FCSTD DOCUMENT  (FreeCAD 0.22R34651 (Git))
Label: composit_stand5
License: All rights reserved
LicenseURL: http://en.wikipedia.org/wiki/All_rights_reserved
objects: Sketcher::SketchObject×88, Part::FeaturePython×57, PartDesign::Pocket×43, PartDesign::SubShapeBinder×37, PartDesign::Body×23, PartDesign::FeaturePython×21, Part::Compound×18, PartDesign::Pad×17, PartDesign::Mirrored×11, PartDesign::Boolean×9, App::DocumentObjectGroup×8, App::Link×6, Part::Mirroring×6, TechDraw::DrawViewPart×6, Part::Part2DObjectPython×5, Part::Extrusion×4, PartDesign::CoordinateSystem×4, PartDesign::Hole×4, Path::FeaturePython×4, TechDraw::DrawViewDimension×4, +12 more types
note: 435 computed .brp shape members not serialized (recipe doc carries the construction recipe); baked Part::Feature solids carry a one-line shape summary decoded from their .brp
EXTERNAL_REF file=module.FCStd obj=Spreadsheet
EXTERNAL_REF file=module.FCStd obj=Sketch
EXTERNAL_REF file=module.FCStd obj=Body
EXTERNAL_REF file=composit-properties.FCStd obj=Spreadsheet
EXTERNAL_REF file=dropper.FCStd obj=Part
EXTERNAL_REF file=ULI-3865416.FCStd obj=Spreadsheet
EXTERNAL_REF file=UST-E32 WHITE 2M.FCStd obj=Body

FEATURE [Sketcher::SketchObject] Sketch005  label="main_sketch"
  FullyConstrained = true
  expr: Constraints[25] = module#<<Properties>>.module_width * 2 + 2 mm * 1
  sketch-geometry (11):
    g0: LineSegment StartX=-290.084 StartY=134.058 StartZ=0 EndX=-164.614 EndY=0 EndZ=0
    g1: LineSegment StartX=-164.614 StartY=0 StartZ=0 EndX=164.614 EndY=0 EndZ=0
    g2: LineSegment StartX=164.614 StartY=0 StartZ=0 EndX=290.084 EndY=134.058 EndZ=0
    g3: LineSegment StartX=-149 StartY=36 StartZ=0 EndX=149 EndY=36 EndZ=0
    g4: LineSegment StartX=149 StartY=36 StartZ=0 EndX=251.5 EndY=145.516 EndZ=0
    g5: LineSegment StartX=149 StartY=0 StartZ=0 EndX=149 EndY=36 EndZ=0
    g6: LineSegment StartX=149 StartY=36 StartZ=0 EndX=175.284 EndY=11.4 EndZ=0
    g7: LineSegment StartX=226.534 StartY=66.158 StartZ=0 EndX=200.25 EndY=90.758 EndZ=0
    g8: GeomPoint X=226.534 Y=66.158 Z=0
    g9: LineSegment StartX=-281.5 StartY=124.887 StartZ=0 EndX=281.5 EndY=124.887 EndZ=0
    g10: LineSegment StartX=251.5 StartY=145.516 StartZ=0 EndX=277.784 EndY=120.916 EndZ=0
  constraints (35):
    c: Coincident(g0,g1)
    c: Coincident(g1,g2)
    c: Symmetric(g1,g0,g-2)
    c: PointOnObject(g1,g-1)
    c: Symmetric(g0,g2,g-2)
    c: Coincident(g4,g3)
    c: PointOnObject(g5,g1)
    c: Coincident(g5,g3)
    c: Coincident(g5,g6)
    c: PointOnObject(g6,g2)
    c: Perpendicular(g6,g2)
    c: Perpendicular(g4,g6)
    c: Perpendicular(g1,g5)
    c: Equal(g5,g6)
    c: DistanceY(g5,g5) = 36
    c: DistanceX(g1,g1) = 329.228  'inner_width'
    c: Angle(g2) = 0.818478  'angle'
    c: Symmetric(g3,g3,g-2)
    c: Distance(g4) = 150
    c: PointOnObject(g7,g2)
    c: Perpendicular(g4,g7)
    c: Symmetric(g3,g4,g7)
    c: Coincident(g8,g7)
    c: DistanceY(g2) = 134.058  'length'
    c: DistanceX(g0,g2) = 580.168  'outer_width'
    c: DistanceX(g3,g3) = 298
    c: PointOnObject(g9,g0)
    c: PointOnObject(g9,g2)
    c: Horizontal(g9)
    c: DistanceX(g9,g9) = 563
    c: DistanceX(g3,g4) = 102.5
    c: Coincident(g10,g4)
    c: PointOnObject(g10,g2)
    c: Perpendicular(g4,g10)
    c: Distance(g10,g2) = 18
FEATURE [Part::FeaturePython] Placment  # WARN: FeaturePython — macro-defined, semantics opaque (R4)
  AttacherType = Attacher::AttachEngine3D
  AttachmentOffset = pos=(0,0,0) rot=(-0.707107,0,0.707107;3.14159rad)
  ExposePlacement = true
  MapMode = 7
  MarkerShape = 1
  MarkerSize = 20
  NumElements = 1
  Placement = pos=(226.534,66.158,0) rot=(-0.852419,-0.369717,0.369717;1.7298rad)
  Support = -> [Sketch005]
  Type = lattice2AttachablePlacement.AttachablePlacement
  isLattice = 1
FEATURE [Part::FeaturePython] LinearArray  # WARN: FeaturePython — macro-defined, semantics opaque (R4)
  Alignment = 0
  CellStart = A1
  Count = 2
  Dir = (1,0,0)
  DirIsDriven = true
  DistributionLaw = 0
  DrivenProperty = 1
  EndInclusive = true
  ExposePlacement = false
  GeneratorMode = 1
  MarkerShape = 1
  MarkerSize = 0
  NumElements = 2
  OrientMode = 1
  Placement = pos=(-75,0,0) rot=(-1,0,0;1.5708rad)
  Point = (0,0,0)
  PointIsDriven = true
  Reverse = false
  SpanEnd = 150
  SpanStart = 0
  Step = 150
  Type = lattice2LinearArray.LinearArray
  VSGVersion = 1
  Values = 0.0 | 150.0
  ValuesSource = 2
  isLattice = 1
  expr: .Placement.Base.x = -.Dir.x * SpanEnd / 2
  expr: SpanEnd = Step * (Count - 1)
  expr: Step = module#<<Properties>>.module_width + 2 mm
FEATURE [App::Link] Link  label="module_holes"
  LinkedObject = -> <external module.FCStd>#Sketch
FEATURE [Part::Extrusion] Extrude
  Base = -> Link
  Dir = (0,0,1)
  DirMode = 2
  FaceMakerClass = Part::FaceMakerBullseye
  LengthFwd = 10
  LengthRev = 0
  Solid = true
  Symmetric = true
FEATURE [Part::FeaturePython] LinearArray001  # WARN: FeaturePython — macro-defined, semantics opaque (R4)
  Alignment = 0
  CellStart = A1
  Count = 5
  Dir = (1,0,0)
  DirIsDriven = true
  DistributionLaw = 0
  DrivenProperty = 1
  EndInclusive = true
  ExposePlacement = false
  GeneratorMode = 1
  MarkerShape = 1
  MarkerSize = 0
  NumElements = 5
  OrientMode = 1
  Placement = pos=(0,0,0) rot=(0,-1,0;1.5708rad)
  Point = (0,0,0)
  PointIsDriven = true
  Reverse = false
  SpanEnd = 100
  SpanStart = 0
  Step = 80
  Type = lattice2LinearArray.LinearArray
  VSGVersion = 1
  Values = 0.0 | 80.0 | 160.0 | 240.0 | 320.0
  ValuesSource = 2
  isLattice = 1
  expr: Step = module#<<Properties>>.module_fixture_distance_y
FEATURE [Part::FeaturePython] Placment001  # WARN: FeaturePython — macro-defined, semantics opaque (R4)
  AttacherType = Attacher::AttachEngine3D
  AttachmentOffset = pos=(0,0,0) rot=(0,0,1;3.14159rad)
  ExposePlacement = true
  MapMode = 2
  MarkerShape = 1
  MarkerSize = 50
  NumElements = 1
  Placement = pos=(226.534,66.158,0) rot=(-0.293211,0.676028,0.676028;3.71203rad)
  Support = -> [Placment]
  Type = lattice2AttachablePlacement.AttachablePlacement
  isLattice = 1
FEATURE [Part::FeaturePython] Mirror  label="Mirror of Placment"  # WARN: FeaturePython — macro-defined, semantics opaque (R4)
  ExposePlacement = false
  FlipX = true
  FlipY = false
  FlipZ = false
  MarkerShape = 1
  MarkerSize = 50
  NumElements = 1
  Object = -> Placment001
  ObjectTraversal = 0
  Type = lattice2Mirror.LatticeMirror
  isLattice = 1
FEATURE [Part::FeaturePython] Join  # WARN: FeaturePython — macro-defined, semantics opaque (R4)
  ExposePlacement = false
  Interleave = false
  Links = -> [LinearArray,Mirror,Placment]
  MarkerShape = 1
  MarkerSize = 10
  NumElements = 4
  Type = lattice2JoinArrays.JoinArrays
  isLattice = 1
FEATURE [Part::FeaturePython] Populate  label="Populate LinearArray001 with Join"  # WARN: FeaturePython — macro-defined, semantics opaque (R4)
  Copying = 0
  ExposePlacement = false
  MarkerShape = 1
  MarkerSize = 0
  NumElements = 20
  Object = -> Join
  OutputCompounding = 0
  PlacementsTo = -> LinearArray001
  Referencing = 1
  Type = lattice2PopulateCopies.LatticePopulateCopies
  isLattice = 1
FEATURE [Part::FeaturePython] Populate001  label="Populate Populate LinearArray001 with Join with Extrude"  # WARN: FeaturePython — macro-defined, semantics opaque (R4)
  Copying = 0
  ExposePlacement = false
  MarkerShape = 1
  MarkerSize = 0
  NumElements = 0
  Object = -> Extrude
  OutputCompounding = 1
  Placement = pos=(0,0,300) rot=(0,0,1;0rad)
  PlacementsTo = -> Populate
  Referencing = 0
  Type = lattice2PopulateCopies.LatticePopulateCopies
  isLattice = 0
FEATURE [App::Link] Link002  label="Body001"
  LinkPlacement = pos=(0,0,0) rot=(0,0,1;3.14159rad)
  LinkedObject = -> <external module.FCStd>#Body
  Placement = pos=(0,0,0) rot=(0,0,1;3.14159rad)
FEATURE [Part::FeaturePython] Populate004  label="modules"  # WARN: FeaturePython — macro-defined, semantics opaque (R4)
  Copying = 0
  ExposePlacement = false
  MarkerShape = 1
  MarkerSize = 0
  NumElements = 0
  Object = -> Link002
  OutputCompounding = 1
  Placement = pos=(0,0,300) rot=(0,0,1;0rad)
  PlacementsTo = -> Populate
  Referencing = 0
  Type = lattice2PopulateCopies.LatticePopulateCopies
  isLattice = 0
  expr: Placement = <<Populate Populate LinearArray001 with Join with Extrude>>.Placement
FEATURE [App::Link] Link001  label="Extrude002"
  LinkPlacement = pos=(170,0,0) rot=(0,0,1;0rad)
  LinkedObject = -> Extrude001
  Placement = pos=(170,0,0) rot=(0,0,1;0rad)
FEATURE [Part::Part2DObjectPython] Circle  label="hole_3.4"  # Draft 2D object (typed FeaturePython)
  Area = 9.0792
  FirstAngle = 0
  LastAngle = 0
  MakeFace = true
  Radius = 1.7
FEATURE [Part::Extrusion] Extrude001  label="hole_3.4_extrude"
  Base = -> Circle
  Dir = (0,0,1)
  DirMode = 2
  FaceMakerClass = Part::FaceMakerBullseye
  LengthFwd = 10
  LengthRev = 0
  Solid = false
  Symmetric = false
FEATURE [Part::FeaturePython] Clone001  label="Extrude004"  # Draft clone (typed FeaturePython)
  AttacherType = Attacher::AttachEngine3D
  Fuse = false
  Objects = -> [Extrude001]
  Placement = pos=(0,5,0) rot=(1,0,0;1.5708rad)
  Scale = (1,1,1)
FEATURE [Part::FeaturePython] Clone  label="Extrude003"  # Draft clone (typed FeaturePython)
  AttacherType = Attacher::AttachEngine3D
  Fuse = false
  Objects = -> [Extrude001]
  Placement = pos=(154.614,5,0) rot=(1,0,0;1.5708rad)
  Scale = (1,1,1)
  expr: .Placement.Base.x = <<main_sketch>>.Constraints.inner_width / 2 - 10 mm
FEATURE [Part::Compound] Compound003
  Links = -> [Link001,Extrude001]
  Placement = pos=(168.01,4.96989,0) rot=(0.852419,0.369717,0.369717;1.7298rad)
  expr: .Placement.Base.x = <<main_sketch>>.Constraints.inner_width / 2 + .Placement.Base.y * cos(<<main_sketch>>.Constraints.angle)
  expr: .Placement.Base.y = <<main_sketch>>.Constraints.length / 2 - <<Extrude002>>.Placement.Base.x * sin(<<main_sketch>>.Constraints.angle) / 2
  expr: .Placement.Rotation.Yaw = <<main_sketch>>.Constraints.angle
FEATURE [Part::Compound] Compound001
  Links = -> [Compound003,Clone]
FEATURE [Part::Mirroring] Part__Mirroring  label="Compound001 (Mirror #1)"
  Base = (0,0,0)
  Normal = (1,0,0)
  Source = -> Compound001
FEATURE [Part::Compound] Compound004
  Links = -> [Compound001,Part__Mirroring,Clone001]
  Placement = pos=(0,0,31) rot=(0,0,1;0rad)
FEATURE [Sketcher::SketchObject] Sketch007
  FullyConstrained = false
  MapMode = 5
  Placement = pos=(0,0,0) rot=(1,0,0;1.5708rad)
  Support = -> [XZ_Plane001]
  expr: Constraints[10] = BaseBend001.length
  sketch-geometry (5):
    g0: LineSegment StartX=-500 StartY=191.028 StartZ=0 EndX=-500 EndY=87 EndZ=0
    g1: LineSegment StartX=-500 StartY=87 StartZ=0 EndX=500 EndY=87 EndZ=0
    g2: LineSegment StartX=500 StartY=87 StartZ=0 EndX=500 EndY=191.028 EndZ=0
    g3: LineSegment StartX=500 StartY=191.028 StartZ=0 EndX=-500 EndY=191.028 EndZ=0
    g4: GeomPoint X=0 Y=139.014 Z=0
  constraints (12):
    c: Coincident(g0,g1)
    c: Coincident(g1,g2)
    c: Coincident(g2,g3)
    c: Coincident(g3,g0)
    c: Horizontal(g1)
    c: Horizontal(g3)
    c: Vertical(g0)
    c: Vertical(g2)
    c: Symmetric(g1,g0,g4)
    c: PointOnObject(g4,g-2)
    c: DistanceX(g1,g1) = 1000
    c: DistanceY(g1) = 87
FEATURE [Part::Part2DObjectPython] Line  # Draft 2D object (typed FeaturePython)
  Area = 0
  Bend_Angle = 6.03317
  ChamferSize = 0
  Closed = false
  End = (290.084,134.058,14.0901)
  FilletRadius = 0
  Length = 184.154
  MakeFace = true
  Points = (2) [(164.614,0,0),(290.084,134.058,14.0901)]
  SideAngle = 4.1058
  Start = (164.614,0,0)
  Subdivisions = 0
  expr: .End.x = Sketch005.Constraints.outer_width / 2
  expr: .End.y = <<sink_base>>.Constraints.length
  expr: .End.z = <<sink_base>>.Constraints.sink_difference
  expr: .Start.x = <<main_sketch>>.Constraints.inner_width / 2
  expr: Bend_Angle = asin(.End.z / .End.y)
  expr: SideAngle = asin(.End.z / (.End.y + (.End.x - .Start.x) / 2))
FEATURE [PartDesign::SubShapeBinder] Binder
  BindCopyOnChange = 0
  BindMode = 0
  ClaimChildren = false
  Context = -> Part [Body001.Binder.]
  Fuse = false
  MakeFace = true
  OffsetFill = false
  OffsetIntersection = false
  OffsetJoinType = 0
  OffsetOpenResult = false
  PartialLoad = false
  Relative = false
  Support = -> [Sketch005]
  _Version = 2
FEATURE [Sketcher::SketchObject] Sketch006
  ExternalGeometry = -> [Binder]
  FullyConstrained = true
  MapMode = 5
  Support = -> [XY_Plane001]
  sketch-geometry (1):
    g0: LineSegment StartX=161.19 StartY=0 StartZ=0 EndX=286.66 EndY=134.058 EndZ=0
  constraints (5):
    c: PointOnObject(g0,g-1)
    c: Horizontal(g0,g-3)
    c: Parallel(g-3,g0)
    c: Distance(g0,g-3) = 2.5
    c: DistanceX(g0) = 286.66  'max_right'
FEATURE [Sketcher::SketchObject] Sketch001  label="sink_base"
  ExternalGeometry = -> [Binder]
  FullyConstrained = true
  MapMode = 5
  Placement = pos=(0,0,0) rot=(0.57735,0.57735,0.57735;2.0944rad)
  Support = -> [YZ_Plane001]
  sketch-geometry (4):
    g0: LineSegment StartX=0 StartY=0 StartZ=0 EndX=0 EndY=90 EndZ=0
    g1: LineSegment StartX=0 StartY=0 StartZ=0 EndX=134.058 EndY=14.0901 EndZ=0
    g2: ArcOfCircle CenterX=2.5 CenterY=2.77653 CenterZ=0 NormalX=0 NormalY=0 NormalZ=1 AngleXU=0 Radius=2.5 StartAngle=3.14159 EndAngle=4.81711
    g3: GeomPoint X=2.76132 Y=0.290227 Z=0
  constraints (13):
    c: Vertical(g0)
    c: Coincident(g1,g0)
    c: Angle(g1) = 0.10472  'angle'
    c: DistanceY(g0,g0) = 90
    c: Coincident(g0,g-1)
    c: Vertical(g-3,g1)
    c: DistanceX(g1) = 134.058  'length'
    c: DistanceY(g1) = 14.0901  'sink_difference'
    c: Tangent(g2,g1) = -1.5708
    c: Tangent(g2,g0) = 1.5708
    c: Radius(g2) = 2.5
    c: DistanceX(g2) = 2.76132
    c: Coincident(g3,g2)
FEATURE [Sketcher::SketchObject] Sketch004
  ExternalGeometry = -> [Sketch001]
  FullyConstrained = false
  MapMode = 7
  Placement = pos=(164.614,-1.42e-14,0) rot=(0.880512,-0.347772,-0.322108;1.77331rad)
  Support = -> [Line]
  sketch-geometry (9):
    g0: LineSegment StartX=-120.186 StartY=8.60659 StartZ=0 EndX=0 EndY=0 EndZ=0
    g1: ArcOfCircle CenterX=-2.5 CenterY=2.68543 CenterZ=0 NormalX=0 NormalY=0 NormalZ=1 AngleXU=0 Radius=2.5 StartAngle=4.6409 EndAngle=6.28319
    g2: LineSegment StartX=-2.67857 StartY=0.191814 StartZ=0 EndX=-2.64286 EndY=0.690537 EndZ=0
    g3: LineSegment StartX=-0.5 StartY=2.68543 StartZ=0 EndX=-0.5 EndY=11.4404 EndZ=0
    g4: LineSegment StartX=-0.5 StartY=11.4404 StartZ=0 EndX=-1.1e-15 EndY=11.4404 EndZ=0
    g5: LineSegment StartX=-1.1e-15 StartY=11.4404 StartZ=0 EndX=0 EndY=2.68543 EndZ=0
    g6: ArcOfCircle CenterX=-2.5 CenterY=2.68543 CenterZ=0 NormalX=0 NormalY=0 NormalZ=1 AngleXU=0 Radius=2 StartAngle=4.6409 EndAngle=6.28319
    g7: LineSegment StartX=0 StartY=2.68543 StartZ=0 EndX=-2.5 EndY=2.68543 EndZ=0
    g8: LineSegment StartX=-2.67857 StartY=0.191814 StartZ=0 EndX=-2.5 EndY=2.68543 EndZ=0
  constraints (21):
    c: Coincident(g0,g-3)
    c: Coincident(g0,g-1)
    c: Tangent(g1,g-2) = -1.5708
    c: Radius(g1) = 2.5
    c: Tangent(g1,g0) = -1.5708
    c: Coincident(g2,g1)
    c: Vertical(g3)
    c: Coincident(g4,g3)
    c: Coincident(g5,g4)
    c: Tangent(g5,g1) = 1.5708
    c: Horizontal(g4)
    c: Perpendicular(g1,g2)
    c: Coincident(g6,g1)
    c: Coincident(g6,g2)
    c: Tangent(g6,g3) = -1.5708
    c: Radius(g6) = 2
    c: Coincident(g7,g1)
    c: Coincident(g7,g1)
    c: Coincident(g8,g1)
    c: Coincident(g8,g1)
    c: Angle(g8,g7) = 1.64228
FEATURE [PartDesign::SubShapeBinder] Binder006
  BindCopyOnChange = 0
  BindMode = 0
  ClaimChildren = true
  Context = -> Body002 [Binder006.]
  Fuse = false
  MakeFace = true
  OffsetFill = false
  OffsetIntersection = false
  OffsetJoinType = 0
  OffsetOpenResult = false
  PartialLoad = false
  Relative = false
  Support = -> [Compound006]
  _Version = 2
FEATURE [PartDesign::Pad] Pad
  Direction = (0,0,1)
  Length = 5
  Length2 = 10
  Profile = -> Binder006
  Type = 0
FEATURE [PartDesign::SubShapeBinder] Binder007
  BindCopyOnChange = 0
  BindMode = 0
  ClaimChildren = true
  Context = -> Body002 [Binder007.]
  Fuse = false
  MakeFace = true
  OffsetFill = false
  OffsetIntersection = false
  OffsetJoinType = 0
  OffsetOpenResult = false
  PartialLoad = false
  Relative = false
  Support = -> [Populate008]
  _Version = 2
FEATURE [PartDesign::Pocket] Pocket005
  BaseFeature = -> Pad
  Direction = (0,0,-1)
  Length = 2.5
  Length2 = 5
  Profile = -> Binder007
  Reversed = true
  Type = 0
FEATURE [Part::Box] Box  label="Cube"
  AttacherType = Attacher::AttachEngine3D
  AttachmentOffset = pos=(0,0,-5) rot=(0,0,1;0rad)
  Height = 60
  Length = 560
  Placement = pos=(-280,0,-9) rot=(0,0,1;0rad)
  Width = 60
  expr: .Placement.Base.x = -Length / 2
FEATURE [PartDesign::SubShapeBinder] Binder004  label="fix"
  BindCopyOnChange = 0
  BindMode = 0
  ClaimChildren = false
  Fuse = false
  MakeFace = true
  Offset = 0.5
  OffsetFill = false
  OffsetIntersection = false
  OffsetJoinType = 0
  OffsetOpenResult = false
  PartialLoad = false
  Relative = true
  Support = -> [<external dropper.FCStd>#Part[Body.Binder.]]
  _Version = 2
FEATURE [PartDesign::SubShapeBinder] Binder008
  BindCopyOnChange = 0
  BindMode = 0
  ClaimChildren = true
  Context = -> Body002 [Binder008.]
  Fuse = false
  MakeFace = true
  OffsetFill = false
  OffsetIntersection = false
  OffsetJoinType = 0
  OffsetOpenResult = false
  PartialLoad = false
  Relative = false
  Support = -> [Populate010]
  _Version = 2
FEATURE [PartDesign::Pocket] Pocket006
  BaseFeature = -> Pocket005
  Direction = (0,0,-1)
  Length = 5
  Length2 = 5
  Midplane = true
  Profile = -> Binder008
  Type = 1
FEATURE [PartDesign::SubShapeBinder] Binder005  label="feed"
  BindCopyOnChange = 0
  BindMode = 0
  ClaimChildren = false
  Fuse = false
  MakeFace = true
  OffsetFill = false
  OffsetIntersection = false
  OffsetJoinType = 0
  OffsetOpenResult = false
  PartialLoad = false
  Relative = true
  Support = -> [<external dropper.FCStd>#Part[Body.Sketch008.]]
  _Version = 2
FEATURE [PartDesign::SubShapeBinder] Binder001
  BindCopyOnChange = 0
  BindMode = 0
  ClaimChildren = false
  Context = -> Body [Binder001.]
  Fuse = false
  MakeFace = true
  OffsetFill = false
  OffsetIntersection = false
  OffsetJoinType = 0
  OffsetOpenResult = false
  PartialLoad = false
  Relative = true
  Support = -> [Sketch005]
  _Version = 2
FEATURE [Sketcher::SketchObject] Sketch009
  ExternalGeometry = -> [Binder001]
  FullyConstrained = true
  MapMode = 5
  Support = -> [XY_Plane]
  expr: Constraints[12] = composit_properties#<<Properties>>.al_thickness
  expr: Constraints[13] = -composit_properties#<<Properties>>.thickness
  sketch-geometry (5):
    g0: LineSegment StartX=0 StartY=-3 StartZ=0 EndX=0 EndY=109.928 EndZ=0
    g1: LineSegment StartX=0 StartY=109.928 StartZ=0 EndX=267.5 EndY=109.928 EndZ=0
    g2: LineSegment StartX=267.5 StartY=109.928 StartZ=0 EndX=267.719 EndY=109.723 EndZ=0
    g3: LineSegment StartX=267.719 StartY=109.723 StartZ=0 EndX=267.719 EndY=-3 EndZ=0
    g4: LineSegment StartX=267.719 StartY=-3 StartZ=0 EndX=0 EndY=-3 EndZ=0
  constraints (15):
    c: PointOnObject(g0,g-2)
    c: Coincident(g0,g1)
    c: Horizontal(g1)
    c: Coincident(g1,g2)
    c: Coincident(g2,g3)
    c: Vertical(g3)
    c: Coincident(g3,g4)
    c: DistanceX(g1,g1) = 267.5
    c: PointOnObject(g1,g-3)
    c: Coincident(g4,g0)
    c: Vertical(g0)
    c: Horizontal(g4)
    c: Distance(g2) = 0.3
    c: DistanceY(g0) = -3
    c: Perpendicular(g-3,g2)
FEATURE [Sketcher::SketchObject] Sketch  label="base_sketch"
  ExternalGeometry = -> [Binder001]
  FullyConstrained = true
  sketch-geometry (9):
    g0: LineSegment StartX=-164.614 StartY=0 StartZ=0 EndX=164.614 EndY=0 EndZ=0
    g1: LineSegment StartX=164.614 StartY=0 StartZ=0 EndX=290.084 EndY=134.058 EndZ=0
    g2: LineSegment StartX=290.084 StartY=134.058 StartZ=0 EndX=300.084 EndY=134.058 EndZ=0
    g3: LineSegment StartX=300.084 StartY=134.058 StartZ=0 EndX=300.084 EndY=-41 EndZ=0
    g4: LineSegment StartX=-164.614 StartY=0 StartZ=0 EndX=-290.084 EndY=134.058 EndZ=0
    g5: LineSegment StartX=-290.084 StartY=134.058 StartZ=0 EndX=-300.084 EndY=134.058 EndZ=0
    g6: LineSegment StartX=-300.084 StartY=134.058 StartZ=0 EndX=-300.084 EndY=-41 EndZ=0
    g7: LineSegment StartX=297.084 StartY=-41 StartZ=0 EndX=300.084 EndY=-41 EndZ=0
    g8: LineSegment StartX=-300.084 StartY=-41 StartZ=0 EndX=-297.084 EndY=-41 EndZ=0
  constraints (23):
    c: Coincident(g0,g-3)
    c: Coincident(g0,g1)
    c: Coincident(g1,g-3)
    c: Coincident(g1,g2)
    c: Horizontal(g2)
    c: Coincident(g2,g3)
    c: Vertical(g3)
    c: Coincident(g0,g4)
    c: Coincident(g4,g5)
    c: Coincident(g5,g6)
    c: Symmetric(g0,g0,g-2)
    c: Symmetric(g1,g4,g-2)
    c: Symmetric(g5,g2,g-2)
    c: Symmetric(g3,g6,g-2)
    c: DistanceX(g2,g2) = 10
    c: DistanceY(g3) = -41  'back_offset'
    c: DistanceX(g6,g3) = 600.168  'outer_width'
    c: Coincident(g7,g3)
    c: Coincident(g8,g6)
    c: Horizontal(g8)
    c: Equal(g8,g7)
    c: Horizontal(g7)
    c: DistanceX(g7,g7) = 3
FEATURE [PartDesign::SubShapeBinder] Binder009
  BindCopyOnChange = 0
  BindMode = 0
  ClaimChildren = false
  Context = -> Part002 [Body003.Binder009.]
  Fuse = false
  MakeFace = true
  OffsetFill = false
  OffsetIntersection = false
  OffsetJoinType = 0
  OffsetOpenResult = false
  PartialLoad = false
  Relative = true
  Support = -> [Sketch005]
  _Version = 2
FEATURE [Sketcher::SketchObject] Sketch011  label="top_BaseSketch"
  ExternalGeometry = -> [Binder009]
  FullyConstrained = true
  Placement = pos=(0,0,0) rot=(0.57735,0.57735,0.57735;2.0944rad)
  expr: Constraints[8] = <<ULI-3865416>>#<<Properties>>.width
  sketch-geometry (4):
    g0: LineSegment StartX=158.611 StartY=20.0409 StartZ=0 EndX=138.225 EndY=23.6354 EndZ=0
    g1: LineSegment StartX=138.225 StartY=23.6354 StartZ=0 EndX=134.058 EndY=0 EndZ=0
    g2: LineSegment StartX=134.058 StartY=0 StartZ=0 EndX=-15 EndY=0 EndZ=0
    g3: GeomPoint X=158.611 Y=20.0409 Z=0
  constraints (11):
    c: Coincident(g0,g1)
    c: Coincident(g1,g2)
    c: Horizontal(g2)
    c: DistanceY(g2) = 0
    c: DistanceX(g2,g-1) = 15
    c: Vertical(g-3,g1)
    c: Perpendicular(g1,g0)
    c: Angle(g1,g-1) = 1.74533
    c: Distance(g0) = 20.7
    c: Distance(g1) = 24
    c: Coincident(g3,g0)
FEATURE [PartDesign::SubShapeBinder] Binder010
  BindCopyOnChange = 0
  BindMode = 0
  ClaimChildren = true
  Context = -> Body003 [Binder010.]
  Fuse = false
  MakeFace = true
  OffsetFill = false
  OffsetIntersection = false
  OffsetJoinType = 0
  OffsetOpenResult = false
  PartialLoad = false
  Relative = false
  Support = -> [Populate009]
  _Version = 2
FEATURE [Part::FeaturePython] LinearArray002  # WARN: FeaturePython — macro-defined, semantics opaque (R4)
  Alignment = 0
  CellStart = A1
  Count = 2
  Dir = (1,0,0)
  DirIsDriven = true
  DistributionLaw = 0
  DrivenProperty = 1
  EndInclusive = true
  ExposePlacement = false
  GeneratorMode = 0
  MarkerShape = 1
  MarkerSize = 0
  NumElements = 2
  OrientMode = 1
  Placement = pos=(-32.5,0,14) rot=(1,0,0;1.5708rad)
  Point = (0,0,0)
  PointIsDriven = true
  Reverse = false
  SpanEnd = 65
  SpanStart = 0
  Step = 65
  Type = lattice2LinearArray.LinearArray
  VSGVersion = 1
  Values = 0.0 | 65.0
  ValuesSource = 2
  isLattice = 1
  expr: .Placement.Base.x = -SpanEnd / 2
FEATURE [Part::FeaturePython] Populate007  label="droppers_placements"  # WARN: FeaturePython — macro-defined, semantics opaque (R4)
  Copying = 0
  ExposePlacement = false
  MarkerShape = 1
  MarkerSize = 10
  NumElements = 8
  Object = -> LinearArray002
  OutputCompounding = 0
  PlacementsTo = -> Join
  Referencing = 0
  Type = lattice2PopulateCopies.LatticePopulateCopies
  isLattice = 1
FEATURE [Part::FeaturePython] ArrayFilter  # WARN: FeaturePython — macro-defined, semantics opaque (R4)
  Base = -> Populate007
  ExposePlacement = false
  FilterType = 3
  Invert = false
  MarkerShape = 1
  MarkerSize = 0
  NumElements = 6
  Stencil = -> Box
  Type = lattice2ArrayFilter.LatticeArrayFilter
  WindowFrom = 0
  WindowTo = 1
  isLattice = 1
FEATURE [Part::FeaturePython] Placment002  # WARN: FeaturePython — macro-defined, semantics opaque (R4)
  AttacherType = Attacher::AttachEngine3D
  AttachmentOffset = pos=(0,0,0) rot=(-0.5774,0.5774,0.5774;2.0944rad)
  ExposePlacement = true
  MapMode = 1
  MarkerShape = 1
  MarkerSize = 50
  NumElements = 1
  Placement = pos=(238.521,99.4531,0) rot=(0,0,1;0rad)
  Support = -> [Populate007]
  Type = lattice2AttachablePlacement.AttachablePlacement
  isLattice = 1
  expr: .AttachmentOffset.Base.x = sin(<<main_sketch>>.Constraints.angle) * .AttachmentOffset.Base.y
FEATURE [Part::FeaturePython] Mirror001  label="Mirror001 of Placment002"  # WARN: FeaturePython — macro-defined, semantics opaque (R4)
  ExposePlacement = false
  FlipX = true
  FlipY = false
  FlipZ = false
  MarkerShape = 1
  MarkerSize = 50
  NumElements = 1
  Object = -> Placment002
  ObjectTraversal = 0
  Type = lattice2Mirror.LatticeMirror
  isLattice = 1
FEATURE [Part::FeaturePython] Join001  label="dropper_placement2"  # WARN: FeaturePython — macro-defined, semantics opaque (R4)
  ExposePlacement = false
  Interleave = false
  Links = -> [Placment002,Mirror001,ArrayFilter]
  MarkerShape = 1
  MarkerSize = 10
  NumElements = 8
  Type = lattice2JoinArrays.JoinArrays
  isLattice = 1
FEATURE [Part::FeaturePython] Populate010  label="feeds"  # WARN: FeaturePython — macro-defined, semantics opaque (R4)
  Copying = 0
  ExposePlacement = false
  MarkerShape = 1
  MarkerSize = 0
  NumElements = 0
  Object = -> Binder005
  OutputCompounding = 1
  PlacementsTo = -> Join001
  Referencing = 0
  Type = lattice2PopulateCopies.LatticePopulateCopies
  isLattice = 0
FEATURE [PartDesign::SubShapeBinder] Binder003  label="base"
  BindCopyOnChange = 0
  BindMode = 0
  ClaimChildren = false
  Fuse = false
  MakeFace = true
  OffsetFill = false
  OffsetIntersection = false
  OffsetJoinType = 0
  OffsetOpenResult = false
  PartialLoad = false
  Relative = true
  Support = -> [<external dropper.FCStd>#Part[Body001.Sketch007.]]
  _Version = 2
FEATURE [Part::Compound] Compound005
  Links = -> [Binder003,Binder004]
FEATURE [Part::FeaturePython] FuseCompound  # WARN: FeaturePython — macro-defined, semantics opaque (R4)
  Base = -> Compound005
  Refine = true
  recomputeQuota = -1
FEATURE [Part::FeaturePython] Populate008  label="Populate Populate Join with LinearArray002 with FuseCompound"  # WARN: FeaturePython — macro-defined, semantics opaque (R4)
  Copying = 0
  ExposePlacement = false
  MarkerShape = 1
  MarkerSize = 0
  NumElements = 0
  Object = -> FuseCompound
  OutputCompounding = 1
  PlacementsTo = -> Join001
  Referencing = 0
  Type = lattice2PopulateCopies.LatticePopulateCopies
  isLattice = 0
FEATURE [Sketcher::SketchObject] Sketch010
  ExternalGeometry = -> [Sketch005,Populate008]
  FullyConstrained = false
  sketch-geometry (18):
    g0: LineSegment StartX=0 StartY=17.85 StartZ=0 EndX=139.351 EndY=17.85 EndZ=0
    g1: LineSegment StartX=146.652 StartY=21.0167 StartZ=0 EndX=220.703 EndY=100.136 EndZ=0
    g2: LineSegment StartX=228.004 StartY=103.303 StartZ=0 EndX=262.098 EndY=103.303 EndZ=0
    g3: LineSegment StartX=219.146 StartY=96.2647 StartZ=0 EndX=219.817 EndY=99.1889 EndZ=0
    g4: LineSegment StartX=91 StartY=17.75 StartZ=0 EndX=91 EndY=17.85 EndZ=0
    g5: LineSegment StartX=222.021 StartY=103.203 StartZ=0 EndX=222.021 EndY=103.303 EndZ=0
    g6: LineSegment StartX=265.749 StartY=94.8865 StartZ=0 EndX=171.481 EndY=-5.83333 EndZ=0
    g7: LineSegment StartX=164.18 StartY=-9 StartZ=0 EndX=0 EndY=-9 EndZ=0
    g8: LineSegment StartX=171.185 StartY=-6.15 StartZ=0 EndX=164.614 EndY=0 EndZ=0
    g9: LineSegment StartX=164.614 StartY=0 StartZ=0 EndX=164.614 EndY=-9 EndZ=0
    g10: ArcOfCircle CenterX=139.351 CenterY=27.85 CenterZ=0 NormalX=0 NormalY=0 NormalZ=1 AngleXU=0 Radius=10 StartAngle=4.71239 EndAngle=5.53087
    g11: GeomPoint X=143.688 Y=17.85 Z=0
    g12: ArcOfCircle CenterX=228.004 CenterY=93.3031 CenterZ=0 NormalX=0 NormalY=0 NormalZ=1 AngleXU=0 Radius=10 StartAngle=1.5708 EndAngle=2.38927
    g13: GeomPoint X=223.667 Y=103.303 Z=0
    g14: ArcOfCircle CenterX=262.098 CenterY=98.3031 CenterZ=0 NormalX=0 NormalY=0 NormalZ=1 AngleXU=0 Radius=5 StartAngle=5.53087 EndAngle=7.85398
    g15: GeomPoint X=261.299 Y=103.303 Z=0
    g16: ArcOfCircle CenterX=164.18 CenterY=1 CenterZ=0 NormalX=0 NormalY=0 NormalZ=1 AngleXU=0 Radius=10 StartAngle=4.71239 EndAngle=5.53087
    g17: GeomPoint X=168.518 Y=-9 Z=0
  constraints (49):
    c: PointOnObject(g0,g-2)
    c: Horizontal(g0)
    c: Horizontal(g2)
    c: PointOnObject(g3,g1)
    c: PointOnObject(g4,g0)
    c: Vertical(g4)
    c: PointOnObject(g5,g2)
    c: Vertical(g5)
    c: DistanceY(g5,g5) = 0.1
    c: PointOnObject(g7,g-2)
    c: Horizontal(g7)
    c: PointOnObject(g8,g6)
    c: Coincident(g8,g9)
    c: PointOnObject(g9,g7)
    c: Vertical(g9)
    c: Equal(g9,g8)
    c: DistanceY(g7,g-1) = 9
    c: PointOnObject(g5,g-4)
    c: PointOnObject(g-4,g5)
    c: Perpendicular(g-6,g3)
    c: PointOnObject(g4,g-5)
    c: PointOnObject(g-5,g4)
    c: Equal(g4,g5)
    c: Parallel(g1,g-3)
    c: Parallel(g6,g-3)
    c: PointOnObject(g15,g-3)
    c: Coincident(g8,g-3)
    c: Perpendicular(g6,g8)
    c: PointOnObject(g11,g0)
    c: PointOnObject(g11,g1)
    c: Tangent(g0,g10) = -1.5708
    c: Tangent(g1,g10) = -1.5708
    c: PointOnObject(g13,g1)
    c: PointOnObject(g13,g2)
    c: Tangent(g1,g12) = 1.5708
    c: Tangent(g2,g12) = 1.5708
    c: Equal(g12,g10)
    c: Radius(g12) = 10
    c: PointOnObject(g15,g2)
    c: Tangent(g2,g14) = 1.5708
    c: PointOnObject(g17,g6)
    c: PointOnObject(g17,g7)
    c: Tangent(g6,g16) = 1.5708
    c: Tangent(g7,g16) = 1.5708
    c: Equal(g16,g12)
    c: PointOnObject(g3,g-6)
    c: Tangent(g6,g14) = 1.5708
    c: Distance(g3) = 3
    c: Radius(g14) = 5
FEATURE [Part::Mirroring] Part__Mirroring001  label="Sketch010 (Mirror #2)"
  Base = (0,0,0)
  Normal = (1,0,0)
  Source = -> Sketch010
FEATURE [Part::Compound] Compound006
  Links = -> [Sketch010,Part__Mirroring001]
FEATURE [Part::FeaturePython] Populate009  label="Populate Populate Join with LinearArray002 with base"  # WARN: FeaturePython — macro-defined, semantics opaque (R4)
  Copying = 0
  ExposePlacement = false
  MarkerShape = 1
  MarkerSize = 0
  NumElements = 0
  Object = -> Binder003
  OutputCompounding = 1
  PlacementsTo = -> Join001
  Referencing = 0
  Type = lattice2PopulateCopies.LatticePopulateCopies
  isLattice = 0
FEATURE [PartDesign::SubShapeBinder] Binder011
  BindCopyOnChange = 0
  BindMode = 0
  ClaimChildren = true
  Context = -> Body004 [Binder011.]
  Fuse = false
  MakeFace = true
  OffsetFill = false
  OffsetIntersection = false
  OffsetJoinType = 0
  OffsetOpenResult = false
  PartialLoad = false
  Relative = true
  Support = -> [Body[BaseBend.Sketch.]]
  _Version = 2
FEATURE [Sketcher::SketchObject] Sketch012
  ExternalGeometry = -> [Binder011]
  FullyConstrained = true
  MapMode = 5
  Support = -> [XY_Plane004]
  sketch-geometry (3):
    g0: LineSegment StartX=297.084 StartY=-31 StartZ=0 EndX=297.084 EndY=-41 EndZ=0
    g1: LineSegment StartX=297.084 StartY=-41 StartZ=0 EndX=-297.084 EndY=-41 EndZ=0
    g2: LineSegment StartX=-297.084 StartY=-41 StartZ=0 EndX=-297.084 EndY=-31 EndZ=0
  constraints (9):
    c: Vertical(g0)
    c: Coincident(g0,g1)
    c: Horizontal(g1)
    c: Coincident(g1,g2)
    c: Vertical(g2)
    c: Symmetric(g2,g0,g-2)
    c: DistanceY(g0,g0) = 10
    c: Horizontal(g0,g-3)
    c: DistanceX(g0,g-3) = 3
FEATURE [PartDesign::FeaturePython] BaseBend003  # WARN: FeaturePython — macro-defined, semantics opaque (R4)
  BendSide = 0
  BendSketch = -> Sketch012
  MidPlane = false
  Reverse = false
  length = 637
  radius = 0.1
  thickness = 0.3
  expr: length = BaseBend.length - 3 mm
FEATURE [Part::FeaturePython] LinearArray003  # WARN: FeaturePython — macro-defined, semantics opaque (R4)
  Alignment = 0
  CellStart = A1
  Count = 5
  Dir = (1,0,0)
  DirIsDriven = true
  DistributionLaw = 0
  DrivenProperty = 1
  EndInclusive = true
  ExposePlacement = false
  GeneratorMode = 0
  MarkerShape = 1
  MarkerSize = 0
  NumElements = 5
  OrientMode = 1
  Placement = pos=(-294.084,-36,0) rot=(0,-1,0;1.5708rad)
  Point = (0,0,0)
  PointIsDriven = true
  Reverse = false
  SpanEnd = 610
  SpanStart = 30
  Step = 145
  Type = lattice2LinearArray.LinearArray
  VSGVersion = 1
  Values = 30.0 | 175.0 | 320.0 | 465.0 | 610.0
  ValuesSource = 2
  isLattice = 1
  expr: .Placement.Base.x = -(<<base_sketch>>.Constraints.outer_width / 2 - 6 mm)
  expr: .Placement.Base.y = <<base_sketch>>.Constraints.back_offset + 5 mm
  expr: SpanEnd = BaseBend.length - SpanStart
FEATURE [Part::FeaturePython] Mirror002  label="Mirror002 of LinearArray003"  # WARN: FeaturePython — macro-defined, semantics opaque (R4)
  ExposePlacement = false
  FlipX = true
  FlipY = false
  FlipZ = false
  MarkerShape = 1
  MarkerSize = 0
  NumElements = 5
  Object = -> LinearArray003
  ObjectTraversal = 0
  Type = lattice2Mirror.LatticeMirror
  isLattice = 1
FEATURE [Part::FeaturePython] Join002  # WARN: FeaturePython — macro-defined, semantics opaque (R4)
  ExposePlacement = false
  Interleave = false
  Links = -> [LinearArray003,Mirror002]
  MarkerShape = 1
  MarkerSize = 0
  NumElements = 10
  Type = lattice2JoinArrays.JoinArrays
  isLattice = 1
FEATURE [Part::FeaturePython] Populate011  label="Populate Join002 with Extrude001"  # WARN: FeaturePython — macro-defined, semantics opaque (R4)
  Copying = 0
  ExposePlacement = false
  MarkerShape = 1
  MarkerSize = 0
  NumElements = 0
  Object = -> Extrude001
  OutputCompounding = 1
  PlacementsTo = -> Join002
  Referencing = 0
  Type = lattice2PopulateCopies.LatticePopulateCopies
  isLattice = 0
FEATURE [Sketcher::SketchObject] Sketch013
  ExternalGeometry = -> [Sketch]
  FullyConstrained = true
  MapMode = 5
  Support = -> [XY_Plane]
  sketch-geometry (23):
    g0: Circle CenterX=204.177 CenterY=33.9297 CenterZ=0 NormalX=0 NormalY=0 NormalZ=1 AngleXU=0 Radius=1.7
    g1: Circle CenterX=258.844 CenterY=92.3382 CenterZ=0 NormalX=0 NormalY=0 NormalZ=1 AngleXU=0 Radius=1.7
    g2: Circle CenterX=289.784 CenterY=89 CenterZ=0 NormalX=0 NormalY=0 NormalZ=1 AngleXU=0 Radius=1.7
    g3: Circle CenterX=120 CenterY=-5.7 CenterZ=0 NormalX=0 NormalY=0 NormalZ=1 AngleXU=0 Radius=1.7
    g4: Circle CenterX=0 CenterY=-5.7 CenterZ=0 NormalX=0 NormalY=0 NormalZ=1 AngleXU=0 Radius=1.7
    g5: LineSegment StartX=0 StartY=-5.7 StartZ=0 EndX=120 EndY=-5.7 EndZ=0
    g6: LineSegment StartX=204.177 StartY=33.9297 StartZ=0 EndX=258.844 EndY=92.3382 EndZ=0
    g7: LineSegment StartX=289.784 StartY=-41 StartZ=0 EndX=289.784 EndY=89 EndZ=0
    g8: LineSegment StartX=289.784 StartY=89 StartZ=0 EndX=300.084 EndY=89 EndZ=0
    g9: LineSegment StartX=258.844 StartY=92.3382 StartZ=0 EndX=254.682 EndY=96.2332 EndZ=0
    g10: LineSegment StartX=120 StartY=-5.7 StartZ=0 EndX=120 EndY=0 EndZ=0
    g11: Circle CenterX=-120 CenterY=-5.7 CenterZ=0 NormalX=0 NormalY=0 NormalZ=1 AngleXU=0 Radius=1.7
    g12: Circle CenterX=-204.177 CenterY=33.9297 CenterZ=0 NormalX=0 NormalY=0 NormalZ=1 AngleXU=0 Radius=1.7
    g13: Circle CenterX=-258.844 CenterY=92.3382 CenterZ=0 NormalX=0 NormalY=0 NormalZ=1 AngleXU=0 Radius=1.7
    g14: Circle CenterX=-289.784 CenterY=89 CenterZ=0 NormalX=0 NormalY=0 NormalZ=1 AngleXU=0 Radius=1.7
    g15: GeomPoint X=120 Y=-4 Z=0
    g16: LineSegment StartX=168.776 StartY=-3.895 StartZ=0 EndX=204.177 EndY=33.9297 EndZ=0
    g17: LineSegment StartX=258.844 StartY=92.3382 StartZ=0 EndX=294.245 EndY=130.163 EndZ=0
    g18: LineSegment StartX=290.084 StartY=134.058 StartZ=0 EndX=294.245 EndY=130.163 EndZ=0
    g19: LineSegment StartX=168.776 StartY=-3.895 StartZ=0 EndX=164.614 EndY=0 EndZ=0
    g20: GeomPoint X=288.084 Y=89 Z=0
    g21: Circle CenterX=289.784 CenterY=9 CenterZ=0 NormalX=0 NormalY=0 NormalZ=1 AngleXU=0 Radius=1.7
    g22: Circle CenterX=-289.784 CenterY=9 CenterZ=0 NormalX=0 NormalY=0 NormalZ=1 AngleXU=0 Radius=1.7
  constraints (55):
    c: PointOnObject(g4,g-2)
    c: Coincident(g5,g4)
    c: Coincident(g5,g3)
    c: Horizontal(g5)
    c: Coincident(g6,g0)
    c: Coincident(g6,g1)
    c: Coincident(g7,g2)
    c: Vertical(g7)
    c: Coincident(g8,g2)
    c: Horizontal(g8)
    c: Coincident(g9,g1)
    c: Coincident(g10,g3)
    c: PointOnObject(g10,g-1)
    c: Vertical(g10)
    c: Symmetric(g13,g1,g-2)
    c: Symmetric(g12,g0,g-2)
    c: Symmetric(g14,g2,g-2)
    c: Symmetric(g11,g3,g-2)
    c: Equal(g4,g3)
    c: Equal(g4,g0)
    c: Equal(g4,g1)
    c: Equal(g4,g2)
    c: Equal(g4, g11-g14) x4
    c: Diameter(g4) = 3.4
    c: PointOnObject(g15,g3)
    c: PointOnObject(g15,g10)
    c: DistanceY(g15,g10) = 4
    c: Coincident(g16,g0)
    c: Coincident(g17,g1)
    c: Coincident(g18,g17)
    c: Perpendicular(g17,g18)
    c: Parallel(g17,g6)
    c: Parallel(g16,g6)
    c: Coincident(g19,g16)
    c: Perpendicular(g16,g19)
    c: Equal(g16,g17)
    c: Distance(g6) = 80
    c: DistanceY(g7,g7) = 130
    c: DistanceX(g5,g5) = 120
    c: PointOnObject(g20,g2)
    c: PointOnObject(g20,g8)
    c: DistanceX(g20,g8) = 12
    c: Equal(g9,g10)
    c: Parallel(g6,g-4)
    c: Coincident(g19,g-4)
    c: Coincident(g18,g-4)
    c: PointOnObject(g9,g-4)
    c: Perpendicular(g6,g9)
    c: PointOnObject(g8,g-3)
    c: Horizontal(g7,g-3)
    c: PointOnObject(g21,g7)
    c: Equal(g21,g2)
    c: DistanceY(g21,g2) = 80
    c: Equal(g22,g21)
    c: Symmetric(g21,g22,g-2)
FEATURE [PartDesign::SubShapeBinder] Binder012
  BindCopyOnChange = 0
  BindMode = 0
  ClaimChildren = true
  Context = -> Part002 [Body003.Binder012.]
  Fuse = false
  MakeFace = true
  OffsetFill = false
  OffsetIntersection = false
  OffsetJoinType = 0
  OffsetOpenResult = false
  PartialLoad = false
  Relative = true
  Support = -> [Body[Pocket008.Sketch013.]]
  _Version = 2
FEATURE [PartDesign::SubShapeBinder] Binder013
  BindCopyOnChange = 0
  BindMode = 0
  ClaimChildren = false
  Context = -> Part002 [Body002.Binder013.]
  Fuse = false
  MakeFace = true
  OffsetFill = false
  OffsetIntersection = false
  OffsetJoinType = 0
  OffsetOpenResult = false
  PartialLoad = false
  Relative = true
  Support = -> [Body[Pocket008.Sketch013.]]
  _Version = 2
FEATURE [PartDesign::Pocket] Pocket010
  BaseFeature = -> Pocket006
  Direction = (0,0,-1)
  Length = 5
  Length2 = 5
  Midplane = true
  Profile = -> Binder013
  Type = 1
FEATURE [Sketcher::SketchObject] Sketch014
  FullyConstrained = true
  MapMode = 5
  Support = -> [XY_Plane005]
  sketch-geometry (12):
    g0: ArcOfCircle CenterX=-253.093 CenterY=-68.0931 CenterZ=0 NormalX=0 NormalY=0 NormalZ=1 AngleXU=0 Radius=12.4069 StartAngle=3.14159 EndAngle=4.71239
    g1: LineSegment StartX=-265.5 StartY=-68.0931 StartZ=0 EndX=-265.5 EndY=68.0931 EndZ=0
    g2: ArcOfCircle CenterX=-253.093 CenterY=68.0931 CenterZ=0 NormalX=0 NormalY=0 NormalZ=1 AngleXU=0 Radius=12.4069 StartAngle=1.5708 EndAngle=3.14159
    g3: LineSegment StartX=-253.093 StartY=80.5 StartZ=0 EndX=253.093 EndY=80.5 EndZ=0
    g4: ArcOfCircle CenterX=253.093 CenterY=68.0931 CenterZ=0 NormalX=0 NormalY=0 NormalZ=1 AngleXU=0 Radius=12.4069 StartAngle=0 EndAngle=1.5708
    g5: LineSegment StartX=265.5 StartY=68.0931 StartZ=0 EndX=265.5 EndY=-68.0931 EndZ=0
    g6: ArcOfCircle CenterX=253.093 CenterY=-68.0931 CenterZ=0 NormalX=0 NormalY=0 NormalZ=1 AngleXU=0 Radius=12.4069 StartAngle=4.71239 EndAngle=6.28319
    g7: LineSegment StartX=253.093 StartY=-80.5 StartZ=0 EndX=-253.093 EndY=-80.5 EndZ=0
    g8: GeomPoint X=-265.5 Y=-80.5 Z=0
    g9: GeomPoint X=265.5 Y=80.5 Z=0
    g10: LineSegment StartX=265.074 StartY=71.3165 StartZ=0 EndX=-265.074 EndY=-71.3165 EndZ=0
    g11: GeomPoint X=0 Y=0 Z=0
  constraints (26):
    c: Tangent(g0,g1) = 1.5708
    c: Tangent(g1,g2) = 1.5708
    c: Tangent(g2,g3) = 1.5708
    c: Tangent(g3,g4) = 1.5708
    c: Tangent(g4,g5) = 1.5708
    c: Tangent(g5,g6) = 1.5708
    c: Tangent(g6,g7) = 1.5708
    c: Tangent(g7,g0) = 1.5708
    c: Horizontal(g3)
    c: Vertical(g1)
    c: Vertical(g5)
    c: Equal(g0,g2)
    c: Equal(g2,g4)
    c: Equal(g4,g6)
    c: PointOnObject(g9,g3)
    c: PointOnObject(g9,g5)
    c: DistanceX(g8,g9) = 531
    c: DistanceY(g8,g9) = 161
    c: Perpendicular(g10,g0) = 1.5708
    c: Perpendicular(g10,g4) = 4.71239
    c: Distance(g10) = 549
    c: Symmetric(g8,g9,g11)
    c: PointOnObject(g8,g7)
    c: Coincident(g11,g-1)
    c: Horizontal(g7)
    c: PointOnObject(g8,g1)
FEATURE [Sketcher::SketchObject] Sketch015
  FullyConstrained = true
  MapMode = 5
  Support = -> [XY_Plane005]
  sketch-geometry (11):
    g0: ArcOfCircle CenterX=-207.41 CenterY=-14.4104 CenterZ=0 NormalX=0 NormalY=0 NormalZ=1 AngleXU=0 Radius=52.5896 StartAngle=3.14159 EndAngle=4.71239
    g1: LineSegment StartX=-260 StartY=-14.4104 StartZ=0 EndX=-260 EndY=14.4104 EndZ=0
    g2: ArcOfCircle CenterX=-207.41 CenterY=14.4104 CenterZ=0 NormalX=0 NormalY=0 NormalZ=1 AngleXU=0 Radius=52.5896 StartAngle=1.5708 EndAngle=3.14159
    g3: LineSegment StartX=-207.41 StartY=67 StartZ=0 EndX=207.41 EndY=67 EndZ=0
    g4: ArcOfCircle CenterX=207.41 CenterY=14.4104 CenterZ=0 NormalX=0 NormalY=0 NormalZ=1 AngleXU=0 Radius=52.5896 StartAngle=1e-16 EndAngle=1.5708
    g5: LineSegment StartX=260 StartY=14.4104 StartZ=0 EndX=260 EndY=-14.4104 EndZ=0
    g6: ArcOfCircle CenterX=207.41 CenterY=-14.4104 CenterZ=0 NormalX=0 NormalY=0 NormalZ=1 AngleXU=0 Radius=52.5896 StartAngle=4.71239 EndAngle=6.28319
    g7: LineSegment StartX=207.41 StartY=-67 StartZ=0 EndX=-207.41 EndY=-67 EndZ=0
    g8: GeomPoint X=-260 Y=-67 Z=0
    g9: GeomPoint X=260 Y=67 Z=0
    g10: LineSegment StartX=-259.874 StartY=-18.0555 StartZ=0 EndX=259.874 EndY=18.0555 EndZ=0
  constraints (25):
    c: Tangent(g0,g1) = 1.5708
    c: Tangent(g1,g2) = 1.5708
    c: Tangent(g2,g3) = 1.5708
    c: Tangent(g3,g4) = 1.5708
    c: Tangent(g4,g5) = 1.5708
    c: Tangent(g5,g6) = 1.5708
    c: Tangent(g6,g7) = 1.5708
    c: Tangent(g7,g0) = 1.5708
    c: Horizontal(g3)
    c: Horizontal(g7)
    c: Vertical(g1)
    c: Vertical(g5)
    c: Equal(g0,g2)
    c: Equal(g2,g4)
    c: Equal(g4,g6)
    c: PointOnObject(g8,g1)
    c: PointOnObject(g8,g7)
    c: PointOnObject(g9,g3)
    c: PointOnObject(g9,g5)
    c: Symmetric(g8,g9,g-1)
    c: DistanceX(g8,g9) = 520
    c: DistanceY(g8,g9) = 134
    c: Perpendicular(g10,g4) = 1.5708
    c: Perpendicular(g10,g0) = 4.71239
    c: Distance(g10) = 521
FEATURE [PartDesign::Body] Body005  label="basin"
  Group = -> [Sketch014,Sketch015]
  Origin = -> Origin005
  Placement = pos=(0,43,0) rot=(0,0,1;0rad)
FEATURE [PartDesign::SubShapeBinder] Binder014
  BindCopyOnChange = 0
  BindMode = 0
  ClaimChildren = true
  Context = -> Part [Body006.Binder014.]
  Fuse = false
  MakeFace = true
  OffsetFill = false
  OffsetIntersection = false
  OffsetJoinType = 0
  OffsetOpenResult = false
  PartialLoad = false
  Relative = true
  Support = -> [Body001[Pocket.Sketch003.]]
  _Version = 2
FEATURE [Sketcher::SketchObject] Sketch016
  ExternalGeometry = -> [Binder014]
  FullyConstrained = true
  MapMode = 5
  Support = -> [XY_Plane006]
  sketch-geometry (8):
    g0: LineSegment StartX=282.165 StartY=128.763 StartZ=0 EndX=287.147 EndY=134.115 EndZ=0
    g1: LineSegment StartX=0 StartY=120.796 StartZ=0 EndX=263.866 EndY=120.796 EndZ=0
    g2: LineSegment StartX=286.415 StartY=135.796 StartZ=0 EndX=0 EndY=135.796 EndZ=0
    g3: LineSegment StartX=0 StartY=120.796 StartZ=0 EndX=0 EndY=135.796 EndZ=0
    g4: ArcOfCircle CenterX=286.415 CenterY=134.796 CenterZ=0 NormalX=0 NormalY=0 NormalZ=1 AngleXU=0 Radius=1 StartAngle=5.53361 EndAngle=7.85398
    g5: GeomPoint X=288.712 Y=135.796 Z=0
    g6: ArcOfCircle CenterX=263.866 CenterY=145.796 CenterZ=0 NormalX=0 NormalY=0 NormalZ=1 AngleXU=0 Radius=25 StartAngle=4.71239 EndAngle=5.53361
    g7: GeomPoint X=274.75 Y=120.796 Z=0
  constraints (20):
    c: Parallel(g0,g-3)
    c: DistanceY(g-3,g5) = 1
    c: PointOnObject(g2,g-2)
    c: Coincident(g3,g1)
    c: Coincident(g3,g2)
    c: PointOnObject(g1,g-2)
    c: PointOnObject(g5,g0)
    c: PointOnObject(g5,g2)
    c: Tangent(g0,g4) = -1.5708
    c: Tangent(g2,g4) = -1.5708
    c: PointOnObject(g7,g0)
    c: PointOnObject(g7,g1)
    c: Tangent(g0,g6) = -1.5708
    c: Tangent(g1,g6) = -1.5708
    c: Distance(g5,g-3) = 1
    c: Horizontal(g2)
    c: Horizontal(g1)
    c: Radius(g4) = 1
    c: DistanceY(g3,g3) = 15
    c: Radius(g6) = 25
FEATURE [PartDesign::Pad] Pad001
  Direction = (0,0,1)
  Length = 3
  Length2 = 10
  Profile = -> Sketch016
  ReferenceAxis = -> Sketch016 [N_Axis]
  Type = 0
FEATURE [PartDesign::SubShapeBinder] Binder015
  BindCopyOnChange = 0
  BindMode = 0
  ClaimChildren = false
  Context = -> Part [Body006.Binder015.]
  Fuse = false
  MakeFace = true
  OffsetFill = false
  OffsetIntersection = false
  OffsetJoinType = 0
  OffsetOpenResult = false
  PartialLoad = false
  Relative = true
  Support = -> [Body001[Pocket011.Sketch017.]]
  _Version = 2
FEATURE [PartDesign::Pocket] Pocket012
  BaseFeature = -> Pad001
  Direction = (0,-2.7e-15,-1)
  Length = 5
  Length2 = 5
  Profile = -> Binder015
  Reversed = true
  Type = 0
FEATURE [PartDesign::Mirrored] Mirrored003
  BaseFeature = -> Pocket012
  MirrorPlane = -> Sketch016 [V_Axis]
  Originals = -> [Pad001,Pocket012]
  Refine = true
FEATURE [PartDesign::Body] Body006  label="sink_hand"
  Group = -> [Binder014,Sketch016,Pad001,Pocket012,Mirrored003,Binder015]
  Origin = -> Origin006
  Placement = pos=(0,-0.0522642,0.497261) rot=(1,0,0;0.10472rad)
  Tip = -> Mirrored003
  expr: Placement = placement(vector(0; 0; 0); rotation(0; 0; 6)) * placement(vector(0; 0; 0.5); rotation(0; 0; 0))
FEATURE [PartDesign::SubShapeBinder] Binder016
  BindCopyOnChange = 0
  BindMode = 0
  ClaimChildren = false
  Context = -> Part002 [Part001.Body007.Binder016.]
  Fuse = false
  MakeFace = true
  OffsetFill = false
  OffsetIntersection = false
  OffsetJoinType = 0
  OffsetOpenResult = false
  PartialLoad = false
  Relative = true
  Support = -> [Body[BaseBend.Sketch.]]
  _Version = 2
FEATURE [Sketcher::SketchObject] Sketch018  label="cap_base_sketch"
  ExternalGeometry = -> [Binder016]
  FullyConstrained = true
  MapMode = 5
  Support = -> [XY_Plane008]
  sketch-geometry (4):
    g0: LineSegment StartX=300.084 StartY=-41 StartZ=0 EndX=300.084 EndY=163.877 EndZ=0
    g1: LineSegment StartX=300.084 StartY=163.877 StartZ=0 EndX=-300.084 EndY=163.877 EndZ=0
    g2: LineSegment StartX=-300.084 StartY=163.877 StartZ=0 EndX=-300.084 EndY=-41 EndZ=0
    g3: GeomPoint X=205.016 Y=160.377 Z=0
  constraints (12):
    c: Coincident(g2,g1)
    c: DistanceX(g1,g1) = 600.168  'width'
    c: DistanceY(g0,g0) = 204.877  'length'
    c: Symmetric(g0,g2,g-2)
    c: Vertical(g2)
    c: Horizontal(g1)
    c: Coincident(g0,g-3)
    c: Coincident(g1,g0)
    c: Vertical(g0)
    c: DistanceX(g3) = 205.016
    c: DistanceY(g3) = 160.377
    c: DistanceY(g3,g0) = 3.5
FEATURE [PartDesign::FeaturePython] BaseBend004  label="cap_BaseBend"  # WARN: FeaturePython — macro-defined, semantics opaque (R4)
  BendSide = 1
  BendSketch = -> Sketch018
  MidPlane = false
  Reverse = false
  length = 50
  radius = 0.1
  thickness = 0.3
FEATURE [PartDesign::FeaturePython] Bend002  # WARN: FeaturePython — macro-defined, semantics opaque (R4)
  AutoMiter = false
  BaseFeature = -> BaseBend004
  BendType = 0
  LengthList = [204.877]
  LengthSpec = 1
  ReliefFactor = 0.7
  UseReliefFactor = false
  angle = 90
  baseObject = -> BaseBend004 [Edge29,Edge14,Edge43]
  bendAList = [90]
  extend1 = 0
  extend2 = 0
  gap1 = 0
  gap2 = 0
  invert = false
  kfactor = 0.5
  length = 204.877
  maxExtendDist = 5
  minGap = 0.1
  minReliefGap = 1
  miterangle1 = 0
  miterangle2 = 0
  offset = 0
  radius = 0.1
  reliefType = 0
  reliefd = 1
  reliefw = 0.8
  sketchflip = false
  sketchinvert = false
  unfold = false
  expr: baseObject = tuple(BaseBend004._self; list(<<Edge29>>; <<Edge14>>; <<Edge43>>))
  expr: length = Sketch018.Constraints.length
  expr: radius = BaseBend.radius
FEATURE [Sketcher::SketchObject] Sketch020
  AttachmentOffset = pos=(0,0,50) rot=(0,0,1;0rad)
  ExternalGeometry = -> [Sketch018]
  FullyConstrained = true
  MapMode = 5
  Placement = pos=(0,0,50) rot=(0,0,1;0rad)
  Support = -> [XY_Plane008]
  expr: .AttachmentOffset.Base.z = BaseBend004.length
  sketch-geometry (13):
    g0: LineSegment StartX=197.616 StartY=61.4797 StartZ=0 EndX=197.616 EndY=-41 EndZ=0
    g1: LineSegment StartX=197.616 StartY=-41 StartZ=0 EndX=197.716 EndY=-41 EndZ=0
    g2: LineSegment StartX=197.716 StartY=-41 StartZ=0 EndX=197.716 EndY=61.4383 EndZ=0
    g3: LineSegment StartX=197.716 StartY=61.4383 StartZ=0 EndX=299.684 EndY=163.406 EndZ=0
    g4: LineSegment StartX=299.684 StartY=163.406 StartZ=0 EndX=300.084 EndY=163.406 EndZ=0
    g5: LineSegment StartX=300.084 StartY=163.406 StartZ=0 EndX=300.084 EndY=163.877 EndZ=0
    g6: LineSegment StartX=300.084 StartY=163.877 StartZ=0 EndX=299.613 EndY=163.877 EndZ=0
    g7: LineSegment StartX=299.613 StartY=163.877 StartZ=0 EndX=299.613 EndY=163.477 EndZ=0
    g8: LineSegment StartX=299.613 StartY=163.477 StartZ=0 EndX=197.616 EndY=61.4797 EndZ=0
    g9: LineSegment StartX=197.616 StartY=61.4383 StartZ=0 EndX=197.716 EndY=61.4383 EndZ=0
    g10: LineSegment StartX=197.716 StartY=61.4383 StartZ=0 EndX=197.646 EndY=61.509 EndZ=0
    g11: LineSegment StartX=299.613 StartY=163.477 StartZ=0 EndX=299.684 EndY=163.406 EndZ=0
    g12: LineSegment StartX=197.716 StartY=61.4383 StartZ=0 EndX=197.716 EndY=163.877 EndZ=0
  constraints (37):
    c: Vertical(g0)
    c: Coincident(g0,g1)
    c: Horizontal(g1)
    c: Coincident(g1,g2)
    c: Coincident(g2,g3)
    c: Coincident(g3,g4)
    c: PointOnObject(g4,g-3)
    c: Coincident(g4,g5)
    c: Coincident(g5,g-3)
    c: Coincident(g5,g6)
    c: Coincident(g6,g7)
    c: Coincident(g7,g8)
    c: Vertical(g2)
    c: Parallel(g3,g8)
    c: Equal(g4,g7)
    c: DistanceX(g4,g4) = 0.4
    c: Coincident(g8,g0)
    c: PointOnObject(g9,g0)
    c: Coincident(g9,g2)
    c: Coincident(g9,g10)
    c: PointOnObject(g10,g8)
    c: Equal(g9,g10)
    c: Angle(g3) = 0.785398
    c: Horizontal(g1,g-3)
    c: DistanceX(g9,g9) = 0.1
    c: Coincident(g11,g7)
    c: Coincident(g11,g3)
    c: Coincident(g12,g2)
    c: Vertical(g12)
    c: Horizontal(g12,g5)
    c: Equal(g12,g2)
    c: Horizontal(g6)
    c: Perpendicular(g3,g10)
    c: Vertical(g7)
    c: Horizontal(g4)
    c: Perpendicular(g3,g11)
    c: Equal(g11,g1)
FEATURE [PartDesign::Pocket] Pocket014
  BaseFeature = -> Bend002
  Direction = (0,0,-1)
  Length = 5
  Length2 = 5
  Profile = -> Sketch020
  ReferenceAxis = -> Sketch020 [N_Axis]
  Reversed = true
  Type = 0
FEATURE [PartDesign::FeaturePython] Extend  # WARN: FeaturePython — macro-defined, semantics opaque (R4)
  BaseFeature = -> BaseBend003
  Offset = 0.02
  Refine = true
  UseSubtraction = false
  baseObject = -> BaseBend003 [Face12]
  gap1 = 0
  gap2 = 0
  length = 50.4
  expr: length = <<cap_BaseBend>>.length + 0.4 mm
FEATURE [App::Link] Link003  label="Body"
  LinkedObject = -> <external UST-E32 WHITE 2M.FCStd>#Body
FEATURE [Sketcher::SketchObject] Sketch021
  FullyConstrained = true
  MapMode = 5
  Placement = pos=(0,0,0) rot=(0.57735,0.57735,0.57735;2.0944rad)
  Support = -> [YZ_Plane009]
  sketch-geometry (5):
    g0: LineSegment StartX=27 StartY=0 StartZ=0 EndX=15 EndY=0 EndZ=0
    g1: LineSegment StartX=15 StartY=0 StartZ=0 EndX=15 EndY=16 EndZ=0
    g2: LineSegment StartX=15 StartY=16 StartZ=0 EndX=-15 EndY=16 EndZ=0
    g3: LineSegment StartX=-15 StartY=16 StartZ=0 EndX=-15 EndY=0 EndZ=0
    g4: LineSegment StartX=-15 StartY=0 StartZ=0 EndX=-27 EndY=0 EndZ=0
  constraints (15):
    c: PointOnObject(g0,g-1)
    c: PointOnObject(g0,g-1)
    c: Coincident(g0,g1)
    c: Vertical(g1)
    c: Coincident(g1,g2)
    c: PointOnObject(g3,g-1)
    c: Vertical(g3)
    c: Coincident(g3,g4)
    c: PointOnObject(g4,g-1)
    c: Symmetric(g2,g1,g-2)
    c: Coincident(g3,g2)
    c: DistanceX(g2,g2) = 30
    c: DistanceY(g1,g1) = 16  'height'
    c: Equal(g0,g4)
    c: DistanceX(g0,g0) = 12
FEATURE [PartDesign::FeaturePython] BaseBend005  # WARN: FeaturePython — macro-defined, semantics opaque (R4)
  BendSide = 0
  BendSketch = -> Sketch021
  MidPlane = true
  Reverse = false
  length = 115
  radius = 0.1
  thickness = 0.3
FEATURE [PartDesign::FeaturePython] Bend004  # WARN: FeaturePython — macro-defined, semantics opaque (R4)
  AutoMiter = true
  BaseFeature = -> BaseBend005
  BendType = 0
  LengthList = [16]
  LengthSpec = 1
  ReliefFactor = 0.7
  UseReliefFactor = false
  angle = 90
  baseObject = -> BaseBend005 [Edge45,Edge42]
  bendAList = [90]
  extend1 = 0
  extend2 = 0
  gap1 = 0
  gap2 = 0
  invert = false
  kfactor = 0.5
  length = 16
  maxExtendDist = 5
  minGap = 0.1
  minReliefGap = 1
  miterangle1 = 0
  miterangle2 = 0
  offset = 0
  radius = 0.1
  reliefType = 0
  reliefd = 1
  reliefw = 0.8
  sketchflip = false
  sketchinvert = false
  unfold = false
  expr: baseObject = tuple(BaseBend005._self; list(<<Edge45>>; <<Edge42>>))
  expr: length = Sketch021.Constraints.height
  expr: radius = BaseBend005.radius
FEATURE [Sketcher::SketchObject] Sketch022
  ExternalGeometry = -> [Sketch021]
  FullyConstrained = true
  MapMode = 5
  Support = -> [XY_Plane009]
  sketch-geometry (10):
    g0: LineSegment StartX=-35 StartY=-20.7 StartZ=0 EndX=-35 EndY=20.7 EndZ=0
    g1: LineSegment StartX=-35 StartY=20.7 StartZ=0 EndX=35 EndY=20.7 EndZ=0
    g2: LineSegment StartX=35 StartY=20.7 StartZ=0 EndX=35 EndY=-20.7 EndZ=0
    g3: LineSegment StartX=35 StartY=-20.7 StartZ=0 EndX=-35 EndY=-20.7 EndZ=0
    g4: GeomPoint X=0 Y=0 Z=0
    g5: Circle CenterX=35 CenterY=20.7 CenterZ=0 NormalX=0 NormalY=0 NormalZ=1 AngleXU=0 Radius=1.7
    g6: Circle CenterX=35 CenterY=-20.7 CenterZ=0 NormalX=0 NormalY=0 NormalZ=1 AngleXU=0 Radius=1.7
    g7: Circle CenterX=-35 CenterY=-20.7 CenterZ=0 NormalX=0 NormalY=0 NormalZ=1 AngleXU=0 Radius=1.7
    g8: Circle CenterX=-35 CenterY=20.7 CenterZ=0 NormalX=0 NormalY=0 NormalZ=1 AngleXU=0 Radius=1.7
    g9: GeomPoint X=35 Y=19 Z=0
  constraints (22):
    c: Coincident(g0,g1)
    c: Coincident(g1,g2)
    c: Coincident(g2,g3)
    c: Coincident(g3,g0)
    c: Horizontal(g1)
    c: Horizontal(g3)
    c: Vertical(g0)
    c: Vertical(g2)
    c: Symmetric(g1,g0,g4)
    c: Coincident(g4,g-1)
    c: Coincident(g6,g2)
    c: Coincident(g7,g0)
    c: Coincident(g8,g0)
    c: Coincident(g5,g1)
    c: Equal(g5,g8)
    c: Equal(g5,g7)
    c: Equal(g5,g6)
    c: Diameter(g5) = 3.4
    c: PointOnObject(g9,g2)
    c: PointOnObject(g9,g5)
    c: DistanceY(g-3,g9) = 4
    c: DistanceX(g1,g1) = 70
FEATURE [PartDesign::Pocket] Pocket016
  BaseFeature = -> Bend004
  Direction = (0,0,-1)
  Length = 5
  Length2 = 5
  Profile = -> Sketch022
  ReferenceAxis = -> Sketch022 [N_Axis]
  Reversed = true
  Type = 0
FEATURE [Sketcher::SketchObject] Sketch023
  AttachmentOffset = pos=(0,10,15) rot=(0,0,1;0rad)
  FullyConstrained = false
  MapMode = 5
  Placement = pos=(0,-15,10) rot=(1,0,0;1.5708rad)
  Support = -> [XZ_Plane009]
  sketch-geometry (8):
    g0: ArcOfCircle CenterX=47.5 CenterY=0 CenterZ=0 NormalX=0 NormalY=0 NormalZ=1 AngleXU=0 Radius=2.75 StartAngle=1.5708 EndAngle=4.71239
    g1: ArcOfCircle CenterX=86.6111 CenterY=0 CenterZ=0 NormalX=0 NormalY=0 NormalZ=1 AngleXU=0 Radius=2.75 StartAngle=4.71239 EndAngle=7.85398
    g2: LineSegment StartX=47.5 StartY=-2.75 StartZ=0 EndX=86.6111 EndY=-2.75 EndZ=0
    g3: LineSegment StartX=86.6111 StartY=2.75 StartZ=0 EndX=47.5 EndY=2.75 EndZ=0
    g4: ArcOfCircle CenterX=-47.5 CenterY=0 CenterZ=0 NormalX=0 NormalY=0 NormalZ=1 AngleXU=0 Radius=2.75 StartAngle=4.71239 EndAngle=7.85398
    g5: ArcOfCircle CenterX=-86.6111 CenterY=0 CenterZ=0 NormalX=0 NormalY=0 NormalZ=1 AngleXU=0 Radius=2.75 StartAngle=1.5708 EndAngle=4.71239
    g6: LineSegment StartX=-47.5 StartY=2.75 StartZ=0 EndX=-86.6111 EndY=2.75 EndZ=0
    g7: LineSegment StartX=-86.6111 StartY=-2.75 StartZ=0 EndX=-47.5 EndY=-2.75 EndZ=0
  constraints (17):
    c: Tangent(g0,g2) = -1.5708
    c: Tangent(g2,g1) = -1.5708
    c: Tangent(g1,g3) = -1.5708
    c: Tangent(g3,g0) = -1.5708
    c: Equal(g0,g1)
    c: PointOnObject(g0,g-1)
    c: PointOnObject(g1,g-1)
    c: Tangent(g4,g6) = -1.5708
    c: Tangent(g6,g5) = -1.5708
    c: Tangent(g5,g7) = -1.5708
    c: Tangent(g7,g4) = -1.5708
    c: Equal(g4,g5)
    c: Equal(g4,g0)
    c: Symmetric(g4,g0,g-2)
    c: Symmetric(g5,g1,g-2)
    c: Diameter(g0) = 5.5
    c: DistanceX(g4,g0) = 95
FEATURE [PartDesign::Pocket] Pocket018
  BaseFeature = -> Pocket016
  Direction = (0,1,-2e-16)
  Length = 5
  Length2 = 5
  Profile = -> Sketch023
  ReferenceAxis = -> Sketch023 [N_Axis]
  Reversed = true
  Type = 0
FEATURE [PartDesign::Body] Body008  label="Body008_material_0.30ansi"
  Group = -> [Sketch021,BaseBend005,Bend004,Sketch022,Pocket016,Sketch023,Pocket018]
  Origin = -> Origin009
  Tip = -> Pocket018
FEATURE [PartDesign::SubShapeBinder] Binder019
  BindCopyOnChange = 0
  BindMode = 0
  ClaimChildren = false
  Context = -> Body009 [Binder019.]
  Fuse = false
  MakeFace = true
  OffsetFill = false
  OffsetIntersection = false
  OffsetJoinType = 0
  OffsetOpenResult = false
  PartialLoad = false
  Relative = false
  Support = -> [Body007[Pocket013.Sketch019.]]
  _Version = 2
FEATURE [Sketcher::SketchObject] Sketch024
  ExternalGeometry = -> [Binder019]
  FullyConstrained = true
  MapMode = 5
  Support = -> [XY_Plane010]
  sketch-geometry (12):
    g0: ArcOfCircle CenterX=187.646 CenterY=27.2962 CenterZ=0 NormalX=0 NormalY=0 NormalZ=1 AngleXU=0 Radius=7 StartAngle=3.14159 EndAngle=4.71239
    g1: ArcOfCircle CenterX=207.646 CenterY=27.2962 CenterZ=0 NormalX=0 NormalY=0 NormalZ=1 AngleXU=0 Radius=7 StartAngle=4.71239 EndAngle=6.28319
    g2: ArcOfCircle CenterX=228.859 CenterY=78.5094 CenterZ=0 NormalX=0 NormalY=0 NormalZ=1 AngleXU=0 Radius=7 StartAngle=5.49779 EndAngle=7.06858
    g3: LineSegment StartX=233.808 StartY=73.5596 StartZ=0 EndX=216.696 EndY=56.4469 EndZ=0
    g4: LineSegment StartX=180.646 StartY=27.2962 StartZ=0 EndX=180.646 EndY=68.48 EndZ=0
    g5: LineSegment StartX=180.646 StartY=68.48 StartZ=0 EndX=209.767 EndY=97.6013 EndZ=0
    g6: LineSegment StartX=207.646 StartY=20.2962 StartZ=0 EndX=187.646 EndY=20.2962 EndZ=0
    g7: LineSegment StartX=214.646 StartY=27.2962 StartZ=0 EndX=214.646 EndY=51.4972 EndZ=0
    g8: LineSegment StartX=219.666 StartY=97.6013 StartZ=0 EndX=233.808 EndY=83.4591 EndZ=0
    g9: ArcOfCircle CenterX=214.717 CenterY=92.6515 CenterZ=0 NormalX=0 NormalY=0 NormalZ=1 AngleXU=0 Radius=7 StartAngle=0.785398 EndAngle=2.35619
    g10: GeomPoint X=214.646 Y=102.622 Z=0
    g11: ArcOfCircle CenterX=221.646 CenterY=51.4972 CenterZ=0 NormalX=0 NormalY=0 NormalZ=1 AngleXU=0 Radius=7 StartAngle=2.35619 EndAngle=3.14159
  constraints (26):
    c: Coincident(g0,g-3)
    c: Coincident(g1,g-5)
    c: Coincident(g2,g-4)
    c: Vertical(g4)
    c: Coincident(g5,g4)
    c: Vertical(g7)
    c: Tangent(g3,g2) = 1.5708
    c: Tangent(g8,g2) = 1.5708
    c: Equal(g1,g0)
    c: Radius(g2) = 7
    c: Perpendicular(g8,g3)
    c: PointOnObject(g10,g7)
    c: PointOnObject(g10,g8)
    c: Tangent(g8,g9) = 1.5708
    c: Equal(g1,g9)
    c: Tangent(g1,g7) = -1.5708
    c: Tangent(g1,g6) = 1.5708
    c: Tangent(g11,g7) = 1.5708
    c: Tangent(g11,g3) = -1.5708
    c: Tangent(g0,g6) = 1.5708
    c: Tangent(g0,g4) = 1.5708
    c: Tangent(g5,g9) = 1.5708
    c: Equal(g0,g2)
    c: Coincident(g9,g-6)
    c: Perpendicular(g5,g8)
    c: Equal(g11,g2)
FEATURE [PartDesign::Pad] Pad002
  Direction = (0,0,1)
  Length = 3
  Length2 = 10
  Profile = -> Sketch024
  ReferenceAxis = -> Sketch024 [N_Axis]
  Type = 0
FEATURE [PartDesign::Pocket] Pocket019
  BaseFeature = -> Pad002
  Direction = (0,0,-1)
  Length = 5
  Length2 = 5
  Profile = -> Binder019
  Reversed = true
  Type = 0
FEATURE [PartDesign::Body] Body009  label="cap_inner"
  Group = -> [Binder019,Sketch024,Pad002,Pocket019]
  Origin = -> Origin010
  Placement = pos=(0,0,44) rot=(0,0,1;0rad)
  Tip = -> Pocket019
  expr: .Placement.Base.z = <<cap_BaseBend>>.length - composit_properties#<<Properties>>.thickness * 2
FEATURE [Part::FeaturePython] LinearArray004  # WARN: FeaturePython — macro-defined, semantics opaque (R4)
  Alignment = 0
  CellStart = A1
  Count = 2
  Dir = (0,0,1)
  DirIsDriven = true
  DistributionLaw = 0
  DrivenProperty = 1
  EndInclusive = true
  ExposePlacement = false
  GeneratorMode = 0
  MarkerShape = 1
  MarkerSize = 0
  NumElements = 2
  OrientMode = 0
  Point = (0,0,0)
  PointIsDriven = true
  Reverse = false
  SpanEnd = 50
  SpanStart = 0
  Step = 50
  Type = lattice2LinearArray.LinearArray
  VSGVersion = 1
  Values = 0.0 | 50.0
  ValuesSource = 2
  isLattice = 1
FEATURE [Part::FeaturePython] Populate012  label="Populate LinearArray004 with Compound004"  # WARN: FeaturePython — macro-defined, semantics opaque (R4)
  Copying = 0
  ExposePlacement = false
  MarkerShape = 1
  MarkerSize = 0
  NumElements = 0
  Object = -> Compound004
  OutputCompounding = 1
  PlacementsTo = -> LinearArray004
  Referencing = 0
  Type = lattice2PopulateCopies.LatticePopulateCopies
  isLattice = 0
FEATURE [Part::Compound] Compound002  label="sink_cut1"
  Links = -> [Populate012]
FEATURE [Sketcher::SketchObject] Sketch026
  ExternalGeometry = -> [Binder009,Sketch011]
  FullyConstrained = true
  MapMode = 5
  Support = -> [XY_Plane003]
  expr: Constraints[13] = <<top_BaseBend>>.length / 2
  sketch-geometry (18):
    g0: LineSegment StartX=172.627 StartY=-12 StartZ=0 EndX=172.627 EndY=-9 EndZ=0
    g1: LineSegment StartX=172.627 StartY=-9 StartZ=0 EndX=174.817 EndY=-11.05 EndZ=0
    g2: LineSegment StartX=172.627 StartY=-12 StartZ=0 EndX=173.928 EndY=-12 EndZ=0
    g3: LineSegment StartX=173.928 StartY=-12 StartZ=0 EndX=174.817 EndY=-11.05 EndZ=0
    g4: LineSegment StartX=0 StartY=-100 StartZ=0 EndX=290.084 EndY=-100 EndZ=0
    g5: LineSegment StartX=0 StartY=-100 StartZ=0 EndX=0 EndY=-12 EndZ=0
    g6: LineSegment StartX=0 StartY=-12 StartZ=0 EndX=0.2 EndY=-12 EndZ=0
    g7: LineSegment StartX=0.2 StartY=-12 StartZ=0 EndX=172.627 EndY=-12 EndZ=0
    g8: LineSegment StartX=287.084 StartY=113.292 StartZ=0 EndX=289.274 EndY=111.242 EndZ=0
    g9: LineSegment StartX=174.817 StartY=-11.05 StartZ=0 EndX=289.274 EndY=111.242 EndZ=0
    g10: LineSegment StartX=289.274 StartY=111.242 StartZ=0 EndX=290.084 EndY=112.107 EndZ=0
    g11: LineSegment StartX=290.084 StartY=112.107 StartZ=0 EndX=290.084 EndY=113.292 EndZ=0
    g12: LineSegment StartX=290.084 StartY=113.292 StartZ=0 EndX=290.084 EndY=131.058 EndZ=0
    g13: LineSegment StartX=290.084 StartY=131.058 StartZ=0 EndX=290.084 EndY=134.058 EndZ=0
    g14: LineSegment StartX=290.084 StartY=134.058 StartZ=0 EndX=300.084 EndY=134.058 EndZ=0
    g15: LineSegment StartX=300.084 StartY=134.058 StartZ=0 EndX=300.084 EndY=-100 EndZ=0
    g16: LineSegment StartX=300.084 StartY=-100 StartZ=0 EndX=290.084 EndY=-100 EndZ=0
    g17: LineSegment StartX=287.084 StartY=113.292 StartZ=0 EndX=290.084 EndY=113.292 EndZ=0
  constraints (52):
    c: DistanceY(g4) = -100
    c: Coincident(g2,g3)
    c: Vertical(g0)
    c: Coincident(g1,g0)
    c: Equal(g1,g0)
    c: DistanceY(g0,g0) = 3
    c: Coincident(g7,g2)
    c: Coincident(g3,g9)
    c: Perpendicular(g3,g1)
    c: Coincident(g3,g1)
    c: Coincident(g0,g7)
    c: Horizontal(g4)
    c: Vertical(g5)
    c: DistanceX(g4,g4) = 290.084
    c: Coincident(g4,g5)
    c: Coincident(g5,g6)
    c: PointOnObject(g6,g-2)
    c: Coincident(g6,g7)
    c: Parallel(g6,g2)
    c: Parallel(g7,g2)
    c: Horizontal(g6)
    c: DistanceX(g6) = 0.2
    c: Distance(g10,g-3) = 15
    c: DistanceY(g5) = -12
    c: Coincident(g9,g10)
    c: Parallel(g3,g9)
    c: Parallel(g3,g10)
    c: Parallel(g9,g-3)
    c: Perpendicular(g9,g8)
    c: Coincident(g9,g8)
    c: Coincident(g11,g10)
    c: Vertical(g11)
    c: Coincident(g12,g11)
    c: Vertical(g12)
    c: Coincident(g13,g12)
    c: Vertical(g13)
    c: Coincident(g14,g13)
    c: Horizontal(g14)
    c: Coincident(g15,g14)
    c: Vertical(g15)
    c: Coincident(g16,g15)
    c: Coincident(g16,g4)
    c: Horizontal(g16)
    c: DistanceX(g16,g16) = 10
    c: Vertical(g4,g10)
    c: Coincident(g17,g8)
    c: Coincident(g17,g11)
    c: Perpendicular(g11,g17)
    c: Equal(g8,g17)
    c: Equal(g17,g0)
    c: Equal(g13,g0)
    c: Horizontal(g13,g-3)
FEATURE [Sketcher::SketchObject] Sketch027
  FullyConstrained = true
  MapMode = 5
  Support = -> [XY_Plane003]
FEATURE [Sketcher::SketchObject] Sketch028
  ExternalGeometry = -> [Sketch018]
  FullyConstrained = true
  MapMode = 5
  Support = -> [XY_Plane008]
  sketch-geometry (3):
    g0: LineSegment StartX=300.084 StartY=163.877 StartZ=0 EndX=197.646 EndY=61.4383 EndZ=0
    g1: LineSegment StartX=197.646 StartY=61.4383 StartZ=0 EndX=197.646 EndY=-41 EndZ=0
    g2: LineSegment StartX=197.646 StartY=61.4383 StartZ=0 EndX=197.646 EndY=163.877 EndZ=0
  constraints (9):
    c: Coincident(g-3,g0)
    c: Coincident(g0,g1)
    c: Vertical(g1)
    c: Horizontal(g1,g-3)
    c: Angle(g0) = -2.35619
    c: Coincident(g2,g0)
    c: Vertical(g2)
    c: Horizontal(g2,g0)
    c: Equal(g2,g1)
FEATURE [Sketcher::SketchObject] Sketch019
  ExternalGeometry = -> [Sketch028]
  FullyConstrained = true
  MapMode = 5
  Support = -> [XY_Plane008]
  sketch-geometry (15):
    g0: Circle CenterX=207.646 CenterY=57.2962 CenterZ=0 NormalX=0 NormalY=0 NormalZ=1 AngleXU=0 Radius=1.7
    g1: Circle CenterX=228.859 CenterY=78.5094 CenterZ=0 NormalX=0 NormalY=0 NormalZ=1 AngleXU=0 Radius=1.7
    g2: Circle CenterX=214.717 CenterY=92.6515 CenterZ=0 NormalX=0 NormalY=0 NormalZ=1 AngleXU=0 Radius=1.7
    g3: Circle CenterX=187.646 CenterY=65.5805 CenterZ=0 NormalX=0 NormalY=0 NormalZ=1 AngleXU=0 Radius=1.7
    g4: Circle CenterX=187.646 CenterY=27.2962 CenterZ=0 NormalX=0 NormalY=0 NormalZ=1 AngleXU=0 Radius=1.7
    g5: Circle CenterX=207.646 CenterY=27.2962 CenterZ=0 NormalX=0 NormalY=0 NormalZ=1 AngleXU=0 Radius=1.7
    g6: LineSegment StartX=197.646 StartY=61.4383 StartZ=0 EndX=197.646 EndY=27.2962 EndZ=0
    g7: LineSegment StartX=187.646 StartY=27.2962 StartZ=0 EndX=207.646 EndY=27.2962 EndZ=0
    g8: LineSegment StartX=207.646 StartY=27.2962 StartZ=0 EndX=207.646 EndY=57.2962 EndZ=0
    g9: LineSegment StartX=207.646 StartY=57.2962 StartZ=0 EndX=228.859 EndY=78.5094 EndZ=0
    g10: LineSegment StartX=228.859 StartY=78.5094 StartZ=0 EndX=214.717 EndY=92.6515 EndZ=0
    g11: LineSegment StartX=214.717 StartY=92.6515 StartZ=0 EndX=187.646 EndY=65.5805 EndZ=0
    g12: LineSegment StartX=187.646 StartY=65.5805 StartZ=0 EndX=187.646 EndY=27.2962 EndZ=0
    g13: LineSegment StartX=197.646 StartY=57.2962 StartZ=0 EndX=207.646 EndY=57.2962 EndZ=0
    g14: LineSegment StartX=207.646 StartY=57.2962 StartZ=0 EndX=200.574 EndY=64.3673 EndZ=0
  constraints (34):
    c: Symmetric(g1,g2,g-3)
    c: Coincident(g6,g-3)
    c: Vertical(g6)
    c: Symmetric(g4,g5,g6)
    c: Coincident(g7,g4)
    c: Coincident(g7,g5)
    c: Coincident(g7,g8)
    c: Coincident(g8,g0)
    c: Coincident(g8,g9)
    c: Coincident(g9,g1)
    c: Coincident(g9,g10)
    c: Coincident(g10,g2)
    c: Coincident(g10,g11)
    c: Coincident(g11,g3)
    c: Coincident(g11,g12)
    c: Coincident(g12,g7)
    c: Perpendicular(g11,g10)
    c: Perpendicular(g8,g7)
    c: Perpendicular(g12,g7)
    c: Perpendicular(g10,g9)
    c: Equal(g4,g5)
    c: Equal(g4, g0-g3) x4
    c: Diameter(g4) = 3.4
    c: DistanceX(g7,g7) = 20
    c: PointOnObject(g13,g6)
    c: Coincident(g13,g0)
    c: Horizontal(g13)
    c: Coincident(g13,g14)
    c: PointOnObject(g14,g-3)
    c: Perpendicular(g-3,g14)
    c: Equal(g13,g14)
    c: Equal(g8,g9)
    c: DistanceY(g8,g8) = 30
    c: PointOnObject(g6,g7)
FEATURE [PartDesign::Pocket] Pocket013
  BaseFeature = -> Pocket014
  Direction = (0,0,-1)
  Length = 5
  Length2 = 5
  Midplane = true
  Profile = -> Sketch019
  ReferenceAxis = -> Sketch019 [N_Axis]
  Type = 1
FEATURE [PartDesign::Mirrored] Mirrored004
  BaseFeature = -> Pocket013
  MirrorPlane = -> Sketch019 [V_Axis]
  Originals = -> [Pocket013,Pocket014]
  Refine = true
FEATURE [PartDesign::Body] Body007  label="cap_outer_material_0.30ansi"
  Group = -> [Binder016,Sketch018,BaseBend004,Bend002,Sketch019,Sketch020,Pocket014,Pocket013,Mirrored004,Sketch028]
  Origin = -> Origin008
  Tip = -> Mirrored004
FEATURE [App::Part] Part001  label="cap"
  Group = -> [Body009,Body007]
  Origin = -> Origin011
FEATURE [Sketcher::SketchObject] Sketch029
  FullyConstrained = true
  MapMode = 5
  Placement = pos=(0,0,0) rot=(1,0,0;1.5708rad)
  Support = -> [XZ_Plane003]
FEATURE [Sketcher::SketchObject] Sketch030
  FullyConstrained = true
  MapMode = 5
  Placement = pos=(0,0,0) rot=(1,0,0;1.5708rad)
  Support = -> [XZ_Plane]
  expr: Constraints[22] = BaseBend.radius
  expr: Constraints[23] = BaseBend.thickness
  expr: Constraints[30] = <<base_sketch>>.Constraints.outer_width
  sketch-geometry (18):
    g0: ArcOfCircle CenterX=299.684 CenterY=0 CenterZ=0 NormalX=0 NormalY=0 NormalZ=1 AngleXU=0 Radius=0.1 StartAngle=4.71239 EndAngle=6.28319
    g1: LineSegment StartX=299.784 StartY=-1e-16 StartZ=0 EndX=300.084 EndY=-1e-16 EndZ=0
    g2: ArcOfCircle CenterX=299.684 CenterY=0 CenterZ=0 NormalX=0 NormalY=0 NormalZ=1 AngleXU=0 Radius=0.4 StartAngle=4.71239 EndAngle=6.28319
    g3: ArcOfCircle CenterX=-299.684 CenterY=0 CenterZ=0 NormalX=0 NormalY=0 NormalZ=1 AngleXU=0 Radius=0.4 StartAngle=3.14159 EndAngle=4.71239
    g4: ArcOfCircle CenterX=-299.684 CenterY=0 CenterZ=0 NormalX=0 NormalY=0 NormalZ=1 AngleXU=0 Radius=0.1 StartAngle=3.14159 EndAngle=4.71239
    g5: LineSegment StartX=-300.084 StartY=0 StartZ=0 EndX=-299.784 EndY=0 EndZ=0
    g6: LineSegment StartX=-299.684 StartY=-0.4 StartZ=0 EndX=-285.084 EndY=-0.4 EndZ=0
    g7: LineSegment StartX=-299.684 StartY=-0.1 StartZ=0 EndX=-285.084 EndY=-0.1 EndZ=0
    g8: LineSegment StartX=-285.084 StartY=-0.4 StartZ=0 EndX=-285.084 EndY=-0.1 EndZ=0
    g9: LineSegment StartX=299.684 StartY=-0.1 StartZ=0 EndX=285.084 EndY=-0.1 EndZ=0
    g10: LineSegment StartX=285.084 StartY=-0.1 StartZ=0 EndX=285.084 EndY=-0.4 EndZ=0
    g11: LineSegment StartX=285.084 StartY=-0.4 StartZ=0 EndX=299.684 EndY=-0.4 EndZ=0
    g12: LineSegment StartX=300.084 StartY=-1e-16 StartZ=0 EndX=300.084 EndY=0.1 EndZ=0
    g13: LineSegment StartX=300.084 StartY=0.1 StartZ=0 EndX=299.784 EndY=0.1 EndZ=0
    g14: LineSegment StartX=299.784 StartY=0.1 StartZ=0 EndX=299.784 EndY=-1e-16 EndZ=0
    g15: LineSegment StartX=-299.784 StartY=0 StartZ=0 EndX=-299.784 EndY=0.1 EndZ=0
    g16: LineSegment StartX=-299.784 StartY=0.1 StartZ=0 EndX=-300.084 EndY=0.1 EndZ=0
    g17: LineSegment StartX=-300.084 StartY=0.1 StartZ=0 EndX=-300.084 EndY=0 EndZ=0
  constraints (46):
    c: PointOnObject(g0,g-1)
    c: Coincident(g1,g0)
    c: Coincident(g2,g0)
    c: Coincident(g2,g1)
    c: PointOnObject(g3,g-1)
    c: Coincident(g4,g3)
    c: Coincident(g5,g3)
    c: Coincident(g5,g4)
    c: Horizontal(g6)
    c: Horizontal(g7)
    c: Coincident(g8,g6)
    c: Coincident(g8,g7)
    c: Horizontal(g9)
    c: Coincident(g10,g9)
    c: Coincident(g11,g10)
    c: Horizontal(g11)
    c: Tangent(g11,g2) = -1.5708
    c: Tangent(g9,g0) = 1.5708
    c: Tangent(g7,g4) = -1.5708
    c: Tangent(g6,g3) = -1.5708
    c: Vertical(g8)
    c: Equal(g4,g0)
    c: Radius(g4) = 0.1
    c: DistanceY(g8,g8) = 0.3
    c: Perpendicular(g0,g1)
    c: Horizontal(g1)
    c: Symmetric(g3,g0,g-2)
    c: Horizontal(g5)
    c: Symmetric(g6,g10,g-2)
    c: Vertical(g10)
    c: DistanceX(g3,g1) = 600.168
    c: DistanceX(g10,g1) = 15
    c: Tangent(g2,g12) = -1.5708
    c: Coincident(g12,g13)
    c: Horizontal(g13)
    c: Coincident(g13,g14)
    c: Coincident(g14,g0)
    c: Tangent(g4,g15) = 1.5708
    c: Coincident(g15,g16)
    c: Coincident(g16,g17)
    c: Coincident(g17,g3)
    c: Vertical(g17)
    c: Horizontal(g16)
    c: Vertical(g14)
    c: Horizontal(g13,g15)
    c: DistanceY(g12,g12) = 0.1
FEATURE [Sketcher::SketchObject] Sketch031
  FullyConstrained = true
  MapMode = 5
  Support = -> [XY_Plane]
  expr: Constraints[18] = <<base_sketch>>.Constraints.outer_width - 20 mm
  sketch-geometry (9):
    g0: Circle CenterX=290.084 CenterY=115 CenterZ=0 NormalX=0 NormalY=0 NormalZ=1 AngleXU=0 Radius=1.7
    g1: Circle CenterX=290.084 CenterY=0 CenterZ=0 NormalX=0 NormalY=0 NormalZ=1 AngleXU=0 Radius=1.7
    g2: Circle CenterX=-290.084 CenterY=0 CenterZ=0 NormalX=0 NormalY=0 NormalZ=1 AngleXU=0 Radius=1.7
    g3: Circle CenterX=-290.084 CenterY=115 CenterZ=0 NormalX=0 NormalY=0 NormalZ=1 AngleXU=0 Radius=1.7
    g4: LineSegment StartX=-290.084 StartY=115 StartZ=0 EndX=-290.084 EndY=0 EndZ=0
    g5: LineSegment StartX=-290.084 StartY=0 StartZ=0 EndX=290.084 EndY=0 EndZ=0
    g6: LineSegment StartX=290.084 StartY=0 StartZ=0 EndX=290.084 EndY=115 EndZ=0
    g7: LineSegment StartX=290.084 StartY=115 StartZ=0 EndX=-290.084 EndY=115 EndZ=0
    g8: GeomPoint X=0 Y=57.5 Z=0
  constraints (21):
    c: Coincident(g4,g5)
    c: Coincident(g5,g6)
    c: Coincident(g6,g7)
    c: Coincident(g7,g4)
    c: Horizontal(g5)
    c: Horizontal(g7)
    c: Vertical(g4)
    c: Vertical(g6)
    c: Symmetric(g5,g4,g8)
    c: PointOnObject(g8,g-2)
    c: Coincident(g5,g1)
    c: Coincident(g0,g6)
    c: Coincident(g3,g4)
    c: Coincident(g2,g4)
    c: Equal(g2,g3)
    c: Equal(g2,g0)
    c: Equal(g2,g1)
    c: Diameter(g2) = 3.4
    c: DistanceX(g5,g5) = 580.168
    c: DistanceY(g-1,g1) = 0
    c: DistanceY(g6,g6) = 115
FEATURE [Part::Feature] Unfold
  Placement = pos=(0,0,0) rot=(1,0,0;1.5708rad)
  shape: bbox 684.1 x 219.8 x 0.552 mm, 54 faces (baked)
FEATURE [Sketcher::SketchObject] Unfold_Sketch
  FullyConstrained = false
  sketch-geometry (54):
    g0: LineSegment StartX=-340.951 StartY=82.6327 StartZ=0 EndX=-235.329 EndY=-49.8701 EndZ=0
    g1: ArcOfEllipse CenterX=-337.043 CenterY=85.7495 CenterZ=0 NormalX=0 NormalY=0 NormalZ=1 MajorRadius=4.99231 MinorRadius=4.99181 AngleXU=-1.67676 StartAngle=3.92041 EndAngle=5.49148
    g2: ArcOfEllipse CenterX=-231.412 CenterY=-46.6891 CenterZ=0 NormalX=0 NormalY=0 NormalZ=1 MajorRadius=5.03946 MinorRadius=5.03751 AngleXU=-1.68562 StartAngle=5.50911 EndAngle=7.06209
    g3: LineSegment StartX=-289.004 StartY=130.436 StartZ=0 EndX=-340.158 EndY=89.6591 EndZ=0
    g4: LineSegment StartX=-228.302 StartY=-50.6633 StartZ=0 EndX=-175.599 EndY=-8.65217 EndZ=0
    g5: BSplineCurve PolesCount=14 KnotsCount=5 Degree=4 IsPeriodic=0
    g6: ArcOfEllipse CenterX=-164.267 CenterY=-0.854159 CenterZ=0 NormalX=0 NormalY=0 NormalZ=1 MajorRadius=9.96021 MinorRadius=9.95915 AngleXU=-0.814441 StartAngle=3.96168 EndAngle=4.22122
    g7: ArcOfEllipse CenterX=-164.212 CenterY=-0.912903 CenterZ=0 NormalX=0 NormalY=0 NormalZ=1 MajorRadius=10.0002 MinorRadius=10 AngleXU=-0.821298 StartAngle=3.32739 EndAngle=3.9626
    g8: BSplineCurve PolesCount=15 KnotsCount=13 Degree=3 IsPeriodic=0
    g9: ArcOfCircle CenterX=-164.334 CenterY=-1.02174 CenterZ=0 NormalX=0 NormalY=0 NormalZ=1 AngleXU=3.14159 Radius=10 StartAngle=3.32742 EndAngle=5.27614
    g10: BSplineCurve PolesCount=15 KnotsCount=13 Degree=3 IsPeriodic=0
    g11: ArcOfCircle CenterX=-164.334 CenterY=-0.854191 CenterZ=0 NormalX=0 NormalY=0 NormalZ=1 AngleXU=3.14159 Radius=10 StartAngle=1.96813 EndAngle=2.94815
    g12: ArcOfCircle CenterX=-158.53 CenterY=-14.6857 CenterZ=0 NormalX=0 NormalY=0 NormalZ=1 AngleXU=-2e-16 Radius=5 StartAngle=1.96813 EndAngle=3.14159
    g13: LineSegment StartX=-163.53 StartY=-82 StartZ=0 EndX=-163.53 EndY=-14.6857 EndZ=0
    g14: ArcOfCircle CenterX=158.53 CenterY=-14.6857 CenterZ=0 NormalX=0 NormalY=0 NormalZ=1 AngleXU=3.14159 Radius=5 StartAngle=3.14159 EndAngle=4.31506
    g15: LineSegment StartX=163.53 StartY=-14.6857 StartZ=0 EndX=163.53 EndY=-82 EndZ=0
    g16: ArcOfCircle CenterX=164.334 CenterY=-0.854191 CenterZ=0 NormalX=0 NormalY=0 NormalZ=1 AngleXU=-1e-16 Radius=10 StartAngle=3.33503 EndAngle=4.31506
    g17: LineSegment StartX=228.302 StartY=-50.6633 StartZ=0 EndX=175.599 EndY=-8.65217 EndZ=0
    g18: BSplineCurve PolesCount=14 KnotsCount=5 Degree=4 IsPeriodic=0
    g19: ArcOfEllipse CenterX=231.412 CenterY=-46.6891 CenterZ=0 NormalX=0 NormalY=0 NormalZ=1 MajorRadius=5.03946 MinorRadius=5.03751 AngleXU=-1.456 StartAngle=5.5043 EndAngle=7.05729
    g20: ArcOfEllipse CenterX=164.267 CenterY=-0.85416 CenterZ=0 NormalX=0 NormalY=0 NormalZ=1 MajorRadius=9.96021 MinorRadius=9.95915 AngleXU=-2.32718 StartAngle=2.062 EndAngle=2.32154
    g21: LineSegment StartX=340.951 StartY=82.6327 StartZ=0 EndX=235.329 EndY=-49.8701 EndZ=0
    g22: ArcOfEllipse CenterX=164.212 CenterY=-0.912891 CenterZ=0 NormalX=0 NormalY=0 NormalZ=1 MajorRadius=10.0002 MinorRadius=10 AngleXU=-2.32009 StartAngle=2.32038 EndAngle=2.95559
    g23: ArcOfEllipse CenterX=337.043 CenterY=85.7495 CenterZ=0 NormalX=0 NormalY=0 NormalZ=1 MajorRadius=4.99231 MinorRadius=4.99181 AngleXU=-1.46487 StartAngle=0.791731 EndAngle=2.36281
    g24: LineSegment StartX=289.004 StartY=130.436 StartZ=0 EndX=340.158 EndY=89.6591 EndZ=0
    g25: BSplineCurve PolesCount=15 KnotsCount=13 Degree=3 IsPeriodic=0
    g26: ArcOfCircle CenterX=164.334 CenterY=-1.02174 CenterZ=0 NormalX=0 NormalY=0 NormalZ=1 AngleXU=-1e-16 Radius=10 StartAngle=1.00704 EndAngle=2.95577
    g27: BSplineCurve PolesCount=15 KnotsCount=13 Degree=3 IsPeriodic=0
    g28: ArcOfCircle CenterX=158.53 CenterY=-82 CenterZ=0 NormalX=0 NormalY=0 NormalZ=1 AngleXU=-1.5708 Radius=5 StartAngle=5.8e-15 EndAngle=1.5708
    g29: LineSegment StartX=-158.53 StartY=-87 StartZ=0 EndX=158.53 EndY=-87 EndZ=0
    g30: ArcOfCircle CenterX=-158.53 CenterY=-82 CenterZ=0 NormalX=0 NormalY=0 NormalZ=1 AngleXU=-1.5708 Radius=5 StartAngle=4.71239 EndAngle=6.28319
    g31: LineSegment StartX=-286.415 StartY=132.846 StartZ=0 EndX=286.415 EndY=132.846 EndZ=0
    g32: Ellipse CenterX=86.6331 CenterY=125.846 CenterZ=0 NormalX=0 NormalY=0 NormalZ=-1 MajorRadius=1.7 MinorRadius=1.7 AngleXU=3.14158
    g33: Ellipse CenterX=-86.6331 CenterY=125.846 CenterZ=0 NormalX=0 NormalY=0 NormalZ=-1 MajorRadius=1.7 MinorRadius=1.7 AngleXU=3.14159
    g34: Circle CenterX=-1e-16 CenterY=-81 CenterZ=0 NormalX=0 NormalY=0 NormalZ=1 AngleXU=0 Radius=1.7
    g35: Circle CenterX=-1e-16 CenterY=-31 CenterZ=0 NormalX=0 NormalY=0 NormalZ=1 AngleXU=0 Radius=1.7
    g36: Ellipse CenterX=230.314 CenterY=-46.5346 CenterZ=0 NormalX=0 NormalY=0 NormalZ=1 MajorRadius=1.7 MinorRadius=1.7 AngleXU=1.67671
    g37: Ellipse CenterX=297.182 CenterY=117.565 CenterZ=0 NormalX=0 NormalY=0 NormalZ=1 MajorRadius=1.7 MinorRadius=1.7 AngleXU=1.67671
    g38: Ellipse CenterX=336.28 CenterY=86.3987 CenterZ=0 NormalX=0 NormalY=0 NormalZ=1 MajorRadius=1.7 MinorRadius=1.7 AngleXU=1.67671
    g39: Circle CenterX=-154.614 CenterY=-81 CenterZ=0 NormalX=0 NormalY=0 NormalZ=1 AngleXU=3.14159 Radius=1.7
    g40: Circle CenterX=154.614 CenterY=-81 CenterZ=0 NormalX=0 NormalY=0 NormalZ=1 AngleXU=0 Radius=1.7
    g41: Ellipse CenterX=-259.899 CenterY=125.846 CenterZ=0 NormalX=0 NormalY=0 NormalZ=-1 MajorRadius=1.7 MinorRadius=1.7 AngleXU=3.14159
    g42: Ellipse CenterX=259.899 CenterY=125.846 CenterZ=0 NormalX=0 NormalY=0 NormalZ=-1 MajorRadius=1.7 MinorRadius=1.7 AngleXU=3.14158
    g43: Ellipse CenterX=-336.28 CenterY=86.3987 CenterZ=0 NormalX=0 NormalY=0 NormalZ=1 MajorRadius=1.7 MinorRadius=1.7 AngleXU=-1.67673
    g44: Ellipse CenterX=-297.182 CenterY=117.565 CenterZ=0 NormalX=0 NormalY=0 NormalZ=1 MajorRadius=1.7 MinorRadius=1.7 AngleXU=-1.67673
    g45: Ellipse CenterX=-230.314 CenterY=-46.5346 CenterZ=0 NormalX=0 NormalY=0 NormalZ=1 MajorRadius=1.7 MinorRadius=1.7 AngleXU=-1.67673
    g46: Circle CenterX=154.614 CenterY=-31 CenterZ=0 NormalX=0 NormalY=0 NormalZ=1 AngleXU=0 Radius=1.7
    g47: Circle CenterX=-154.614 CenterY=-31 CenterZ=0 NormalX=0 NormalY=0 NormalZ=1 AngleXU=3.14159 Radius=1.7
    g48: Ellipse CenterX=191.216 CenterY=-15.3682 CenterZ=0 NormalX=0 NormalY=0 NormalZ=1 MajorRadius=1.7 MinorRadius=1.7 AngleXU=1.67671
    g49: Ellipse CenterX=-191.216 CenterY=-15.3682 CenterZ=0 NormalX=0 NormalY=0 NormalZ=1 MajorRadius=1.7 MinorRadius=1.7 AngleXU=-1.67673
    g50: LineSegment StartX=289 StartY=130.44 StartZ=0 EndX=289.004 EndY=130.436 EndZ=0
    g51: LineSegment StartX=289 StartY=130.44 StartZ=0 EndX=286.415 EndY=132.846 EndZ=0
    g52: LineSegment StartX=-289 StartY=130.44 StartZ=0 EndX=-286.415 EndY=132.846 EndZ=0
    g53: LineSegment StartX=-289 StartY=130.44 StartZ=0 EndX=-289.004 EndY=130.436 EndZ=0
FEATURE [Sketcher::SketchObject] Unfold_Sketch_Outline
  FullyConstrained = true
FEATURE [Sketcher::SketchObject] Unfold_Sketch_bends
  FullyConstrained = false
  sketch-geometry (3):
    g0: LineSegment StartX=-171.087 StartY=6.35397 StartZ=0 EndX=-287.707 EndY=131.643 EndZ=0
    g1: LineSegment StartX=171.087 StartY=6.35397 StartZ=0 EndX=287.707 EndY=131.643 EndZ=0
    g2: LineSegment StartX=154.334 StartY=-0.975351 StartZ=0 EndX=-154.334 EndY=-0.975351 EndZ=0
FEATURE [PartDesign::FeatureBase] BaseFeature
  BaseFeature = -> Unfold
  Placement = pos=(0,0,0) rot=(1,0,0;1.5708rad)
  expr: Placement = .BaseFeature.Placement
FEATURE [PartDesign::SubShapeBinder] Binder020
  BindCopyOnChange = 0
  BindMode = 0
  ClaimChildren = false
  Context = -> Body010 [Binder020.]
  Fuse = false
  MakeFace = true
  OffsetFill = false
  OffsetIntersection = false
  OffsetJoinType = 0
  OffsetOpenResult = false
  PartialLoad = false
  Relative = true
  Support = -> [Unfold_Sketch_bends]
  _Version = 2
FEATURE [Sketcher::SketchObject] Sketch032
  ExternalGeometry = -> [Binder020]
  FullyConstrained = true
  MapMode = 5
  Support = -> [XY_Plane012]
  sketch-geometry (3):
    g0: Circle CenterX=154.334 CenterY=-0.975351 CenterZ=0 NormalX=0 NormalY=0 NormalZ=1 AngleXU=0 Radius=1
    g1: Circle CenterX=171.087 CenterY=6.35397 CenterZ=0 NormalX=0 NormalY=0 NormalZ=1 AngleXU=0 Radius=1
    g2: Circle CenterX=287.707 CenterY=131.643 CenterZ=0 NormalX=0 NormalY=0 NormalZ=1 AngleXU=0 Radius=1
  constraints (6):
    c: Coincident(g0,g-4)
    c: Coincident(g1,g-3)
    c: Coincident(g2,g-3)
    c: Equal(g0,g1)
    c: Equal(g0,g2)
    c: Diameter(g0) = 2
FEATURE [PartDesign::Pocket] Pocket023
  BaseFeature = -> BaseFeature
  Direction = (0,0,-1)
  Length = 5
  Length2 = 5
  Placement = pos=(0,0,0) rot=(1,0,0;1.5708rad)
  Profile = -> Sketch032
  ReferenceAxis = -> Sketch032 [N_Axis]
  Reversed = true
  Type = 0
FEATURE [PartDesign::Mirrored] Mirrored006
  BaseFeature = -> Pocket023
  MirrorPlane = -> Sketch032 [V_Axis]
  Originals = -> [Pocket023]
  Placement = pos=(0,0,0) rot=(1,0,0;1.5708rad)
FEATURE [PartDesign::Body] Body010
  BaseFeature = -> Unfold
  Group = -> [BaseFeature,Sketch032,Binder020,Pocket023,Mirrored006]
  Origin = -> Origin012
  Tip = -> Mirrored006
FEATURE [TechDraw::DrawSVGTemplate] Template
  Height = 210
  Orientation = 1
  Template = <path>
  Width = 297
FEATURE [Sketcher::SketchObject] Sketch038
  AttachmentOffset = pos=(0,0,640) rot=(0,0,1;0rad)
  ExternalGeometry = -> [Binder001]
  FullyConstrained = true
  MapMode = 5
  Placement = pos=(0,0,640) rot=(0,0,1;0rad)
  Support = -> [XY_Plane]
  expr: .AttachmentOffset.Base.z = BaseBend.length
  expr: Constraints[0] = <<ULI-3865416>>#<<Properties>>.width + 3 mm
  expr: Constraints[13] = <<ULI-3865416>>#<<Properties>>.length / 2 + 1 mm
  sketch-geometry (6):
    g0: GeomPoint X=267.902 Y=110.358 Z=0
    g1: LineSegment StartX=268.194 StartY=110.085 StartZ=0 EndX=267.902 EndY=110.358 EndZ=0
    g2: LineSegment StartX=267.902 StartY=110.358 StartZ=0 EndX=281 EndY=124.352 EndZ=0
    g3: LineSegment StartX=281 StartY=124.352 StartZ=0 EndX=281.292 EndY=124.079 EndZ=0
    g4: LineSegment StartX=281.292 StartY=124.079 StartZ=0 EndX=268.194 EndY=110.085 EndZ=0
    g5: GeomPoint X=274.597 Y=117.218 Z=0
  constraints (14):
    c: DistanceY(g0,g-3) = 23.7
    c: PointOnObject(g2,g-3)
    c: PointOnObject(g0,g-3)
    c: Coincident(g1,g2)
    c: Coincident(g2,g3)
    c: Coincident(g3,g4)
    c: Coincident(g4,g1)
    c: Parallel(g2,g4)
    c: Symmetric(g2,g1,g5)
    c: Perpendicular(g1,g2)
    c: Coincident(g1,g0)
    c: Distance(g1) = 0.4
    c: Perpendicular(g4,g3)
    c: DistanceX(g2) = 281
FEATURE [PartDesign::CoordinateSystem] Local_CS001
  AttacherType = Attacher::AttachEngine3D
  AttachmentOffset = pos=(164.614,0,0) rot=(0.293211,-0.676028,-0.676028;2.57116rad)
  MapMode = 5
  Placement = pos=(164.614,0,0) rot=(0.293211,-0.676028,-0.676028;2.57116rad)
  Support = -> [XY_Plane]
  expr: .AttachmentOffset.Base.x = <<main_sketch>>.Constraints.inner_width / 2
  expr: .AttachmentOffset.Rotation.Yaw = -(180 deg - <<main_sketch>>.Constraints.angle)
FEATURE [Sketcher::SketchObject] Sketch039
  AttachmentOffset = pos=(0,110,0) rot=(0,0,1;0rad)
  ExternalGeometry = -> [Sketch009]
  FullyConstrained = true
  MapMode = 5
  Placement = pos=(164.614,5.5e-14,110) rot=(-0.293211,0.676028,0.676028;3.71203rad)
  Support = -> [Local_CS001]
  expr: .AttachmentOffset.Base.y = <<Pocket004>>.Length
  sketch-geometry (3):
    g0: LineSegment StartX=0 StartY=0 StartZ=0 EndX=-150.565 EndY=0 EndZ=0
    g1: LineSegment StartX=-150.565 StartY=0 StartZ=0 EndX=-150.565 EndY=11.5554 EndZ=0
    g2: LineSegment StartX=-150.565 StartY=11.5554 StartZ=0 EndX=0 EndY=0 EndZ=0
  constraints (8):
    c: Coincident(g-1,g0)
    c: PointOnObject(g0,g-1)
    c: Coincident(g0,g1)
    c: Vertical(g1)
    c: Coincident(g1,g2)
    c: Coincident(g2,g0)
    c: Vertical(g0,g-3)
    c: Angle(g2) = -0.0765971
FEATURE [Sketcher::SketchObject] Sketch040
  AttachmentOffset = pos=(0,110,0) rot=(0,0,1;0rad)
  ExternalGeometry = -> [Sketch039]
  FullyConstrained = true
  MapMode = 5
  Placement = pos=(164.614,5.5e-14,110) rot=(-0.293211,0.676028,0.676028;3.71203rad)
  Support = -> [Local_CS001]
  expr: AttachmentOffset = <<Sketch039>>.AttachmentOffset
  sketch-geometry (7):
    g0: ArcOfCircle CenterX=-1 CenterY=0 CenterZ=0 NormalX=0 NormalY=0 NormalZ=1 AngleXU=0 Radius=12 StartAngle=1.5708 EndAngle=2.76175
    g1: ArcOfCircle CenterX=-16.7883 CenterY=6.30316 CenterZ=0 NormalX=0 NormalY=0 NormalZ=1 AngleXU=0 Radius=5 StartAngle=4.63579 EndAngle=5.90334
    g2: LineSegment StartX=-17.1709 StartY=1.31782 StartZ=0 EndX=-17.1709 EndY=0 EndZ=0
    g3: LineSegment StartX=-17.1709 StartY=0 StartZ=0 EndX=0 EndY=0 EndZ=0
    g4: LineSegment StartX=0 StartY=0 StartZ=0 EndX=0 EndY=12 EndZ=0
    g5: LineSegment StartX=0 StartY=12 StartZ=0 EndX=-1 EndY=12 EndZ=0
    g6: LineSegment StartX=0 StartY=0 StartZ=0 EndX=-17.1709 EndY=1.31782 EndZ=0
  constraints (18):
    c: Coincident(g3,g4)
    c: Tangent(g1,g0) = 1.5708
    c: Radius(g1) = 5
    c: Radius(g0) = 12  'r'
    c: Coincident(g2,g3)
    c: PointOnObject(g2,g-1)
    c: Vertical(g2)
    c: Coincident(g2,g1)
    c: Coincident(g4,g5)
    c: Horizontal(g5)
    c: PointOnObject(g4,g-2)
    c: PointOnObject(g0,g-1)
    c: Tangent(g0,g5) = -1.5708
    c: DistanceX(g5,g5) = 1
    c: Coincident(g6,g3)
    c: Parallel(g6,g-3)
    c: Coincident(g3,g-1)
    c: Tangent(g1,g6) = 1.5708
FEATURE [Sketcher::SketchObject] Sketch041
  AttachmentOffset = pos=(0,110,0) rot=(0,1,0;-0.818478rad)
  FullyConstrained = true
  MapMode = 5
  Placement = pos=(164.614,5.5e-14,110) rot=(0,-0.707107,-0.707107;3.14159rad)
  Support = -> [Local_CS001]
  expr: .AttachmentOffset.Base.y = <<Sketch039>>.AttachmentOffset.Base.y
  expr: .AttachmentOffset.Rotation.Angle = -<<main_sketch>>.Constraints.angle
  expr: Constraints[12] = Sketch040.Constraints.r
  sketch-geometry (5):
    g0: LineSegment StartX=17.2481 StartY=6.67191e-11 StartZ=0 EndX=-5 EndY=0 EndZ=0
    g1: LineSegment StartX=-5 StartY=0 StartZ=0 EndX=-5 EndY=12 EndZ=0
    g2: LineSegment StartX=-5 StartY=12 StartZ=0 EndX=1 EndY=12 EndZ=0
    g3: ArcOfCircle CenterX=1 CenterY=0 CenterZ=0 NormalX=0 NormalY=0 NormalZ=1 AngleXU=0 Radius=12 StartAngle=0.298532 EndAngle=1.5708
    g4: ArcOfCircle CenterX=17.2481 CenterY=5 CenterZ=0 NormalX=0 NormalY=0 NormalZ=1 AngleXU=0 Radius=5 StartAngle=3.44012 EndAngle=4.71238
  constraints (15):
    c: PointOnObject(g0,g-1)
    c: PointOnObject(g0,g-1)
    c: Coincident(g0,g1)
    c: Vertical(g1)
    c: Coincident(g1,g2)
    c: Horizontal(g2)
    c: PointOnObject(g3,g-1)
    c: Tangent(g3,g2) = 1.5708
    c: Coincident(g4,g0)
    c: Tangent(g4,g3) = 1.5708
    c: Tangent(g4,g-1)
    c: DistanceX(g2) = 1
    c: Radius(g3) = 12
    c: DistanceX(g0) = -5
    c: Radius(g4) = 5
FEATURE [Sketcher::SketchObject] Sketch042
  FullyConstrained = true
  sketch-geometry (5):
    g0: LineSegment StartX=-1.75 StartY=50 StartZ=0 EndX=-1.75 EndY=0 EndZ=0
    g1: LineSegment StartX=-1.75 StartY=0 StartZ=0 EndX=1.75 EndY=0 EndZ=0
    g2: LineSegment StartX=1.75 StartY=0 StartZ=0 EndX=1.75 EndY=50 EndZ=0
    g3: LineSegment StartX=1.75 StartY=50 StartZ=0 EndX=-1.75 EndY=50 EndZ=0
    g4: GeomPoint X=0 Y=25 Z=0
  constraints (13):
    c: Coincident(g0,g1)
    c: Coincident(g1,g2)
    c: Coincident(g2,g3)
    c: Coincident(g3,g0)
    c: Horizontal(g1)
    c: Horizontal(g3)
    c: Vertical(g0)
    c: Vertical(g2)
    c: Symmetric(g1,g0,g4)
    c: PointOnObject(g4,g-2)
    c: PointOnObject(g1,g-1)
    c: DistanceX(g1,g1) = 3.5
    c: DistanceY(g2,g2) = 50
FEATURE [Part::FeaturePython] Populate013  label="Populate ArrayFilter with Sketch042"  # WARN: FeaturePython — macro-defined, semantics opaque (R4)
  Copying = 0
  ExposePlacement = false
  MarkerShape = 1
  MarkerSize = 0
  NumElements = 0
  Object = -> Sketch042
  OutputCompounding = 1
  PlacementsTo = -> ArrayFilter
  Referencing = 0
  Type = lattice2PopulateCopies.LatticePopulateCopies
  isLattice = 0
FEATURE [PartDesign::SubShapeBinder] Binder022
  BindCopyOnChange = 0
  BindMode = 0
  ClaimChildren = true
  Fuse = false
  MakeFace = true
  OffsetFill = false
  OffsetIntersection = false
  OffsetJoinType = 0
  OffsetOpenResult = false
  PartialLoad = false
  Relative = false
  Support = -> [Populate013]
  _Version = 2
FEATURE [PartDesign::Pocket] Pocket030
  BaseFeature = -> Pocket010
  Direction = (0,0,-1)
  Length = 1
  Length2 = 5
  Profile = -> Binder022
  Reversed = true
  Type = 0
FEATURE [PartDesign::Body] Body002  label="droppers_top_fix"
  Group = -> [Binder006,Pad,Binder007,Pocket005,Binder008,Pocket006,Binder013,Pocket010,Binder022,Pocket030]
  Origin = -> Origin002
  Placement = pos=(0,0,3) rot=(0,0,1;0rad)
  Tip = -> Pocket030
FEATURE [Part::Part2DObjectPython] Line002  # Draft 2D object (typed FeaturePython)
  Area = 0
  ChamferSize = 0
  Closed = false
  End = (-164.614,0,1)
  FilletRadius = 0
  Length = 329.23
  MakeFace = true
  Placement = pos=(0,0,-105) rot=(0.94131,-0.323415,-0.096634;0.894457rad)
  Points = (2) [(180.509,71.9679,18.9705),(-134.47,85.3935,113.84)]
  Start = (164.614,0,0)
  Subdivisions = 0
  expr: .End.x = -<<Line>>.Start.x
  expr: .End.y = <<Line>>.Start.y
  expr: .End.z = <<Line>>.Start.z + 1 mm
  expr: Start = <<Line>>.Start
FEATURE [Part::Part2DObjectPython] Line003  # Draft 2D object (typed FeaturePython)
  Area = 0
  ChamferSize = 0
  Closed = false
  End = (-290.084,134.058,15.8523)
  FilletRadius = 0
  Length = 184.214
  MakeFace = true
  Placement = pos=(0,0,0) rot=(0.94131,-0.323415,-0.096634;0.523599rad)
  Points = (2) [(-161.952,-0.764822,29.4927),(-295.231,123.319,1.6585)]
  Start = (-164.614,0,1)
  Subdivisions = 0
  expr: End = <<DatumPoint001>>.Placement.Base
  expr: Start = <<Line002>>.End
FEATURE [PartDesign::Point] DatumPoint
  AttacherType = Attacher::AttachEnginePoint
  MapMode = 40
  Placement = pos=(1e-16,1e-16,0.5) rot=(0,0,1;0rad)
  Support = -> [Z_Axis001,Line002]
FEATURE [Sketcher::SketchObject] Sketch043
  AttachmentOffset = pos=(0,0,290) rot=(0,0,1;0rad)
  FullyConstrained = true
  MapMode = 5
  Placement = pos=(290,0,0) rot=(0.57735,0.57735,0.57735;2.0944rad)
  Support = -> [YZ_Plane003]
  expr: Constraints[10] = <<main_sketch>>.Constraints.length
  sketch-geometry (5):
    g0: LineSegment StartX=124.058 StartY=0 StartZ=0 EndX=164.058 EndY=0 EndZ=0
    g1: LineSegment StartX=164.058 StartY=0 StartZ=0 EndX=164.058 EndY=30 EndZ=0
    g2: LineSegment StartX=164.058 StartY=30 StartZ=0 EndX=124.058 EndY=30 EndZ=0
    g3: LineSegment StartX=124.058 StartY=30 StartZ=0 EndX=124.058 EndY=0 EndZ=0
    g4: GeomPoint X=134.058 Y=0 Z=0
  constraints (14):
    c: Coincident(g0,g1)
    c: Coincident(g1,g2)
    c: Coincident(g2,g3)
    c: Coincident(g3,g0)
    c: Horizontal(g0)
    c: Horizontal(g2)
    c: Vertical(g1)
    c: Vertical(g3)
    c: PointOnObject(g0,g-1)
    c: PointOnObject(g4,g-1)
    c: DistanceX(g4) = 134.058
    c: DistanceX(g0,g4) = 10
    c: DistanceY(g0,g2) = 30
    c: DistanceX(g0,g0) = 40
FEATURE [PartDesign::SubShapeBinder] Binder023
  BindCopyOnChange = 0
  BindMode = 0
  ClaimChildren = false
  Context = -> Part002 [Body012.Binder023.]
  Fuse = false
  MakeFace = true
  OffsetFill = false
  OffsetIntersection = false
  OffsetJoinType = 0
  OffsetOpenResult = false
  PartialLoad = false
  Relative = true
  Support = -> [Body003[Pocket021.Sketch026.]]
  _Version = 2
FEATURE [Sketcher::SketchObject] Sketch044
  ExternalGeometry = -> [Binder023]
  FullyConstrained = true
  MapMode = 5
  Support = -> [XY_Plane015]
  sketch-geometry (5):
    g0: LineSegment StartX=175.913 StartY=-11.05 StartZ=0 EndX=289.858 EndY=110.695 EndZ=0
    g1: LineSegment StartX=289.858 StartY=110.695 StartZ=0 EndX=297.084 EndY=110.695 EndZ=0
    g2: LineSegment StartX=297.084 StartY=110.695 StartZ=0 EndX=297.084 EndY=-11.05 EndZ=0
    g3: LineSegment StartX=175.913 StartY=-11.05 StartZ=0 EndX=297.084 EndY=-11.05 EndZ=0
    g4: LineSegment StartX=289.858 StartY=110.695 StartZ=0 EndX=289.274 EndY=111.242 EndZ=0
  constraints (14):
    c: Coincident(g1,g0)
    c: Horizontal(g1)
    c: Coincident(g2,g1)
    c: Vertical(g2)
    c: Coincident(g3,g0)
    c: Coincident(g3,g2)
    c: Horizontal(g3)
    c: Coincident(g4,g0)
    c: Coincident(g4,g-3)
    c: Perpendicular(g-3,g4)
    c: Perpendicular(g0,g4)
    c: Distance(g4) = 0.8
    c: Horizontal(g-3,g0)
    c: Distance(g1,g-4) = 3
FEATURE [PartDesign::FeaturePython] BaseBend007  # WARN: FeaturePython — macro-defined, semantics opaque (R4)
  BendSide = 0
  BendSketch = -> Sketch044
  MidPlane = false
  Reverse = false
  length = 100
  radius = 0.1
  thickness = 0.3
  expr: radius = composit_properties#<<Properties>>.bend_r
  expr: thickness = composit_properties#<<Properties>>.al_thickness
FEATURE [PartDesign::FeaturePython] Bend  # WARN: FeaturePython — macro-defined, semantics opaque (R4)
  AutoMiter = true
  BaseFeature = -> BaseBend007
  BendType = 0
  LengthList = [20]
  LengthSpec = 0
  ReliefFactor = 0.7
  UseReliefFactor = false
  angle = 90
  baseObject = -> BaseBend007 [Edge3]
  bendAList = [90]
  extend1 = 0
  extend2 = 0
  gap1 = 0
  gap2 = 0
  invert = false
  kfactor = 0.5
  length = 20
  maxExtendDist = 5
  minGap = 0.1
  minReliefGap = 1
  miterangle1 = 0
  miterangle2 = 0
  offset = 0
  radius = 0.1
  reliefType = 0
  reliefd = 1
  reliefw = 0.8
  sketchflip = false
  sketchinvert = false
  unfold = false
  expr: radius = BaseBend.radius
FEATURE [Sketcher::SketchObject] Sketch045
  AttachmentOffset = pos=(0,0,0) rot=(0,1,0;1.5708rad)
  ExternalGeometry = -> [Sketch026]
  FullyConstrained = true
  MapMode = 7
  Placement = pos=(174.817,-11.05,0) rot=(0.852419,0.369717,0.369717;1.7298rad)
  Support = -> [Sketch026]
  sketch-geometry (4):
    g0: Circle CenterX=15 CenterY=13 CenterZ=0 NormalX=0 NormalY=0 NormalZ=1 AngleXU=0 Radius=1.7
    g1: Circle CenterX=152.498 CenterY=13 CenterZ=0 NormalX=0 NormalY=0 NormalZ=1 AngleXU=0 Radius=1.7
    g2: LineSegment StartX=-4.26e-14 StartY=0 StartZ=0 EndX=15 EndY=13 EndZ=0
    g3: LineSegment StartX=167.498 StartY=4.16e-14 StartZ=0 EndX=152.498 EndY=13 EndZ=0
  constraints (10):
    c: Horizontal(g0,g1)
    c: DistanceY(g0) = 13
    c: Coincident(g2,g-3)
    c: Coincident(g2,g0)
    c: Coincident(g3,g-3)
    c: Coincident(g3,g1)
    c: Equal(g3,g2)
    c: Equal(g0,g1)
    c: Diameter(g0) = 3.4
    c: DistanceX(g0) = 15
FEATURE [PartDesign::SubShapeBinder] Binder024
  BindCopyOnChange = 0
  BindMode = 0
  ClaimChildren = true
  Context = -> Part002 [Body012.Binder024.]
  Fuse = false
  MakeFace = true
  OffsetFill = false
  OffsetIntersection = false
  OffsetJoinType = 0
  OffsetOpenResult = false
  PartialLoad = false
  Relative = true
  Support = -> [Body003[Pocket031.Sketch045.]]
  _Version = 2
FEATURE [PartDesign::Pocket] Pocket032
  BaseFeature = -> Bend
  Direction = (-0.730107,0.683333,-2.3e-15)
  Length = 5
  Length2 = 5
  Profile = -> Binder024
  Reversed = true
  Type = 0
FEATURE [PartDesign::SubShapeBinder] Binder025
  BindCopyOnChange = 0
  BindMode = 0
  ClaimChildren = false
  Context = -> Part002 [Body012.Binder025.]
  Fuse = false
  MakeFace = true
  OffsetFill = false
  OffsetIntersection = false
  OffsetJoinType = 0
  OffsetOpenResult = false
  PartialLoad = false
  Relative = true
  Support = -> [Body[Sketch013.]]
  _Version = 2
FEATURE [PartDesign::Pocket] Pocket033
  BaseFeature = -> Pocket032
  Direction = (0,0,-1)
  Length = 5
  Length2 = 5
  Midplane = true
  Profile = -> Binder025
  Type = 1
FEATURE [PartDesign::Body] Body012  label="top_corner_material_0.30ansi"
  Group = -> [Binder023,Sketch044,BaseBend007,Bend,Binder024,Pocket032,Binder025,Pocket033]
  Origin = -> Origin015
  Tip = -> Pocket033
FEATURE [Sketcher::SketchObject] Sketch046
  ExternalGeometry = -> [Binder001]
  FullyConstrained = true
  MapMode = 5
  Support = -> [XY_Plane]
  sketch-geometry (5):
    g0: LineSegment StartX=291.385 StartY=131.058 StartZ=0 EndX=281.744 EndY=120.757 EndZ=0
    g1: LineSegment StartX=281.744 StartY=120.757 StartZ=0 EndX=267.635 EndY=120.757 EndZ=0
    g2: LineSegment StartX=289.195 StartY=133.108 StartZ=0 EndX=291.385 EndY=131.058 EndZ=0
    g3: LineSegment StartX=291.385 StartY=131.058 StartZ=0 EndX=291.385 EndY=134.058 EndZ=0
    g4: GeomPoint X=277.635 Y=120.757 Z=0
  constraints (17):
    c: Coincident(g1,g0)
    c: Horizontal(g1)
    c: Parallel(g0,g-3)
    c: DistanceY(g0,g-3) = 3
    c: PointOnObject(g2,g-3)
    c: Coincident(g2,g0)
    c: Coincident(g2,g3)
    c: Vertical(g3)
    c: Horizontal(g-3,g3)
    c: Equal(g3,g2)
    c: Perpendicular(g-3,g2)
    c: PointOnObject(g4,g-3)
    c: PointOnObject(g4,g1)
    c: DistanceX(g1,g4) = 10
    c: Equal(g1,g0)
    c: DistanceY(g0,g-3) = 13.3011
    c: DistanceX(g1,g1) = 14.109
FEATURE [PartDesign::CoordinateSystem] Local_CS003
  AttacherType = Attacher::AttachEngine3D
  AttachmentOffset = pos=(0,-50,0) rot=(0,0,1;3.14159rad)
  MapMode = 6
  Placement = pos=(277.635,120.757,50) rot=(-0.293211,0.676028,0.676028;3.71203rad)
  Support = -> [Local_CS001,Sketch046]
FEATURE [Sketcher::SketchObject] Sketch047
  ExternalGeometry = -> [Sketch046]
  FullyConstrained = true
  MapMode = 5
  Placement = pos=(277.635,120.757,50) rot=(-0.293211,0.676028,0.676028;3.71203rad)
  Support = -> [Local_CS003]
  sketch-geometry (5):
    g0: LineSegment StartX=0 StartY=-9.5 StartZ=0 EndX=3.2 EndY=-9.5 EndZ=0
    g1: LineSegment StartX=3.2 StartY=-9.5 StartZ=0 EndX=3.2 EndY=9.5 EndZ=0
    g2: LineSegment StartX=3.2 StartY=9.5 StartZ=0 EndX=0 EndY=9.5 EndZ=0
    g3: LineSegment StartX=0 StartY=9.5 StartZ=0 EndX=0 EndY=-9.5 EndZ=0
    g4: GeomPoint X=1.6 Y=0 Z=0
  constraints (13):
    c: Coincident(g0,g1)
    c: Coincident(g1,g2)
    c: Coincident(g2,g3)
    c: Coincident(g3,g0)
    c: Horizontal(g0)
    c: Horizontal(g2)
    c: Vertical(g1)
    c: Vertical(g3)
    c: Vertical(g-3,g0)
    c: DistanceY(g3,g3) = 19
    c: DistanceX(g0,g0) = 3.2
    c: Symmetric(g0,g1,g4)
    c: PointOnObject(g4,g-1)
FEATURE [Sketcher::SketchObject] Sketch048
  FullyConstrained = true
  MapMode = 5
  Placement = pos=(277.635,120.757,50) rot=(-0.293211,0.676028,0.676028;3.71203rad)
  Support = -> [Local_CS003]
  sketch-geometry (2):
    g0: Circle CenterX=-10 CenterY=-5.5 CenterZ=0 NormalX=0 NormalY=0 NormalZ=1 AngleXU=0 Radius=1.7
    g1: Circle CenterX=-10 CenterY=5.5 CenterZ=0 NormalX=0 NormalY=0 NormalZ=1 AngleXU=0 Radius=1.7
  constraints (5):
    c: Symmetric(g0,g1,g-1)
    c: Equal(g0,g1)
    c: Diameter(g0) = 3.4
    c: DistanceY(g0,g1) = 11
    c: DistanceX(g1) = -10
FEATURE [PartDesign::Line] DatumLine
  AttacherType = Attacher::AttachEngineLine
  Length = 20
  MapMode = 29
  ResizeMode = 0
  Support = -> [Z_Axis001]
FEATURE [PartDesign::Plane] DatumPlane
  Length = 1124.49
  MapMode = 13
  Placement = pos=(96.6946,44.686,5.03002) rot=(-0.014044,0.998455,0.053755;3.1431rad)
  ResizeMode = 0
  Support = -> [Line,Line002]
  Width = 455.81
FEATURE [Sketcher::SketchObject] Sketch054
  ExternalGeometry = -> [Line002]
  FullyConstrained = true
  MapMode = 7
  Placement = pos=(164.614,-1.42e-14,0) rot=(0.880512,-0.347772,-0.322108;1.77331rad)
  Support = -> [Line]
  sketch-geometry (3):
    g0: LineSegment StartX=-2.68886 StartY=0.203704 StartZ=0 EndX=-3.624e-13 EndY=4.499e-13 EndZ=0
    g1: LineSegment StartX=-3.624e-13 StartY=4.499e-13 StartZ=0 EndX=1.3549e-12 EndY=2.69656 EndZ=0
    g2: ArcOfCircle CenterX=-2.5 CenterY=2.69656 CenterZ=0 NormalX=0 NormalY=0 NormalZ=1 AngleXU=0 Radius=2.5 StartAngle=4.63677 EndAngle=6.28319
  constraints (7):
    c: PointOnObject(g0,g-3)
    c: Coincident(g0,g-3)
    c: Coincident(g0,g1)
    c: PointOnObject(g1,g-2)
    c: Tangent(g2,g1) = -1.5708
    c: Tangent(g2,g0) = -1.5708
    c: Radius(g2) = 2.5
FEATURE [Sketcher::SketchObject] Sketch055
  ExternalGeometry = -> [Line]
  FullyConstrained = true
  MapMode = 7
  Placement = pos=(164.614,-3.55e-14,8.53e-14) rot=(0.577934,0.577934,0.576181;2.09615rad)
  Support = -> [Line002]
  sketch-geometry (3):
    g0: LineSegment StartX=-1.5028e-12 StartY=2.78439 StartZ=0 EndX=3.669e-13 EndY=2.616e-13 EndZ=0
    g1: LineSegment StartX=3.669e-13 StartY=2.616e-13 StartZ=0 EndX=2.76831 EndY=0.298829 EndZ=0
    g2: ArcOfCircle CenterX=2.5 CenterY=2.78439 CenterZ=0 NormalX=0 NormalY=0 NormalZ=1 AngleXU=0 Radius=2.5 StartAngle=3.14159 EndAngle=4.81992
  constraints (7):
    c: PointOnObject(g0,g-2)
    c: Coincident(g0,g-3)
    c: Coincident(g0,g1)
    c: PointOnObject(g1,g-3)
    c: Tangent(g2,g1) = -1.5708
    c: Tangent(g2,g0) = -1.5708
    c: Radius(g2) = 2.5
FEATURE [Sketcher::SketchObject] Sketch056
  ExternalGeometry = -> [Line002]
  FullyConstrained = true
  MapMode = 7
  Placement = pos=(-164.614,-1.42e-14,1) rot=(0.880889,0.347921,0.320915;1.77694rad)
  Support = -> [Line003]
  sketch-geometry (3):
    g0: LineSegment StartX=0 StartY=2.68463 StartZ=0 EndX=-5.68e-14 EndY=-5.68e-14 EndZ=0
    g1: LineSegment StartX=-5.68e-14 StartY=-5.68e-14 StartZ=0 EndX=2.67783 EndY=0.190965 EndZ=0
    g2: ArcOfCircle CenterX=2.5 CenterY=2.68463 CenterZ=0 NormalX=0 NormalY=0 NormalZ=1 AngleXU=0 Radius=2.5 StartAngle=3.14159 EndAngle=4.78358
  constraints (7):
    c: PointOnObject(g0,g-2)
    c: Coincident(g0,g-3)
    c: Coincident(g0,g1)
    c: PointOnObject(g1,g-3)
    c: Tangent(g2,g1) = -1.5708
    c: Tangent(g2,g0) = -1.5708
    c: Radius(g2) = 2.5
FEATURE [Sketcher::SketchObject] Sketch053  label="sink_pad_sketch"
  ExternalGeometry = -> [Line002,Line,Line003,Sketch056,Sketch054,Sketch055]
  FullyConstrained = true
  MapMode = 5
  Placement = pos=(96.6946,44.686,5.03002) rot=(0.967434,0.013608,0.252758;0.111187rad)
  Support = -> [DatumPlane]
  sketch-geometry (5):
    g0: LineSegment StartX=-380.445 StartY=100.694 StartZ=0 EndX=-261.308 EndY=-34.7826 EndZ=0
    g1: LineSegment StartX=-261.308 StartY=-34.7826 StartZ=0 EndX=65.6222 EndY=-44.0353 EndZ=0
    g2: LineSegment StartX=65.6222 StartY=-44.0353 StartZ=0 EndX=192.145 EndY=84.4891 EndZ=0
    g3: LineSegment StartX=192.145 StartY=84.4891 StartZ=0 EndX=-380.445 EndY=100.694 EndZ=0
    g4: LineSegment StartX=195.826 StartY=84.3849 StartZ=0 EndX=192.145 EndY=84.4891 EndZ=0
  constraints (18):
    c: Coincident(g0,g1)
    c: Coincident(g1,g2)
    c: Coincident(g2,g3)
    c: Coincident(g3,g0)
    c: Parallel(g0,g-5)
    c: Parallel(g1,g-3)
    c: Parallel(g1,g3)
    c: Parallel(g2,g-4)
    c: Coincident(g4,g-4)
    c: Coincident(g4,g2)
    c: Parallel(g4,g3)
    c: PointOnObject(g-8,g1)
    c: PointOnObject(g-7,g2)
    c: PointOnObject(g-6,g0)
    c: Distance(g2) = 180.351  'left'
    c: Distance(g1) = 327.061  'back'
    c: Distance(g3) = 572.82  'front'
    c: Distance(g0) = 180.41  'right'
FEATURE [PartDesign::FeaturePython] BaseBend001  label="sink_BaseBend"  # WARN: FeaturePython — macro-defined, semantics opaque (R4)
  BendSide = 0
  BendSketch = -> Sketch053
  MidPlane = false
  Reverse = false
  length = 1000
  radius = 2
  thickness = 0.5
FEATURE [Sketcher::SketchObject] Sketch050
  ExternalGeometry = -> [DatumLine,Sketch054]
  FullyConstrained = true
  MapMode = 7
  Placement = pos=(288.375,132.232,13.8981) rot=(0.259213,0.656292,0.708583;2.59582rad)
  Support = -> [Line,Sketch053]
  sketch-geometry (6):
    g0: ArcOfCircle CenterX=2.5 CenterY=2.69656 CenterZ=0 NormalX=0 NormalY=0 NormalZ=1 AngleXU=0 Radius=2.5 StartAngle=3.14159 EndAngle=4.788
    g1: LineSegment StartX=2.68886 StartY=0.203704 StartZ=0 EndX=2.65108 EndY=0.702276 EndZ=0
    g2: LineSegment StartX=-1.4784e-12 StartY=2.69656 StartZ=0 EndX=0 EndY=102.697 EndZ=0
    g3: LineSegment StartX=0 StartY=102.697 StartZ=0 EndX=0.5 EndY=102.697 EndZ=0
    g4: LineSegment StartX=0.5 StartY=102.697 StartZ=0 EndX=0.5 EndY=2.69656 EndZ=0
    g5: ArcOfCircle CenterX=2.5 CenterY=2.69656 CenterZ=0 NormalX=0 NormalY=0 NormalZ=1 AngleXU=0 Radius=2 StartAngle=3.14159 EndAngle=4.788
  constraints (15):
    c: PointOnObject(g2,g-2)
    c: Coincident(g2,g3)
    c: Horizontal(g3)
    c: Coincident(g3,g4)
    c: Vertical(g4)
    c: Coincident(g5,g0)
    c: Coincident(g5,g1)
    c: Perpendicular(g5,g1)
    c: Tangent(g5,g4) = -1.5708
    c: DistanceY(g4,g4) = 100
    c: Tangent(g2,g0) = 1.5708
    c: Coincident(g1,g0)
    c: Distance(g1) = 0.5
    c: Coincident(g0,g-4)
    c: Coincident(g0,g-4)
FEATURE [Sketcher::SketchObject] Sketch051
  ExternalGeometry = -> [Line]
  FullyConstrained = true
  MapMode = 7
  Placement = pos=(163.521,-4.09e-14,0.0033192) rot=(0.577934,0.577934,0.576181;2.09615rad)
  Support = -> [Line002,Sketch053]
  sketch-geometry (6):
    g0: ArcOfCircle CenterX=2.5 CenterY=2.78439 CenterZ=0 NormalX=0 NormalY=0 NormalZ=1 AngleXU=0 Radius=2.5 StartAngle=3.14159 EndAngle=4.81992
    g1: LineSegment StartX=0.5 StartY=2.78439 StartZ=0 EndX=0.5 EndY=102.784 EndZ=0
    g2: LineSegment StartX=0.5 StartY=102.784 StartZ=0 EndX=-2.7e-15 EndY=102.784 EndZ=0
    g3: LineSegment StartX=-2.7e-15 StartY=102.784 StartZ=0 EndX=-2.7e-15 EndY=2.78439 EndZ=0
    g4: ArcOfCircle CenterX=2.5 CenterY=2.78439 CenterZ=0 NormalX=0 NormalY=0 NormalZ=1 AngleXU=0 Radius=2 StartAngle=3.14159 EndAngle=4.81992
    g5: LineSegment StartX=2.76831 StartY=0.298829 StartZ=0 EndX=2.71465 EndY=0.795941 EndZ=0
  constraints (16):
    c: PointOnObject(g0,g-2)
    c: Coincident(g1,g2)
    c: PointOnObject(g2,g-2)
    c: Coincident(g2,g3)
    c: Perpendicular(g3,g2)
    c: Perpendicular(g2,g1)
    c: Tangent(g1,g4) = 1.5708
    c: Coincident(g4,g0)
    c: Radius(g4) = 2
    c: Tangent(g3,g0) = -1.5708
    c: DistanceY(g3,g3) = 100
    c: Coincident(g5,g0)
    c: Coincident(g5,g4)
    c: Tangent(g0,g-3) = -1.5708
    c: Perpendicular(g4,g5)
    c: Distance(g5) = 0.5
FEATURE [Sketcher::SketchObject] Sketch052
  ExternalGeometry = -> [Sketch056,DatumLine]
  FullyConstrained = true
  MapMode = 7
  Placement = pos=(-288.382,132.239,15.6508) rot=(0.880889,0.347921,0.320915;1.77694rad)
  Support = -> [Line003,Sketch053]
  sketch-geometry (6):
    g0: ArcOfCircle CenterX=2.5 CenterY=2.68463 CenterZ=0 NormalX=0 NormalY=0 NormalZ=1 AngleXU=0 Radius=2.5 StartAngle=3.14159 EndAngle=4.78358
    g1: LineSegment StartX=5.64e-14 StartY=2.68463 StartZ=0 EndX=7.79e-14 EndY=102.685 EndZ=0
    g2: LineSegment StartX=7.79e-14 StartY=102.685 StartZ=0 EndX=0.5 EndY=102.685 EndZ=0
    g3: LineSegment StartX=0.5 StartY=102.685 StartZ=0 EndX=0.5 EndY=2.68463 EndZ=0
    g4: ArcOfCircle CenterX=2.5 CenterY=2.68463 CenterZ=0 NormalX=0 NormalY=0 NormalZ=1 AngleXU=0 Radius=2 StartAngle=3.14159 EndAngle=4.78358
    g5: LineSegment StartX=2.67783 StartY=0.190965 StartZ=0 EndX=2.64227 EndY=0.689698 EndZ=0
  constraints (15):
    c: Coincident(g1,g2)
    c: Coincident(g2,g3)
    c: Tangent(g3,g4) = -1.5708
    c: Coincident(g4,g0)
    c: Perpendicular(g2,g1)
    c: Perpendicular(g3,g2)
    c: DistanceY(g1,g1) = 100
    c: Coincident(g5,g0)
    c: Coincident(g5,g4)
    c: Perpendicular(g4,g5)
    c: Coincident(g0,g-3)
    c: Parallel(g1,g-4)
    c: Tangent(g0,g1) = 1.5708
    c: Distance(g5) = 0.5
    c: Coincident(g0,g-3)
FEATURE [PartDesign::SubShapeBinder] Binder028
  BindCopyOnChange = 0
  BindMode = 0
  ClaimChildren = false
  Context = -> Body015 [Binder028.]
  Fuse = false
  MakeFace = true
  OffsetFill = false
  OffsetIntersection = false
  OffsetJoinType = 0
  OffsetOpenResult = false
  PartialLoad = false
  Relative = true
  Support = -> [Body[Sketch046.]]
  _Version = 2
FEATURE [Sketcher::SketchObject] Sketch057
  ExternalGeometry = -> [Binder028]
  FullyConstrained = true
  MapMode = 5
  Support = -> [XY_Plane018]
  sketch-geometry (2):
    g0: LineSegment StartX=281.847 StartY=125.257 StartZ=0 EndX=287.276 EndY=131.058 EndZ=0
    g1: LineSegment StartX=281.847 StartY=125.257 StartZ=0 EndX=-281.847 EndY=125.257 EndZ=0
  constraints (6):
    c: Parallel(g-3,g0)
    c: Distance(g-4,g0) = 3
    c: Coincident(g1,g0)
    c: Distance(g-4,g1) = 4.5
    c: Symmetric(g1,g1,g-2)
    c: Horizontal(g0,g-3)
FEATURE [PartDesign::FeaturePython] BaseBend009  # WARN: FeaturePython — macro-defined, semantics opaque (R4)
  BendSide = 0
  BendSketch = -> Sketch057
  MidPlane = false
  Reverse = false
  length = 115
  radius = 1
  thickness = 1
FEATURE [PartDesign::SubShapeBinder] Binder029
  BindCopyOnChange = 0
  BindMode = 0
  ClaimChildren = false
  Context = -> Body016 [Binder029.]
  Fuse = false
  MakeFace = true
  OffsetFill = false
  OffsetIntersection = false
  OffsetJoinType = 0
  OffsetOpenResult = false
  PartialLoad = false
  Relative = true
  Support = -> [Body[BaseBend.Sketch.]]
  _Version = 2
FEATURE [Sketcher::SketchObject] Sketch058
  ExternalGeometry = -> [Binder029]
  FullyConstrained = true
  MapMode = 5
  Support = -> [XY_Plane019]
  sketch-geometry (9):
    g0: LineSegment StartX=-297.084 StartY=131.058 StartZ=0 EndX=-297.084 EndY=-38 EndZ=0
    g1: LineSegment StartX=-297.084 StartY=-38 StartZ=0 EndX=297.084 EndY=-38 EndZ=0
    g2: LineSegment StartX=297.084 StartY=-38 StartZ=0 EndX=297.084 EndY=131.058 EndZ=0
    g3: LineSegment StartX=297.084 StartY=131.058 StartZ=0 EndX=-297.084 EndY=131.058 EndZ=0
    g4: GeomPoint X=0 Y=46.5289 Z=0
    g5: LineSegment StartX=297.084 StartY=134.058 StartZ=0 EndX=297.084 EndY=131.058 EndZ=0
    g6: LineSegment StartX=297.084 StartY=131.058 StartZ=0 EndX=300.084 EndY=131.058 EndZ=0
    g7: LineSegment StartX=297.084 StartY=-41 StartZ=0 EndX=297.084 EndY=-38 EndZ=0
    g8: LineSegment StartX=297.084 StartY=-38 StartZ=0 EndX=300.084 EndY=-38 EndZ=0
  constraints (25):
    c: Coincident(g0,g1)
    c: Coincident(g1,g2)
    c: Coincident(g2,g3)
    c: Coincident(g3,g0)
    c: Horizontal(g1)
    c: Horizontal(g3)
    c: Vertical(g0)
    c: Vertical(g2)
    c: Symmetric(g1,g0,g4)
    c: PointOnObject(g4,g-2)
    c: Coincident(g5,g2)
    c: Coincident(g5,g6)
    c: PointOnObject(g6,g-3)
    c: Coincident(g7,g1)
    c: Coincident(g7,g8)
    c: PointOnObject(g8,g-3)
    c: Horizontal(g8)
    c: Horizontal(g7,g-3)
    c: Vertical(g7)
    c: Equal(g7,g8)
    c: Equal(g8,g6)
    c: Equal(g6,g5)
    c: Horizontal(g5,g-3)
    c: Parallel(g5,g2)
    c: DistanceX(g6,g6) = 3
FEATURE [PartDesign::FeaturePython] BaseBend010  # WARN: FeaturePython — macro-defined, semantics opaque (R4)
  BendSide = 0
  BendSketch = -> Sketch058
  MidPlane = false
  Reverse = true
  length = 100
  radius = 0.1
  thickness = 0.3
  expr: radius = composit_properties#<<Properties>>.bend_r
  expr: thickness = composit_properties#<<Properties>>.al_thickness
FEATURE [PartDesign::FeaturePython] Bend009  # WARN: FeaturePython — macro-defined, semantics opaque (R4)
  AutoMiter = true
  BaseFeature = -> BaseBend010
  BendType = 1
  LengthList = [3]
  LengthSpec = 1
  ReliefFactor = 0.7
  UseReliefFactor = false
  angle = 90
  baseObject = -> BaseBend010 [Edge11]
  bendAList = [90]
  extend1 = 0
  extend2 = 0
  gap1 = 0
  gap2 = 0
  invert = false
  kfactor = 0.5
  length = 3
  maxExtendDist = 5
  minGap = 0.1
  minReliefGap = 1
  miterangle1 = 0
  miterangle2 = 0
  offset = 0
  radius = 0.1
  reliefType = 0
  reliefd = 1
  reliefw = 0.8
  sketchflip = false
  sketchinvert = false
  unfold = false
  expr: length = composit_properties#<<Properties>>.thickness
  expr: radius = BaseBend005.radius
FEATURE [PartDesign::SubShapeBinder] Binder030
  BindCopyOnChange = 0
  BindMode = 0
  ClaimChildren = false
  Context = -> Body015 [Binder030.]
  Fuse = false
  MakeFace = true
  OffsetFill = false
  OffsetIntersection = false
  OffsetJoinType = 0
  OffsetOpenResult = false
  PartialLoad = false
  Relative = true
  _Version = 2
FEATURE [Sketcher::SketchObject] Sketch059
  ExternalGeometry = -> [Sketch058]
  FullyConstrained = true
  MapMode = 5
  Support = -> [XY_Plane019]
  sketch-geometry (7):
    g0: LineSegment StartX=0 StartY=131.058 StartZ=0 EndX=0 EndY=121.058 EndZ=0
    g1: LineSegment StartX=0 StartY=-28 StartZ=0 EndX=0 EndY=-38 EndZ=0
    g2: Circle CenterX=0 CenterY=121.058 CenterZ=0 NormalX=0 NormalY=0 NormalZ=1 AngleXU=0 Radius=1.7
    g3: Circle CenterX=0 CenterY=-28 CenterZ=0 NormalX=0 NormalY=0 NormalZ=1 AngleXU=0 Radius=1.7
    g4: LineSegment StartX=0 StartY=121.058 StartZ=0 EndX=0 EndY=46.5289 EndZ=0
    g5: LineSegment StartX=0 StartY=46.5289 StartZ=0 EndX=0 EndY=-28 EndZ=0
    g6: Circle CenterX=0 CenterY=46.5289 CenterZ=0 NormalX=0 NormalY=0 NormalZ=1 AngleXU=0 Radius=1.7
  constraints (19):
    c: PointOnObject(g0,g-3)
    c: PointOnObject(g0,g-2)
    c: Vertical(g0)
    c: Coincident(g0,g4)
    c: PointOnObject(g5,g-2)
    c: Coincident(g5,g1)
    c: PointOnObject(g1,g-4)
    c: Vertical(g1)
    c: Coincident(g2,g0)
    c: Coincident(g3,g5)
    c: Coincident(g4,g5)
    c: Coincident(g6,g4)
    c: Equal(g5,g4)
    c: Equal(g0,g1)
    c: DistanceY(g1,g1) = 10
    c: Equal(g3,g6)
    c: Equal(g3,g2)
    c: Diameter(g3) = 3.4
    c: PointOnObject(g6,g-2)
FEATURE [Part::FeaturePython] LinearArray005  # WARN: FeaturePython — macro-defined, semantics opaque (R4)
  Alignment = 0
  CellStart = A1
  Count = 2
  Dir = (0,1,0)
  DirIsDriven = true
  DistributionLaw = 0
  DrivenProperty = 1
  EndInclusive = true
  ExposePlacement = false
  GeneratorMode = 0
  MarkerShape = 1
  MarkerSize = 0
  NumElements = 2
  OrientMode = 0
  Placement = pos=(-297.084,7,0) rot=(0,0,1;0rad)
  Point = (0,0,0)
  PointIsDriven = true
  Reverse = false
  SpanEnd = 90
  SpanStart = 0
  Step = 90
  Type = lattice2LinearArray.LinearArray
  VSGVersion = 1
  Values = 0.0 | 90.0
  ValuesSource = 2
  isLattice = 1
  expr: .Placement.Base.x = -<<base_sketch>>.Constraints.outer_width / 2 + composit_properties#<<Properties>>.thickness
FEATURE [Part::FeaturePython] Mirror004  label="Mirror004 of LinearArray005"  # WARN: FeaturePython — macro-defined, semantics opaque (R4)
  ExposePlacement = false
  FlipX = true
  FlipY = false
  FlipZ = false
  MarkerShape = 1
  MarkerSize = 0
  NumElements = 2
  Object = -> LinearArray005
  ObjectTraversal = 0
  Type = lattice2Mirror.LatticeMirror
  isLattice = 1
FEATURE [Part::FeaturePython] LinearArray006  # WARN: FeaturePython — macro-defined, semantics opaque (R4)
  Alignment = 0
  CellStart = A1
  Count = 4
  Dir = (0,1,0)
  DirIsDriven = true
  DistributionLaw = 0
  DrivenProperty = 1
  EndInclusive = true
  ExposePlacement = false
  GeneratorMode = 0
  MarkerShape = 1
  MarkerSize = 0
  NumElements = 4
  OrientMode = 0
  Placement = pos=(240.067,-38,0) rot=(0,0,1;1.5708rad)
  Point = (0,0,0)
  PointIsDriven = true
  Reverse = false
  SpanEnd = 480.134
  SpanStart = 0
  Step = 160.045
  Type = lattice2LinearArray.LinearArray
  VSGVersion = 1
  Values = 0.0 | 160.04471217950478 | 320.08942435900957 | 480.1341365385143
  ValuesSource = 2
  isLattice = 1
  expr: .Placement.Base.x = SpanEnd / 2
  expr: .Placement.Base.y = <<base_sketch>>.Constraints.back_offset + composit_properties#<<Properties>>.thickness
  expr: SpanEnd = <<base_sketch>>.Constraints.outer_width / 5 * 4
FEATURE [Sketcher::SketchObject] Sketch061
  FullyConstrained = true
  sketch-geometry (1):
    g0: Circle CenterX=0 CenterY=0 CenterZ=0 NormalX=0 NormalY=0 NormalZ=1 AngleXU=0 Radius=1.7
  constraints (3):
    c: PointOnObject(g0,g-1)
    c: DistanceX(g0) = 0
    c: Diameter(g0) = 3.4
FEATURE [Part::Extrusion] Extrude002  label="Extrude005"
  Base = -> Sketch061
  Dir = (0,0,1)
  DirMode = 2
  FaceMakerClass = Part::FaceMakerBullseye
  LengthFwd = 15
  LengthRev = 0
  Placement = pos=(0,0,-5) rot=(0,0,1;0rad)
  Solid = true
  Symmetric = false
FEATURE [PartDesign::SubShapeBinder] Binder033
  BindCopyOnChange = 0
  BindMode = 0
  ClaimChildren = false
  Context = -> Body019 [Binder033.]
  Fuse = false
  MakeFace = true
  OffsetFill = false
  OffsetIntersection = false
  OffsetJoinType = 0
  OffsetOpenResult = false
  PartialLoad = false
  Relative = true
  Support = -> [Sketch005]
  _Version = 2
FEATURE [Sketcher::SketchObject] Sketch062
  ExternalGeometry = -> [Binder033]
  FullyConstrained = true
  MapMode = 5
  Support = -> [XY_Plane022]
  sketch-geometry (9):
    g0: LineSegment StartX=280.724 StartY=124.058 StartZ=0 EndX=261.224 EndY=124.058 EndZ=0
    g1: LineSegment StartX=261.224 StartY=124.058 StartZ=0 EndX=261.224 EndY=103.223 EndZ=0
    g2: LineSegment StartX=261.224 StartY=103.223 StartZ=0 EndX=280.724 EndY=124.058 EndZ=0
    g3: LineSegment StartX=273.808 StartY=121.058 StartZ=0 EndX=264.224 EndY=121.058 EndZ=0
    g4: LineSegment StartX=264.224 StartY=121.058 StartZ=0 EndX=264.224 EndY=110.819 EndZ=0
    g5: LineSegment StartX=264.224 StartY=110.819 StartZ=0 EndX=273.808 EndY=121.058 EndZ=0
    g6: LineSegment StartX=273.808 StartY=124.058 StartZ=0 EndX=273.808 EndY=121.058 EndZ=0
    g7: LineSegment StartX=273.808 StartY=121.058 StartZ=0 EndX=275.998 EndY=119.008 EndZ=0
    g8: LineSegment StartX=264.224 StartY=110.819 StartZ=0 EndX=261.224 EndY=110.819 EndZ=0
  constraints (27):
    c: PointOnObject(g0,g-3)
    c: Horizontal(g0)
    c: Coincident(g0,g1)
    c: PointOnObject(g1,g-3)
    c: Vertical(g1)
    c: Coincident(g1,g2)
    c: Coincident(g2,g0)
    c: DistanceX(g0,g0) = 19.5
    c: DistanceY(g0,g-3) = 10
    c: Coincident(g3,g4)
    c: Coincident(g4,g5)
    c: Coincident(g5,g3)
    c: Parallel(g3,g0)
    c: Parallel(g4,g1)
    c: Parallel(g5,g2)
    c: PointOnObject(g6,g0)
    c: Coincident(g6,g3)
    c: Coincident(g6,g7)
    c: PointOnObject(g7,g2)
    c: Coincident(g4,g8)
    c: PointOnObject(g8,g1)
    c: Horizontal(g8)
    c: Vertical(g6)
    c: Perpendicular(g2,g7)
    c: Equal(g7,g6)
    c: Equal(g6,g8)
    c: DistanceX(g8,g8) = 3
FEATURE [PartDesign::Pad] Pad007
  Direction = (0,0,1)
  Length = 18
  Length2 = 10
  Profile = -> Sketch062
  ReferenceAxis = -> Sketch062 [N_Axis]
  Type = 0
FEATURE [Sketcher::SketchObject] Sketch063
  AttachmentOffset = pos=(0,0,-124.1) rot=(0,0,1;0rad)
  ExternalGeometry = -> [Sketch062]
  FullyConstrained = true
  MapMode = 5
  Placement = pos=(0,124.1,-2.76e-14) rot=(1,0,0;1.5708rad)
  Support = -> [XZ_Plane022]
  expr: Constraints[5] = Pad007.Length / 2
  sketch-geometry (3):
    g0: Circle CenterX=270.974 CenterY=9 CenterZ=0 NormalX=0 NormalY=0 NormalZ=1 AngleXU=0 Radius=1.7
    g1: LineSegment StartX=280.724 StartY=-2.75e-14 StartZ=0 EndX=270.974 EndY=9 EndZ=0
    g2: LineSegment StartX=270.974 StartY=9 StartZ=0 EndX=261.224 EndY=-2.84e-14 EndZ=0
  constraints (7):
    c: Coincident(g-3,g1)
    c: Coincident(g1,g0)
    c: Coincident(g1,g2)
    c: Coincident(g2,g-3)
    c: Equal(g2,g1)
    c: DistanceY(g-3,g0) = 9
    c: Diameter(g0) = 3.4
FEATURE [PartDesign::Hole] Hole002
  BaseFeature = -> Pad007
  CustomThreadClearance = 0
  Depth = 8
  DepthType = 0
  Diameter = 3.4
  DrillForDepth = false
  DrillPoint = 1
  DrillPointAngle = 118
  HoleCutCountersinkAngle = 90
  HoleCutCustomValues = false
  HoleCutDepth = 0
  HoleCutDiameter = 6.1
  HoleCutType = 0
  ModelThread = false
  Profile = -> Sketch063
  Reversed = true
  Tapered = false
  TaperedAngle = 90
  ThreadClass = 0
  ThreadDepth = 8
  ThreadDepthType = 0
  ThreadDirection = 0
  ThreadFit = 0
  ThreadSize = 0
  ThreadType = 0
  Threaded = false
  UseCustomThreadClearance = false
FEATURE [Sketcher::SketchObject] Sketch064
  AttachmentOffset = pos=(0,0,0) rot=(0,1,0;1.5708rad)
  FullyConstrained = true
  MapMode = 7
  Placement = pos=(271.619,114.329,0) rot=(0.852419,0.369717,0.369717;1.7298rad)
  Support = -> [Sketch062]
  sketch-geometry (2):
    g0: Circle CenterX=0.6273 CenterY=4 CenterZ=0 NormalX=0 NormalY=0 NormalZ=1 AngleXU=0 Radius=1.7
    g1: Circle CenterX=0.6273 CenterY=14 CenterZ=0 NormalX=0 NormalY=0 NormalZ=1 AngleXU=0 Radius=1.7
  constraints (6):
    c: Diameter(g0) = 3.4
    c: DistanceY(g0) = 4
    c: DistanceX(g0) = 0.6273
    c: Equal(g1,g0)
    c: Vertical(g1,g0)
    c: DistanceY(g0,g1) = 10
FEATURE [Sketcher::SketchObject] Sketch065
  ExternalGeometry = -> [Sketch062]
  FullyConstrained = true
  MapMode = 5
  Support = -> [XY_Plane022]
  sketch-geometry (4):
    g0: LineSegment StartX=261.224 StartY=106.15 StartZ=0 EndX=275.574 EndY=121.482 EndZ=0
    g1: LineSegment StartX=261.224 StartY=124.058 StartZ=0 EndX=261.224 EndY=106.15 EndZ=0
    g2: LineSegment StartX=275.574 StartY=121.482 StartZ=0 EndX=272.822 EndY=124.058 EndZ=0
    g3: LineSegment StartX=272.822 StartY=124.058 StartZ=0 EndX=261.224 EndY=124.058 EndZ=0
  constraints (12):
    c: Coincident(g0,g2)
    c: Coincident(g3,g1)
    c: Coincident(g1,g0)
    c: Vertical(g1)
    c: Vertical(g0,g-3)
    c: Parallel(g0,g-3)
    c: Distance(g0) = 21
    c: Coincident(g2,g3)
    c: Perpendicular(g0,g2)
    c: Horizontal(g2,g-3)
    c: Distance(g0,g-3) = 2
    c: Horizontal(g3)
FEATURE [PartDesign::Plane] DatumPlane001
  AttachmentOffset = pos=(0,0,9) rot=(0,0,1;0rad)
  Length = 348.425
  MapMode = 5
  Placement = pos=(0,0,9) rot=(0,0,1;0rad)
  ResizeMode = 0
  Support = -> [XY_Plane022]
  Width = 191.801
  expr: .AttachmentOffset.Base.z = Pad007.Length / 2
FEATURE [Sketcher::SketchObject] Sketch066
  AttachmentOffset = pos=(0,0,-2) rot=(0,0,1;0rad)
  ExternalGeometry = -> [Sketch064]
  FullyConstrained = true
  MapMode = 2
  Placement = pos=(270.159,115.696,3e-16) rot=(0.852419,0.369717,0.369717;1.7298rad)
  Support = -> [Sketch064]
  sketch-geometry (1):
    g0: Circle CenterX=0.6273 CenterY=4 CenterZ=0 NormalX=0 NormalY=0 NormalZ=1 AngleXU=0 Radius=4
  constraints (2):
    c: Coincident(g0,g-3)
    c: Diameter(g0) = 8
FEATURE [PartDesign::SubShapeBinder] Binder035
  BindCopyOnChange = 0
  BindMode = 0
  ClaimChildren = false
  Context = -> Body020 [Binder035.]
  Fuse = false
  MakeFace = true
  OffsetFill = false
  OffsetIntersection = false
  OffsetJoinType = 0
  OffsetOpenResult = false
  PartialLoad = false
  Relative = true
  Support = -> [Compound009]
  _Version = 2
FEATURE [PartDesign::Pad] Pad008  label="electric_shield_extrude"
  Direction = (0,0,1)
  Length = 3
  Length2 = 10
  Profile = -> Binder035
  Type = 0
FEATURE [Sketcher::SketchObject] Sketch070  label="electric_shield_fix_holes"
  FullyConstrained = false
  sketch-geometry (10):
    g0: Circle CenterX=0 CenterY=89.7 CenterZ=0 NormalX=0 NormalY=0 NormalZ=1 AngleXU=0 Radius=1.7
    g1: Circle CenterX=64.9014 CenterY=89.7 CenterZ=0 NormalX=0 NormalY=0 NormalZ=1 AngleXU=0 Radius=1.7
    g2: Circle CenterX=-64.9014 CenterY=89.7 CenterZ=0 NormalX=0 NormalY=0 NormalZ=1 AngleXU=0 Radius=1.7
    g3: Circle CenterX=-64.9014 CenterY=-89.7 CenterZ=0 NormalX=0 NormalY=0 NormalZ=1 AngleXU=0 Radius=1.7
    g4: Circle CenterX=64.9014 CenterY=-89.7 CenterZ=0 NormalX=0 NormalY=0 NormalZ=1 AngleXU=0 Radius=1.7
    g5: LineSegment StartX=-64.9014 StartY=-89.7 StartZ=0 EndX=-64.9014 EndY=89.7 EndZ=0
    g6: LineSegment StartX=-64.9014 StartY=89.7 StartZ=0 EndX=64.9014 EndY=89.7 EndZ=0
    g7: LineSegment StartX=64.9014 StartY=89.7 StartZ=0 EndX=64.9014 EndY=-89.7 EndZ=0
    g8: LineSegment StartX=64.9014 StartY=-89.7 StartZ=0 EndX=-64.9014 EndY=-89.7 EndZ=0
    g9: GeomPoint X=0 Y=0 Z=0
  constraints (22):
    c: Diameter(g0) = 3.4
    c: Symmetric(g2,g1,g-2)
    c: Horizontal(g0,g1)
    c: DistanceX(g2,g1) = 129.803
    c: Equal(g2,g0)
    c: Equal(g0,g1)
    c: Coincident(g5,g6)
    c: Coincident(g6,g7)
    c: Coincident(g7,g8)
    c: Coincident(g8,g5)
    c: Horizontal(g6)
    c: Horizontal(g8)
    c: Vertical(g5)
    c: Vertical(g7)
    c: Symmetric(g6,g5,g9)
    c: Coincident(g9,g-1)
    c: Coincident(g6,g1)
    c: Coincident(g3,g5)
    c: Coincident(g4,g7)
    c: Equal(g4,g3)
    c: Equal(g3,g0)
    c: DistanceY(g1) = 89.7
FEATURE [App::FeaturePython] SetupSheet  # Path/CAM operation (typed FeaturePython)
  ClearanceHeightExpression = OpStockZMax+SetupSheet.ClearanceHeightOffset
  ClearanceHeightOffset = 5
  CoolantMode = 0
  CoolantModes = None | Flood | Mist
  FinalDepthExpression = -0.1 mm
  HorizRapid = 0
  ProfileDirection = 1
  ProfileSide = 0
  ProfileUseComp = true
  ProfileprocessCircles = true
  ProfileprocessHoles = true
  ProfileprocessPerimeter = true
  SafeHeightExpression = OpStockZMax+SetupSheet.SafeHeightOffset
  SafeHeightOffset = 3
  StartDepthExpression = 3 mm
  StepDownExpression = 4 mm
  VertRapid = 0
FEATURE [Part::FeaturePython] ToolBit  label="3.175mm Endmill"  # Path/CAM toolbit (typed FeaturePython)
  BitPropertyNames = Chipload | CuttingEdgeHeight | Diameter | Flutes | Length | Material | ShankDiameter | SpindleDirection
  BitShape = <path>
  Chipload = 0
  CuttingEdgeHeight = 30
  Diameter = 3.17
  Flutes = 0
  Length = 10
  Material = 0
  ShankDiameter = 3
  ShapeName = endmill
  SpindleDirection = 0
FEATURE [Path::FeaturePython] __175mm_Endmill  label="3.175mm Endmill001"  # Path/CAM operation (typed FeaturePython)
  HorizFeed = 33.3333
  HorizRapid = 0
  SpindleDir = 0
  SpindleSpeed = 18000
  Tool = -> ToolBit
  ToolNumber = 1
  VertFeed = 8.33333
  VertRapid = 0
  expr: HorizRapid = SetupSheet.HorizRapid
  expr: VertRapid = SetupSheet.VertRapid
FEATURE [App::DocumentObjectGroup] Tools
  Group = -> [__175mm_Endmill]
FEATURE [Path::FeaturePython] Profile001  # Path/CAM operation (typed FeaturePython)
  Active = true
  AreaParams:
    Tolerance = 1e-07
    FitArcs = True
    Simplify = False
    CleanDistance = 0.0
    Accuracy = 0.01
    Unit = 1.0
    MinArcPoints = 4
    MaxArcPoints = 100
    ClipperScale = 10000000.0
    Fill = 0
    Coplanar = 0
    Reorient = True
    Outline = False
    Explode = False
    OpenMode = 0
    Deflection = 0.01
    SubjectFill = 0
    ClipFill = 0
    Offset = 1.585
    ExtraPass = 0
    Stepover = 0.0
    LastStepover = 0.0
    JoinType = 0
    EndType = 0
    MiterLimit = 2.0
    RoundPrecision = 0.0
    PocketMode = 0
    ToolRadius = 1.0
    PocketExtraOffset = 0.0
    PocketStepover = 0.0
    PocketLastStepover = 0.0
    FromCenter = False
    Angle = 45.0
    AngleShift = 0.0
    Shift = 0.0
    Thicken = False
    SectionCount = -1
    Stepdown = 1.0
    SectionOffset = 0.0
    SectionTolerance = 1e-07
    SectionMode = 2
    Project = False
  ClearanceHeight = 9
  CoolantMode = 0
  CycleTime = 00:00:28
  Direction = 1
  FinalDepth = -0.1
  HandleMultipleFeatures = 0
  JoinType = 0
  MiterLimit = 0.1
  OffsetExtra = 0
  OpFinalDepth = 0
  OpStartDepth = 4
  OpStockZMax = 4
  OpStockZMin = 0
  OpToolDiameter = 3.17
  PathParams = {'orientation': 0, 'feedrate': 33.333333333333336, 'feedrate_v': 8.333333333333334, 'verbose': True, 'resume_height': 7.0, 'retraction': 9.0, 'return_end': True, 'preamble': False}
  SafeHeight = 7
  Side = 0
  SplitArcs = false
  StartDepth = 3
  StartPoint = (0,0,0)
  StepDown = 4
  ToolController = -> __175mm_Endmill
  UseComp = true
  UseStartPoint = false
  processCircles = true
  processHoles = true
  processPerimeter = true
  expr: ClearanceHeight = OpStockZMax + SetupSheet.ClearanceHeightOffset
  expr: FinalDepth = -0.1 mm
  expr: SafeHeight = OpStockZMax + SetupSheet.SafeHeightOffset
  expr: StartDepth = 3 mm
  expr: StepDown = 4 mm
FEATURE [Part::FeaturePython] Join003  label="bottom_fix"  # WARN: FeaturePython — macro-defined, semantics opaque (R4)
  ExposePlacement = false
  Interleave = false
  Links = -> [Mirror004,LinearArray006,LinearArray005]
  MarkerShape = 1
  MarkerSize = 0
  NumElements = 8
  Type = lattice2JoinArrays.JoinArrays
  isLattice = 1
FEATURE [Part::FeaturePython] Placment004  label="Custom"  # WARN: FeaturePython — macro-defined, semantics opaque (R4)
  ExposePlacement = true
  FlipZ = false
  Invert = false
  MarkerShape = 1
  MarkerSize = 2
  NumElements = 1
  Placement = pos=(13,0,0) rot=(0,0,1;0rad)
  PlacementChoice = 0
  Type = lattice2Placement.LatticePlacement
  isLattice = 1
FEATURE [Part::FeaturePython] Placment005  label="Custom001"  # WARN: FeaturePython — macro-defined, semantics opaque (R4)
  ExposePlacement = true
  FlipZ = false
  Invert = false
  MarkerShape = 1
  MarkerSize = 2
  NumElements = 1
  Placement = pos=(0,0,13) rot=(0,1,0;1.5708rad)
  PlacementChoice = 0
  Type = lattice2Placement.LatticePlacement
  isLattice = 1
FEATURE [Part::FeaturePython] Join004  label="corner_13_mm_holes"  # WARN: FeaturePython — macro-defined, semantics opaque (R4)
  ExposePlacement = false
  Interleave = false
  Links = -> [Placment004,Placment005]
  MarkerShape = 1
  MarkerSize = 0
  NumElements = 2
  Type = lattice2JoinArrays.JoinArrays
  isLattice = 1
FEATURE [Part::FeaturePython] Populate014  label="Populate bottom_fix with Join004"  # WARN: FeaturePython — macro-defined, semantics opaque (R4)
  Copying = 0
  ExposePlacement = false
  MarkerShape = 1
  MarkerSize = 0
  NumElements = 16
  Object = -> Join004
  OutputCompounding = 0
  PlacementsTo = -> Join003
  Referencing = 0
  Type = lattice2PopulateCopies.LatticePopulateCopies
  isLattice = 1
FEATURE [Part::FeaturePython] Populate015  label="Populate Populate bottom_fix with Join004 with Extrude005"  # WARN: FeaturePython — macro-defined, semantics opaque (R4)
  Copying = 0
  ExposePlacement = false
  MarkerShape = 1
  MarkerSize = 0
  NumElements = 0
  Object = -> Extrude002
  OutputCompounding = 1
  PlacementsTo = -> Populate014
  Referencing = 0
  Type = lattice2PopulateCopies.LatticePopulateCopies
  isLattice = 0
FEATURE [Part::Compound] Compound007  label="back_cut1"
  Links = -> [Populate011,Populate015]
FEATURE [PartDesign::SubShapeBinder] Binder037
  BindCopyOnChange = 0
  BindMode = 0
  ClaimChildren = true
  Context = -> Body [Binder037.]
  Fuse = false
  MakeFace = true
  OffsetFill = false
  OffsetIntersection = false
  OffsetJoinType = 0
  OffsetOpenResult = false
  PartialLoad = false
  Relative = true
  Support = -> [Sketch]
  _Version = 2
  expr: Support = <<base_sketch>>._self
FEATURE [PartDesign::FeaturePython] BaseBend  # WARN: FeaturePython — macro-defined, semantics opaque (R4)
  BendSide = 0
  BendSketch = -> Binder037
  MidPlane = false
  Reverse = false
  length = 640
  radius = 0.1
  thickness = 0.3
FEATURE [PartDesign::FeaturePython] Bend001  # WARN: FeaturePython — macro-defined, semantics opaque (R4)
  AutoMiter = false
  BaseFeature = -> BaseBend
  BendType = 0
  LengthList = [9]
  LengthSpec = 1
  ReliefFactor = 0.7
  UseReliefFactor = false
  angle = 90
  baseObject = -> BaseBend [Edge50,Edge66,Edge82]
  bendAList = [90]
  extend1 = 0
  extend2 = 0
  gap1 = 35
  gap2 = 35
  invert = false
  kfactor = 0.5
  length = 9
  maxExtendDist = 5
  minGap = 0.1
  minReliefGap = 1
  miterangle1 = 0
  miterangle2 = 0
  offset = 0
  radius = 0.1
  reliefType = 0
  reliefd = 1
  reliefw = 0.8
  sketchflip = false
  sketchinvert = false
  unfold = false
  expr: baseObject = tuple(BaseBend._self; list(<<Edge50>>; <<Edge66>>; <<Edge82>>))
  expr: gap2 = gap1
  expr: radius = BaseBend.radius
FEATURE [PartDesign::FeaturePython] Bend003  # WARN: FeaturePython — macro-defined, semantics opaque (R4)
  AutoMiter = true
  BaseFeature = -> Bend001
  BendType = 0
  LengthList = [15]
  LengthSpec = 0
  ReliefFactor = 0.7
  UseReliefFactor = false
  angle = 90
  baseObject = -> Bend001 [Edge131,Edge238]
  bendAList = [90]
  extend1 = 0
  extend2 = 0
  gap1 = 20
  gap2 = 3
  invert = false
  kfactor = 0.5
  length = 15
  maxExtendDist = 5
  minGap = 0.1
  minReliefGap = 1
  miterangle1 = 0
  miterangle2 = 0
  offset = 0
  radius = 0.1
  reliefType = 0
  reliefd = 1
  reliefw = 0.8
  sketchflip = false
  sketchinvert = false
  unfold = false
  expr: radius = BaseBend.radius
FEATURE [PartDesign::Boolean] Boolean003
  BaseFeature = -> Bend009
  Type = 1
FEATURE [PartDesign::Body] Body016  label="Body016_material_0.30ansi"
  Group = -> [Binder029,Sketch058,BaseBend010,Bend009,Sketch059,Boolean003]
  Origin = -> Origin019
  Placement = pos=(0,0,-3) rot=(0,0,1;0rad)
  Tip = -> Boolean003
FEATURE [Sketcher::SketchObject] Sketch071
  ExternalGeometry = -> [Sketch063]
  FullyConstrained = true
  MapMode = 2
  Placement = pos=(0,124.1,-2.76e-14) rot=(1,0,0;1.5708rad)
  Support = -> [Sketch063]
  sketch-geometry (1):
    g0: Circle CenterX=270.974 CenterY=9 CenterZ=0 NormalX=0 NormalY=0 NormalZ=1 AngleXU=0 Radius=9
  constraints (2):
    c: Coincident(g0,g-3)
    c: Diameter(g0) = 18
FEATURE [Part::FeaturePython] WireFilter  # WARN: FeaturePython — macro-defined, semantics opaque (R4)
  AttacherType = Attacher::AttachEngine3D
  ClaimChildren = true
  ColorKeyCount = 8
  Colorize = true
  FaceMaker = 5
  FixNormal = false
  FollowSource = true
  InvertedFaceScale = 5
  MaxWires = 25
  Normal = (0,1,2e-16)
  OffsetFill = false
  OffsetIntersection = false
  OffsetJoin = 0
  OffsetOpenResult = false
  Scale = (1,1,1)
  SelectEdges = false
  Source = -> Sketch071
  UniformScale = 1
  UseDefault = false
  UseSelected = true
  UseSelectedEdges = false
  Version = 0.2022.02.09
  WireOrder = [1]
FEATURE [Sketcher::SketchObject] Sketch072
  AttachmentOffset = pos=(0,0,2) rot=(0,0,1;0rad)
  ExternalGeometry = -> [Sketch063]
  FullyConstrained = true
  MapMode = 2
  Placement = pos=(0,122.1,-2.71e-14) rot=(1,0,0;1.5708rad)
  Support = -> [Sketch063]
  sketch-geometry (1):
    g0: Circle CenterX=270.974 CenterY=9 CenterZ=0 NormalX=0 NormalY=0 NormalZ=1 AngleXU=0 Radius=2.5
  constraints (2):
    c: Coincident(g0,g-3)
    c: Diameter(g0) = 5
FEATURE [PartDesign::Pocket] Pocket045
  BaseFeature = -> Hole002
  Direction = (0,1,-2e-16)
  Length = 5
  Length2 = 5
  Profile = -> Sketch072
  ReferenceAxis = -> Sketch072 [N_Axis]
  Reversed = true
  Type = 0
FEATURE [Sketcher::SketchObject] Sketch073
  FullyConstrained = false
  MapMode = 2
  Placement = pos=(271.619,114.329,0) rot=(0.852419,0.369717,0.369717;1.7298rad)
  Support = -> [Sketch064]
  sketch-geometry (4):
    g0: LineSegment StartX=-6 StartY=0 StartZ=0 EndX=-24.5767 EndY=0 EndZ=0
    g1: LineSegment StartX=-24.5767 StartY=0 StartZ=0 EndX=-24.5767 EndY=27.1269 EndZ=0
    g2: LineSegment StartX=-24.5767 StartY=27.1269 StartZ=0 EndX=-6 EndY=27.1269 EndZ=0
    g3: LineSegment StartX=-6 StartY=27.1269 StartZ=0 EndX=-6 EndY=0 EndZ=0
  constraints (10):
    c: Coincident(g0,g1)
    c: Coincident(g1,g2)
    c: Coincident(g2,g3)
    c: Coincident(g3,g0)
    c: Horizontal(g0)
    c: Horizontal(g2)
    c: Vertical(g1)
    c: Vertical(g3)
    c: PointOnObject(g0,g-1)
    c: DistanceX(g0) = -6
FEATURE [PartDesign::Pocket] Pocket046
  BaseFeature = -> Pocket045
  Direction = (-0.730107,0.683333,2e-16)
  Length = 5
  Length2 = 5
  Midplane = true
  Profile = -> Sketch073
  ReferenceAxis = -> Sketch073 [N_Axis]
  Type = 1
FEATURE [PartDesign::Pocket] Pocket040
  BaseFeature = -> Pocket046
  Direction = (-0.730107,0.683333,0)
  Length = 5
  Length2 = 5
  Midplane = true
  Profile = -> Sketch064
  ReferenceAxis = -> Sketch064 [N_Axis]
  Type = 1
FEATURE [PartDesign::Pocket] Pocket041
  BaseFeature = -> Pocket040
  Direction = (-0.730107,0.683333,2e-16)
  Length = 5
  Length2 = 5
  Profile = -> Sketch066
  ReferenceAxis = -> Sketch066 [N_Axis]
  Type = 1
FEATURE [PartDesign::Mirrored] Mirrored010
  BaseFeature = -> Pocket041
  MirrorPlane = -> DatumPlane001
  Originals = -> [Pocket040,Pocket041]
FEATURE [PartDesign::Pocket] Pocket044
  BaseFeature = -> Mirrored010
  Direction = (0,-1,-2e-16)
  Length = 5
  Length2 = 5
  Profile = -> WireFilter
  Type = 1
FEATURE [PartDesign::Body] Body019
  Group = -> [Binder033,Sketch062,Pad007,Sketch063,Hole002,Sketch064,Sketch065,DatumPlane001,Sketch071,Sketch072,Pocket045,Sketch073,Pocket046,Pocket040,Pocket041,Mirrored010,Sketch066,WireFilter,Pocket044]
  Origin = -> Origin022
  Placement = pos=(0,0,50) rot=(0,0,1;0rad)
  Tip = -> Pocket044
FEATURE [PartDesign::SubShapeBinder] Binder038
  BindCopyOnChange = 0
  BindMode = 0
  ClaimChildren = false
  Context = -> Body021 [Binder038.]
  Fuse = false
  MakeFace = true
  OffsetFill = false
  OffsetIntersection = false
  OffsetJoinType = 0
  OffsetOpenResult = false
  PartialLoad = false
  Relative = true
  Support = -> [Body016[BaseBend010.Sketch058.]]
  _Version = 2
FEATURE [PartDesign::Pad] Pad009
  Direction = (0,0,1)
  Length = 3
  Length2 = 10
  Profile = -> Binder038
  Type = 0
FEATURE [PartDesign::Boolean] Boolean004
  BaseFeature = -> Pad009
  Type = 1
FEATURE [Part::Compound] Compound010
  Links = -> [Populate015]
FEATURE [PartDesign::SubShapeBinder] Binder039
  BindCopyOnChange = 0
  BindMode = 0
  ClaimChildren = false
  Context = -> Body [Binder039.]
  Fuse = false
  MakeFace = true
  OffsetFill = false
  OffsetIntersection = false
  OffsetJoinType = 0
  OffsetOpenResult = false
  PartialLoad = false
  Relative = true
  Support = -> [Body019[Sketch064.]]
  _Version = 2
FEATURE [PartDesign::Pocket] Pocket047
  BaseFeature = -> Bend003
  Direction = (-0.730107,0.683333,0)
  Length = 5
  Length2 = 5
  Midplane = true
  Profile = -> Binder039
  Type = 0
FEATURE [PartDesign::Pad] Pad005
  BaseFeature = -> Pocket047
  Direction = (0,0,-1)
  Length = 6
  Length2 = 10
  Profile = -> Bend003 [Face113,Face120,Face124,Face137,Face145,Face15,Face25,Face26,Face33,Face34]
  Type = 0
FEATURE [PartDesign::Pocket] Pocket022
  BaseFeature = -> Pad005
  Direction = (0,0,-1)
  Length = 5
  Length2 = 5
  Profile = -> Sketch031
  ReferenceAxis = -> Sketch031 [N_Axis]
  Type = 0
FEATURE [PartDesign::Pocket] Pocket008
  BaseFeature = -> Pocket022
  Direction = (0,0,-1)
  Length = 5
  Length2 = 5
  Profile = -> Sketch013
  ReferenceAxis = -> Sketch013 [N_Axis]
  Reversed = true
  Type = 1
FEATURE [PartDesign::SubShapeBinder] Binder041
  BindCopyOnChange = 0
  BindMode = 0
  ClaimChildren = false
  Context = -> Part002 [Body014.Binder041.]
  Fuse = false
  MakeFace = true
  OffsetFill = false
  OffsetIntersection = false
  OffsetJoinType = 0
  OffsetOpenResult = false
  PartialLoad = false
  Relative = true
  Support = -> [Body003[BaseBend002.Sketch011.]]
  _Version = 2
FEATURE [Sketcher::SketchObject] Sketch074
  ExternalGeometry = -> [Binder041]
  FullyConstrained = true
  MapMode = 5
  Placement = pos=(0,0,0) rot=(0.57735,0.57735,0.57735;2.0944rad)
  Support = -> [YZ_Plane017]
  sketch-geometry (11):
    g0: LineSegment StartX=135.271 StartY=24.1563 StartZ=0 EndX=159.891 EndY=19.8151 EndZ=0
    g1: LineSegment StartX=159.891 StartY=19.8151 StartZ=0 EndX=160.412 EndY=22.7695 EndZ=0
    g2: LineSegment StartX=160.412 StartY=22.7695 StartZ=0 EndX=132.838 EndY=27.6317 EndZ=0
    g3: LineSegment StartX=132.838 StartY=27.6317 StartZ=0 EndX=129.023 EndY=6 EndZ=0
    g4: LineSegment StartX=129.023 StartY=6 StartZ=0 EndX=111.541 EndY=6 EndZ=0
    g5: LineSegment StartX=111.541 StartY=6 StartZ=0 EndX=111.541 EndY=3 EndZ=0
    g6: LineSegment StartX=135.271 StartY=24.1563 StartZ=0 EndX=131.541 EndY=3 EndZ=0
    g7: LineSegment StartX=131.541 StartY=3 StartZ=0 EndX=111.541 EndY=3 EndZ=0
    g8: LineSegment StartX=131.541 StartY=0 StartZ=0 EndX=131.541 EndY=3 EndZ=0
    g9: LineSegment StartX=131.541 StartY=3 StartZ=0 EndX=134.495 EndY=2.47906 EndZ=0
    g10: LineSegment StartX=135.271 StartY=24.1563 StartZ=0 EndX=132.317 EndY=24.6773 EndZ=0
  constraints (33):
    c: Coincident(g0,g1)
    c: Coincident(g1,g2)
    c: Coincident(g2,g3)
    c: Coincident(g3,g4)
    c: Horizontal(g4)
    c: Coincident(g4,g5)
    c: Vertical(g5)
    c: Coincident(g0,g6)
    c: Coincident(g6,g7)
    c: Coincident(g7,g5)
    c: Parallel(g7,g-1)
    c: Parallel(g6,g-3)
    c: Perpendicular(g6,g0)
    c: Perpendicular(g1,g0)
    c: Perpendicular(g2,g1)
    c: Perpendicular(g3,g2)
    c: PointOnObject(g-3,g0)
    c: PointOnObject(g8,g-1)
    c: Coincident(g8,g6)
    c: Vertical(g8)
    c: Coincident(g8,g9)
    c: PointOnObject(g9,g-3)
    c: Perpendicular(g9,g-3)
    c: Equal(g9,g8)
    c: Distance(g8) = 3
    c: Coincident(g10,g0)
    c: PointOnObject(g10,g3)
    c: Perpendicular(g3,g10)
    c: Equal(g10,g1)
    c: Equal(g1,g5)
    c: DistanceY(g5,g5) = 3
    c: Distance(g-3,g0) = 22
    c: DistanceX(g7,g7) = 20
FEATURE [PartDesign::Pad] Pad010
  Direction = (1,0,0)
  Length = 10
  Length2 = 10
  Midplane = true
  Placement = pos=(0,0,0) rot=(0.57735,0.57735,0.57735;2.0944rad)
  Profile = -> Sketch074
  ReferenceAxis = -> Sketch074 [N_Axis]
  Type = 0
FEATURE [App::Link] Link004  label="top_material_0.30ansi001"
  LinkedObject = -> Body003
FEATURE [PartDesign::SubShapeBinder] Binder042
  BindCopyOnChange = 0
  BindMode = 0
  ClaimChildren = false
  Context = -> Part002 [Body003.Binder042.]
  Fuse = false
  MakeFace = true
  OffsetFill = false
  OffsetIntersection = false
  OffsetJoinType = 0
  OffsetOpenResult = false
  PartialLoad = false
  Placement = pos=(0,0,0) rot=(0.57735,0.57735,0.57735;2.0944rad)
  Relative = false
  Support = -> [Sketch011]
  _Version = 2
  expr: Support = <<top_BaseSketch>>._self
FEATURE [PartDesign::FeaturePython] BaseBend002  label="top_BaseBend"  # WARN: FeaturePython — macro-defined, semantics opaque (R4)
  BendSide = 0
  BendSketch = -> Binder042
  MidPlane = true
  Reverse = false
  length = 580.168
  radius = 0.1
  thickness = 0.3
  expr: length = <<main_sketch>>.Constraints.outer_width
FEATURE [PartDesign::Pocket] Pocket021
  BaseFeature = -> BaseBend002
  Direction = (0,0,-1)
  Length = 1
  Length2 = 5
  Profile = -> Sketch026
  ReferenceAxis = -> Sketch026 [N_Axis]
  Reversed = true
  Type = 0
FEATURE [PartDesign::Mirrored] Mirrored005
  BaseFeature = -> Pocket021
  MirrorPlane = -> YZ_Plane003
  Originals = -> [Pocket021]
FEATURE [PartDesign::FeaturePython] Bend007  # WARN: FeaturePython — macro-defined, semantics opaque (R4)
  AutoMiter = false
  BaseFeature = -> Mirrored005
  BendType = 0
  LengthList = [20]
  LengthSpec = 0
  ReliefFactor = 0.7
  UseReliefFactor = false
  angle = 90
  baseObject = -> Mirrored005 [Edge2,Edge5,Edge8,Edge11,Edge14,Edge17]
  bendAList = [90]
  extend1 = 0
  extend2 = 0
  gap1 = 0
  gap2 = 0
  invert = false
  kfactor = 0.5
  length = 20
  maxExtendDist = 5
  minGap = 0.1
  minReliefGap = 1
  miterangle1 = 0
  miterangle2 = 0
  offset = 0
  radius = 0.1
  reliefType = 0
  reliefd = 1
  reliefw = 0.8
  sketchflip = false
  sketchinvert = false
  unfold = false
  expr: radius = <<top_BaseBend>>.radius
FEATURE [PartDesign::Pocket] Pocket009
  BaseFeature = -> Bend007
  Direction = (0,0,-1)
  Length = 5
  Length2 = 5
  Midplane = true
  Profile = -> Binder012
  Refine = true
  Type = 1
FEATURE [PartDesign::Pocket] Pocket007
  BaseFeature = -> Pocket009
  Direction = (0,0,-1)
  Length = 5
  Length2 = 5
  Midplane = true
  Profile = -> Binder010
  Type = 1
FEATURE [PartDesign::Pocket] Pocket031
  BaseFeature = -> Pocket007
  Direction = (-0.730107,0.683333,-1e-16)
  Length = 5
  Length2 = 5
  Profile = -> Sketch045
  ReferenceAxis = -> Sketch045 [N_Axis]
  Reversed = true
  Type = 0
FEATURE [PartDesign::Mirrored] Mirrored008
  BaseFeature = -> Pocket031
  MirrorPlane = -> YZ_Plane003
  Originals = -> [Pocket031]
FEATURE [Part::FeaturePython] Placment006  # WARN: FeaturePython — macro-defined, semantics opaque (R4)
  AttacherType = Attacher::AttachEngine3D
  AttachmentOffset = pos=(0,-11,0) rot=(0,0,1;0rad)
  ExposePlacement = true
  MapMode = 7
  MarkerShape = 1
  MarkerSize = 5
  NumElements = 1
  Placement = pos=(0,149.058,21.7253) rot=(0,0.087156,0.996195;3.14159rad)
  Support = -> [Sketch011]
  Type = lattice2AttachablePlacement.AttachablePlacement
  isLattice = 1
  expr: .AttachmentOffset.Base.y = -(22 mm / 2)
FEATURE [Part::FeaturePython] Placment007  # WARN: FeaturePython — macro-defined, semantics opaque (R4)
  AttacherType = Attacher::AttachEngine3D
  AttachmentOffset = pos=(0,0,0) rot=(-1,0,0;1.5708rad)
  ExposePlacement = true
  MapMode = 45
  MarkerShape = 1
  MarkerSize = 5
  NumElements = 1
  Placement = pos=(0,136.142,11.8177) rot=(0,-0.642788,0.766044;3.14159rad)
  Support = -> [Sketch011]
  Type = lattice2AttachablePlacement.AttachablePlacement
  isLattice = 1
FEATURE [Part::FeaturePython] Placment008  # WARN: FeaturePython — macro-defined, semantics opaque (R4)
  AttacherType = Attacher::AttachEngine3D
  AttachmentOffset = pos=(0,0,-15) rot=(-1,0,0;1.5708rad)
  ExposePlacement = true
  MapMode = 7
  MarkerShape = 1
  MarkerSize = 2
  NumElements = 1
  Placement = pos=(0,119.058,3.3e-15) rot=(0,0,1;3.14159rad)
  Support = -> [Sketch011]
  Type = lattice2AttachablePlacement.AttachablePlacement
  isLattice = 1
FEATURE [Part::FeaturePython] Join005  # WARN: FeaturePython — macro-defined, semantics opaque (R4)
  ExposePlacement = false
  Interleave = false
  Links = -> [Placment006,Placment007,Placment008]
  MarkerShape = 1
  MarkerSize = 0
  NumElements = 3
  Type = lattice2JoinArrays.JoinArrays
  isLattice = 1
FEATURE [Part::FeaturePython] Populate016  label="Populate Join005 with Extrude005"  # WARN: FeaturePython — macro-defined, semantics opaque (R4)
  Copying = 0
  ExposePlacement = false
  MarkerShape = 1
  MarkerSize = 0
  NumElements = 0
  Object = -> Extrude002
  OutputCompounding = 1
  PlacementsTo = -> Join005
  Referencing = 0
  Type = lattice2PopulateCopies.LatticePopulateCopies
  isLattice = 0
FEATURE [PartDesign::Body] Body022  label="dummy_body"
  Origin = -> Origin025
FEATURE [PartDesign::Boolean] Boolean005
  BaseFeature = -> Pad010
  Type = 1
FEATURE [PartDesign::Body] Body014  label="lamp_holder"
  Group = -> [Binder041,Sketch074,Pad010,Boolean005]
  Origin = -> Origin017
  Placement = pos=(200,0,0) rot=(0,0,1;0rad)
  Tip = -> Boolean005
FEATURE [Part::Compound] Compound011
  Links = -> [Populate016]
FEATURE [Part::FeaturePython] LinearArray007  # WARN: FeaturePython — macro-defined, semantics opaque (R4)
  Alignment = 0
  CellStart = A1
  Count = 2
  Dir = (1,0,0)
  DirIsDriven = true
  DistributionLaw = 0
  DrivenProperty = 1
  EndInclusive = true
  ExposePlacement = false
  GeneratorMode = 0
  MarkerShape = 1
  MarkerSize = 0
  NumElements = 2
  OrientMode = 1
  Placement = pos=(-200,0,0) rot=(0,0,1;0rad)
  Point = (0,0,0)
  PointIsDriven = true
  Reverse = false
  SpanEnd = 400
  SpanStart = 0
  Step = 400
  Type = lattice2LinearArray.LinearArray
  VSGVersion = 1
  Values = 0.0 | 400.0
  ValuesSource = 2
  isLattice = 1
  expr: .Placement.Base.x = -SpanEnd / 2
FEATURE [Part::FeaturePython] Populate017  label="Populate LinearArray007 with Populate Join005 with Extrude005"  # WARN: FeaturePython — macro-defined, semantics opaque (R4)
  Copying = 0
  ExposePlacement = false
  MarkerShape = 1
  MarkerSize = 0
  NumElements = 0
  Object = -> Populate016
  OutputCompounding = 1
  PlacementsTo = -> LinearArray007
  Referencing = 0
  Type = lattice2PopulateCopies.LatticePopulateCopies
  isLattice = 0
FEATURE [Part::Compound] Compound012  label="top_cut1"
  Links = -> [Populate017]
FEATURE [PartDesign::Boolean] Boolean006
  BaseFeature = -> Mirrored008
  Group = -> [Compound012]
  Type = 1
  expr: Group = <<top_cut1>>._self
FEATURE [PartDesign::Body] Body003  label="top_material_0.30ansi"
  Group = -> [BaseBend002,Sketch027,Sketch029,Sketch043,Pocket021,Mirrored005,Bend007,Pocket009,Pocket007,Pocket031,Mirrored008,Boolean006,Binder010,Binder042,Binder012]
  Origin = -> Origin003
  Tip = -> BaseBend002
FEATURE [App::Part] Part002  label="top"
  Group = -> [Body003,Body012,Body014,Body002,Part001]
  Origin = -> Origin014
  Placement = pos=(0,0,640) rot=(0,0,1;0rad)
  expr: .Placement.Base.z = BaseBend.length
FEATURE [Sketcher::SketchObject] Sketch075
  ExternalGeometry = -> [Binder038]
  FullyConstrained = true
  MapMode = 5
  Placement = pos=(0,0,0) rot=(0.57735,0.57735,0.57735;2.0944rad)
  Support = -> [YZ_Plane024]
  sketch-geometry (3):
    g0: LineSegment StartX=131.058 StartY=3 StartZ=0 EndX=129.558 EndY=3 EndZ=0
    g1: LineSegment StartX=129.558 StartY=3 StartZ=0 EndX=131.058 EndY=1.5 EndZ=0
    g2: LineSegment StartX=131.058 StartY=1.5 StartZ=0 EndX=131.058 EndY=3 EndZ=0
  constraints (9):
    c: Horizontal(g0)
    c: Coincident(g0,g1)
    c: Coincident(g1,g2)
    c: Coincident(g2,g0)
    c: Vertical(g2)
    c: Equal(g2,g0)
    c: DistanceX(g0,g0) = 1.5
    c: DistanceY(g-3,g0) = 3
    c: Vertical(g0,g-3)
FEATURE [PartDesign::Pocket] Pocket049
  BaseFeature = -> Boolean004
  Direction = (-1,0,0)
  Length = 540
  Length2 = 5
  Midplane = true
  Profile = -> Sketch075
  ReferenceAxis = -> Sketch075 [N_Axis]
  Type = 0
FEATURE [PartDesign::Body] Body021
  Group = -> [Binder038,Pad009,Boolean004,Sketch075,Pocket049]
  Origin = -> Origin024
  Placement = pos=(0,0,-3) rot=(0,0,1;0rad)
  Tip = -> Pocket049
FEATURE [PartDesign::FeaturePython] Extend001  # WARN: FeaturePython — macro-defined, semantics opaque (R4)
  BaseFeature = -> Extend
  Offset = 0.02
  Refine = true
  UseSubtraction = false
  baseObject = -> Extend [Face12]
  gap1 = 0
  gap2 = 0
  length = 6
FEATURE [PartDesign::Boolean] Boolean002
  BaseFeature = -> Extend001
  Group = -> [Compound007]
  Type = 1
  expr: Group = <<back_cut1>>._self
FEATURE [PartDesign::Body] Body004  label="back_material_0.30ansi"
  Group = -> [Binder011,Sketch012,BaseBend003,Extend,Extend001,Boolean002]
  Origin = -> Origin004
  Tip = -> Extend001
FEATURE [PartDesign::SubShapeBinder] Binder043
  BindCopyOnChange = 0
  BindMode = 0
  ClaimChildren = true
  Context = -> Body023 [Binder043.]
  Fuse = false
  MakeFace = true
  OffsetFill = false
  OffsetIntersection = false
  OffsetJoinType = 0
  OffsetOpenResult = false
  PartialLoad = false
  Relative = false
  Support = -> [Sketch068]
  _Version = 2
FEATURE [PartDesign::Pad] Pad011
  Direction = (0,0,1)
  Length = 3
  Length2 = 10
  Profile = -> Binder043
  Type = 0
FEATURE [Sketcher::SketchObject] Sketch077
  FullyConstrained = true
  MapMode = 5
  Placement = pos=(0,0,0) rot=(1,0,0;1.5708rad)
  Support = -> [XZ_Plane018]
  sketch-geometry (1):
    g0: Circle CenterX=242 CenterY=85 CenterZ=0 NormalX=0 NormalY=0 NormalZ=1 AngleXU=0 Radius=15
  constraints (3):
    c: Diameter(g0) = 30
    c: DistanceX(g0) = 242
    c: DistanceY(g0) = 85
FEATURE [PartDesign::Pocket] Pocket052
  BaseFeature = -> BaseBend009
  Direction = (0,1,-2e-16)
  Length = 5
  Length2 = 5
  Midplane = true
  Profile = -> Sketch077
  ReferenceAxis = -> Sketch077 [N_Axis]
  Type = 1
FEATURE [App::DocumentObjectGroup] Group002  label="links"
  Group = -> [Link004]
FEATURE [Sketcher::SketchObject] Sketch078
  FullyConstrained = true
  MapMode = 5
  Placement = pos=(0,0,0) rot=(1,0,0;1.5708rad)
  Support = -> [XZ_Plane018]
  sketch-geometry (2):
    g0: Circle CenterX=271 CenterY=75 CenterZ=0 NormalX=0 NormalY=0 NormalZ=1 AngleXU=0 Radius=1.7
    g1: Circle CenterX=271 CenterY=35 CenterZ=0 NormalX=0 NormalY=0 NormalZ=1 AngleXU=0 Radius=1.7
  constraints (6):
    c: Vertical(g1,g0)
    c: DistanceY(g1,g0) = 40
    c: DistanceX(g0) = 271
    c: DistanceY(g0) = 75
    c: Equal(g1,g0)
    c: Diameter(g1) = 3.4
FEATURE [PartDesign::Pocket] Pocket
  BaseFeature = -> Pocket052
  Direction = (0,1,-2e-16)
  Length = 5
  Length2 = 5
  Midplane = true
  Profile = -> Sketch078
  ReferenceAxis = -> Sketch078 [N_Axis]
  Type = 1
FEATURE [PartDesign::Mirrored] Mirrored012
  BaseFeature = -> Pocket
  MirrorPlane = -> Sketch077 [V_Axis]
  Originals = -> [Pocket052,Pocket]
FEATURE [PartDesign::Body] Body015  label="front_shield"
  Group = -> [Sketch057,Binder028,BaseBend009,Binder030,Sketch077,Pocket052,Sketch078,Pocket,Mirrored012]
  Origin = -> Origin018
  Tip = -> Mirrored012
FEATURE [App::DocumentObjectGroup] Group003  label="sketches"
  Group = -> [Sketch005,Sketch011]
FEATURE [Part::FeaturePython] Placment009  label="electric_shield_placement"  # WARN: FeaturePython — macro-defined, semantics opaque (R4)
  AttacherType = Attacher::AttachEngine3D
  ExposePlacement = true
  MarkerShape = 1
  MarkerSize = 50
  NumElements = 1
  Placement = pos=(-299.784,40,430) rot=(0.57735,-0.57735,-0.57735;2.0944rad)
  Type = lattice2AttachablePlacement.AttachablePlacement
  isLattice = 1
  expr: .Placement.Base.x = -<<base_sketch>>.Constraints.outer_width / 2 + 0.3 mm
FEATURE [PartDesign::Boolean] Boolean007
  BaseFeature = -> Pad008
  Type = 1
FEATURE [PartDesign::Body] Body020  label="electric_shield"
  Group = -> [Binder035,Pad008,Boolean007]
  Origin = -> Origin023
  Tip = -> Boolean007
FEATURE [Part::FeaturePython] Clone002  label="Model-Body020"  # Draft clone (typed FeaturePython)
  AttacherType = Attacher::AttachEngine3D
  Fuse = false
  Objects = -> [Body020]
  PathResource = Model
  Placement = pos=(70,94.7,0) rot=(0,0,1;0rad)
  Scale = (1,1,1)
FEATURE [App::DocumentObjectGroup] Model
  Group = -> [Clone002]
FEATURE [Part::FeaturePython] Stock  # WARN: FeaturePython — macro-defined, semantics opaque (R4)
  Base = -> Model
  ExtXneg = 0
  ExtXpos = 1
  ExtYneg = 0
  ExtYpos = 1
  ExtZneg = 0
  ExtZpos = 1
  StockType = FromBase
FEATURE [Path::FeaturePython] Profile  # Path/CAM operation (typed FeaturePython)
  Active = true
  AreaParams:
    Tolerance = 1e-07
    FitArcs = True
    Simplify = False
    CleanDistance = 0.0
    Accuracy = 0.01
    Unit = 1.0
    MinArcPoints = 4
    MaxArcPoints = 100
    ClipperScale = 10000000.0
    Fill = 0
    Coplanar = 0
    Reorient = True
    Outline = False
    Explode = False
    OpenMode = 0
    Deflection = 0.01
    SubjectFill = 0
    ClipFill = 0
    Offset = -1.585
    ExtraPass = 0
    Stepover = 0.0
    LastStepover = 0.0
    JoinType = 0
    EndType = 0
    MiterLimit = 2.0
    RoundPrecision = 0.0
    PocketMode = 0
    ToolRadius = 1.0
    PocketExtraOffset = 0.0
    PocketStepover = 0.0
    PocketLastStepover = 0.0
    FromCenter = False
    Angle = 45.0
    AngleShift = 0.0
    Shift = 0.0
    Thicken = False
    SectionCount = -1
    Stepdown = 1.0
    SectionOffset = 0.0
    SectionTolerance = 1e-07
    SectionMode = 2
    Project = False
  Base = -> [Clone002]
  ClearanceHeight = 9
  CoolantMode = 0
  CycleTime = 00:00:23
  Direction = 1
  FinalDepth = -0.1
  HandleMultipleFeatures = 0
  JoinType = 0
  MiterLimit = 0.1
  OffsetExtra = 0
  OpFinalDepth = 0
  OpStartDepth = 4
  OpStockZMax = 4
  OpStockZMin = 0
  OpToolDiameter = 3.17
  PathParams = {'orientation': 1, 'feedrate': 33.333333333333336, 'feedrate_v': 8.333333333333334, 'verbose': True, 'resume_height': 7.0, 'retraction': 9.0, 'return_end': True, 'preamble': False, 'start': Vector (134.9999372874692, 184.59373072683164, 9.0)}
  SafeHeight = 7
  Side = 0
  SplitArcs = false
  StartDepth = 3
  StartPoint = (0,0,0)
  StepDown = 4
  ToolController = -> __175mm_Endmill
  UseComp = true
  UseStartPoint = false
  processCircles = true
  processHoles = true
  processPerimeter = false
  expr: ClearanceHeight = OpStockZMax + SetupSheet.ClearanceHeightOffset
  expr: FinalDepth = -0.1 mm
  expr: SafeHeight = OpStockZMax + SetupSheet.SafeHeightOffset
  expr: StartDepth = 3 mm
  expr: StepDown = 4 mm
FEATURE [App::DocumentObjectGroup] Operations
  Group = -> [Profile,Profile001]
FEATURE [Path::FeaturePython] Job  # Path/CAM operation (typed FeaturePython)
  CycleTime = 00:00:51
  Fixtures = G54
  GeometryTolerance = 0.01
  JobType = 0
  LastPostProcessDate = 2023-08-28 12:58:16.657321
  LastPostProcessOutput = <userpath>/0744-27F3/1.tap \n<userpath>/0744-27F3/2.tap
  Model = -> Model
  Operations = -> Operations
  OrderOutputBy = 2
  PostProcessor = 3
  PostProcessorOutputFile = %d.%j.tap
  SetupSheet = -> SetupSheet
  SplitOutput = true
  Stock = -> Stock
  Tools = -> Tools
FEATURE [PartDesign::Boolean] Boolean008
  BaseFeature = -> Pad011
  Refine = true
  Type = 1
FEATURE [PartDesign::Body] Body023  label="electric_shield_jamb"
  Group = -> [Binder043,Pad011,Boolean008]
  Origin = -> Origin026
  Tip = -> Boolean008
FEATURE [Part::FeaturePython] Placment010  label="electric_shield_fix_hole"  # WARN: FeaturePython — macro-defined, semantics opaque (R4)
  AttacherType = Attacher::AttachEngine3D
  ExposePlacement = true
  MarkerShape = 1
  MarkerSize = 50
  NumElements = 1
  Placement = pos=(65,90,0) rot=(0,0,1;0rad)
  Type = lattice2AttachablePlacement.AttachablePlacement
  isLattice = 1
FEATURE [Sketcher::SketchObject] Sketch067
  ExternalGeometry = -> [Placment010]
  FullyConstrained = true
  sketch-geometry (4):
    g0: LineSegment StartX=70 StartY=0 StartZ=0 EndX=70 EndY=90 EndZ=0
    g1: ArcOfCircle CenterX=65 CenterY=90 CenterZ=0 NormalX=0 NormalY=0 NormalZ=1 AngleXU=0 Radius=5 StartAngle=5e-16 EndAngle=3.14159
    g2: ArcOfCircle CenterX=55 CenterY=90 CenterZ=0 NormalX=0 NormalY=0 NormalZ=1 AngleXU=0 Radius=5 StartAngle=4.71239 EndAngle=6.28319
    g3: LineSegment StartX=0 StartY=85 StartZ=0 EndX=55 EndY=85 EndZ=0
  constraints (11):
    c: PointOnObject(g0,g-1)
    c: Vertical(g0)
    c: DistanceX(g0) = 70
    c: PointOnObject(g3,g-2)
    c: Horizontal(g3)
    c: Tangent(g1,g0) = -1.5708
    c: Tangent(g3,g2) = -1.5708
    c: Tangent(g2,g1) = 1.5708
    c: DistanceY(g3) = 85
    c: Equal(g2,g1)
    c: Coincident(g1,g-3)
FEATURE [Part::Mirroring] Part__Mirroring002  label="Sketch067 (Mirror #3)"
  Base = (0,0,0)
  Normal = (0,1,0)
  Source = -> Sketch067
FEATURE [Part::Compound] Compound008
  Links = -> [Part__Mirroring002,Sketch067]
FEATURE [Part::Mirroring] Part__Mirroring003  label="Compound008 (Mirror #4)"
  Base = (0,0,0)
  Normal = (1,0,0)
  Source = -> Compound008
FEATURE [Part::Compound] Compound009
  Links = -> [Part__Mirroring003,Compound008]
FEATURE [Sketcher::SketchObject] Sketch068  label="electric_shield_jamb_sketch"
  ExternalGeometry = -> [Sketch067]
  FullyConstrained = false
  sketch-geometry (9):
    g0: LineSegment StartX=-70.5 StartY=96.0308 StartZ=0 EndX=-70.5 EndY=84.0308 EndZ=0
    g1: LineSegment StartX=-67.5 StartY=81.0308 StartZ=0 EndX=67.5 EndY=81.0308 EndZ=0
    g2: LineSegment StartX=70.5 StartY=84.0308 StartZ=0 EndX=70.5 EndY=96.0308 EndZ=0
    g3: LineSegment StartX=70.5 StartY=96.0308 StartZ=0 EndX=-70.5 EndY=96.0308 EndZ=0
    g4: GeomPoint X=0 Y=88.5308 Z=0
    g5: ArcOfCircle CenterX=67.5 CenterY=84.0308 CenterZ=0 NormalX=0 NormalY=0 NormalZ=1 AngleXU=0 Radius=3 StartAngle=4.71239 EndAngle=6.28319
    g6: GeomPoint X=70.5 Y=81.0308 Z=0
    g7: ArcOfCircle CenterX=-67.5 CenterY=84.0308 CenterZ=0 NormalX=0 NormalY=0 NormalZ=1 AngleXU=0 Radius=3 StartAngle=3.14159 EndAngle=4.71239
    g8: GeomPoint X=-70.5 Y=81.0308 Z=0
  constraints (21):
    c: Coincident(g2,g3)
    c: Coincident(g3,g0)
    c: Horizontal(g1)
    c: Horizontal(g3)
    c: Vertical(g0)
    c: Vertical(g2)
    c: DistanceY(g6,g2) = 15
    c: DistanceX(g8,g6) = 141
    c: PointOnObject(g4,g-2)
    c: Symmetric(g8,g2,g4)
    c: PointOnObject(g6,g1)
    c: PointOnObject(g6,g2)
    c: Tangent(g1,g5) = -1.5708
    c: Tangent(g2,g5) = -1.5708
    c: PointOnObject(g8,g0)
    c: PointOnObject(g8,g1)
    c: Tangent(g0,g7) = -1.5708
    c: Tangent(g1,g7) = -1.5708
    c: Equal(g7,g5)
    c: Radius(g7) = 3
    c: DistanceX(g3,g3) = 141
FEATURE [Sketcher::SketchObject] Sketch079
  ExternalGeometry = -> [Placment010]
  FullyConstrained = true
  sketch-geometry (1):
    g0: Circle CenterX=50 CenterY=90 CenterZ=0 NormalX=0 NormalY=0 NormalZ=1 AngleXU=0 Radius=1.7
  constraints (3):
    c: DistanceX(g0) = 50
    c: Horizontal(g0,g-3)
    c: Diameter(g0) = 3.4
FEATURE [Part::Mirroring] Part__Mirroring004  label="Sketch079 (Mirror #5)"
  Base = (50,0,0)
  Normal = (0,1,-1.19209e-07)
  Source = -> Sketch079
FEATURE [Part::Compound] Compound013
  Links = -> [Part__Mirroring004,Sketch079]
FEATURE [Part::Mirroring] Part__Mirroring005  label="Compound013 (Mirror #6)"
  Base = (9.095e-13,0,5.96046e-06)
  Normal = (1,0,-1.19209e-07)
  Source = -> Compound013
FEATURE [Part::Compound] Compound014  label="electric_shield_jamb_fix_holes"
  Links = -> [Part__Mirroring005,Compound013]
FEATURE [Part::Extrusion] Extrude003  label="electric_shield_jamb_fix_holes_extrude"
  Base = -> Compound014
  Dir = (1.19209e-07,1.19209e-07,1)
  DirMode = 2
  FaceMakerClass = Part::FaceMakerBullseye
  LengthFwd = 10
  LengthRev = 0
  Solid = true
  Symmetric = false
FEATURE [Part::Compound] Compound015  label="electric_shield_jamb_fix_holes_face_cut"
  Links = -> [Extrude003]
  Placement = pos=(-299.484,40,430) rot=(0.57735,-0.57735,-0.57735;2.0944rad)
  expr: Placement = <<electric_shield_placement>>.Placement * placement(vector(0; 0; -0.3); rotation(0; 0; 0))
FEATURE [Part::FeaturePython] Mirror005  label="Mirror005 of electric_shield_fix_hole"  # WARN: FeaturePython — macro-defined, semantics opaque (R4)
  ExposePlacement = false
  FlipX = true
  FlipY = false
  FlipZ = false
  MarkerShape = 1
  MarkerSize = 20
  NumElements = 1
  Object = -> Placment010
  ObjectTraversal = 0
  Type = lattice2Mirror.LatticeMirror
  isLattice = 1
FEATURE [Part::FeaturePython] Join006  # WARN: FeaturePython — macro-defined, semantics opaque (R4)
  ExposePlacement = false
  Interleave = false
  Links = -> [Mirror005,Placment010]
  MarkerShape = 1
  MarkerSize = 0
  NumElements = 2
  Type = lattice2JoinArrays.JoinArrays
  isLattice = 1
FEATURE [Part::FeaturePython] Mirror006  label="Mirror006 of Join006"  # WARN: FeaturePython — macro-defined, semantics opaque (R4)
  ExposePlacement = false
  FlipX = false
  FlipY = true
  FlipZ = false
  MarkerShape = 1
  MarkerSize = 0
  NumElements = 2
  Object = -> Join006
  ObjectTraversal = 0
  Type = lattice2Mirror.LatticeMirror
  isLattice = 1
FEATURE [Part::FeaturePython] Join007  label="electric_shield_fix_holes_placements"  # WARN: FeaturePython — macro-defined, semantics opaque (R4)
  ExposePlacement = false
  Interleave = false
  Links = -> [Mirror006,Join006]
  MarkerShape = 1
  MarkerSize = 0
  NumElements = 4
  Type = lattice2JoinArrays.JoinArrays
  isLattice = 1
FEATURE [Part::FeaturePython] Populate018  label="Populate electric_shield_fix_holes_placements with hole_3.4_extrude"  # WARN: FeaturePython — macro-defined, semantics opaque (R4)
  Copying = 0
  ExposePlacement = false
  MarkerShape = 1
  MarkerSize = 0
  NumElements = 0
  Object = -> Extrude001
  OutputCompounding = 1
  PlacementsTo = -> Join007
  Referencing = 0
  Type = lattice2PopulateCopies.LatticePopulateCopies
  isLattice = 0
FEATURE [Part::Compound] Compound016  label="electric_shield_cut1"
  Links = -> [Populate018]
FEATURE [Part::Offset] Offset
  Fill = false
  Intersection = false
  Join = 0
  Mode = 0
  Placement = pos=(-299.784,40,430) rot=(0.57735,-0.57735,-0.57735;2.0944rad)
  SelfIntersection = false
  Source = -> Pad008
  Value = 0.1
  expr: Placement = <<electric_shield_placement>>.Placement
FEATURE [Part::Compound] Compound  label="face_cut1"
  Links = -> [Populate001,Populate011,Populate015,Compound015,Offset]
FEATURE [PartDesign::Boolean] Boolean
  BaseFeature = -> Pocket008
  Group = -> [Compound]
  Type = 1
FEATURE [PartDesign::Pocket] Pocket004
  BaseFeature = -> Boolean
  Direction = (0,0,-1)
  Length = 110
  Length2 = 5
  Profile = -> Sketch009
  ReferenceAxis = -> Sketch009 [N_Axis]
  Reversed = true
  Type = 0
FEATURE [PartDesign::Mirrored] Mirrored002
  BaseFeature = -> Pocket004
  MirrorPlane = -> Sketch009 [V_Axis]
  Originals = -> [Pocket004]
  Refine = true
FEATURE [PartDesign::Pocket] Pocket027
  BaseFeature = -> Mirrored002
  Direction = (0.730107,-0.683333,4e-16)
  Length = 5
  Length2 = 5
  Profile = -> Sketch039
  ReferenceAxis = -> Sketch039 [N_Axis]
  Type = 0
FEATURE [PartDesign::Pocket] Pocket028
  BaseFeature = -> Pocket027
  Direction = (0.730107,-0.683333,4e-16)
  Length = 5
  Length2 = 5
  Midplane = true
  Profile = -> Sketch040
  ReferenceAxis = -> Sketch040 [N_Axis]
  Type = 0
FEATURE [PartDesign::Pocket] Pocket029
  BaseFeature = -> Pocket028
  Direction = (-4e-16,-1,3e-16)
  Length = 5
  Length2 = 0.2
  Profile = -> Sketch041
  ReferenceAxis = -> Sketch041 [N_Axis]
  Type = 4
FEATURE [PartDesign::Mirrored] Mirrored007
  BaseFeature = -> Pocket029
  MirrorPlane = -> YZ_Plane
  Originals = -> [Pocket027,Pocket028,Pocket029,Pocket047]
  Refine = true
FEATURE [PartDesign::Body] Body  label="Body_material_0.30ansi"
  Group = -> [BaseBend,Binder001,Bend001,Sketch013,Binder037,Binder039,Bend003,Pocket047,Sketch030,Pad005,Sketch031,Pocket022,Sketch038,Pocket008,Boolean,Sketch009,Pocket004,Mirrored002,Local_CS001,Sketch039,Sketch040,Pocket027,Pocket028,Sketch041,Pocket029,Mirrored007,Sketch046,Sketch047,Sketch048,Local_CS003]
  Origin = -> Origin
  Tip = -> Pocket029
FEATURE [Sketcher::SketchObject] Sketch080
  FullyConstrained = true
  MapMode = 5
  Support = -> [XY_Plane028]
  sketch-geometry (5):
    g0: LineSegment StartX=-3.925 StartY=-3.925 StartZ=0 EndX=-3.925 EndY=3.925 EndZ=0
    g1: LineSegment StartX=-3.925 StartY=3.925 StartZ=0 EndX=3.925 EndY=3.925 EndZ=0
    g2: LineSegment StartX=3.925 StartY=3.925 StartZ=0 EndX=3.925 EndY=-3.925 EndZ=0
    g3: LineSegment StartX=3.925 StartY=-3.925 StartZ=0 EndX=-3.925 EndY=-3.925 EndZ=0
    g4: GeomPoint X=0 Y=1e-16 Z=0
  constraints (12):
    c: Coincident(g0,g1)
    c: Coincident(g1,g2)
    c: Coincident(g2,g3)
    c: Coincident(g3,g0)
    c: Horizontal(g1)
    c: Horizontal(g3)
    c: Vertical(g0)
    c: Vertical(g2)
    c: Symmetric(g1,g0,g4)
    c: Coincident(g4,g-1)
    c: Equal(g2,g1)
    c: DistanceX(g1,g1) = 7.85
FEATURE [PartDesign::Pad] Pad012
  Direction = (0,0,1)
  Length = 5
  Length2 = 10
  Profile = -> Sketch080
  ReferenceAxis = -> Sketch080 [N_Axis]
  Type = 0
FEATURE [PartDesign::Body] Body025  label="screw_cut"
  Group = -> [Sketch080,Pad012]
  Origin = -> Origin028
  Tip = -> Pad012
FEATURE [Part::FeaturePython] Populate019  label="Populate electric_shield_fix_holes_placements with screw_cut"  # WARN: FeaturePython — macro-defined, semantics opaque (R4)
  Copying = 0
  ExposePlacement = false
  MarkerShape = 1
  MarkerSize = 0
  NumElements = 0
  Object = -> Body025
  OutputCompounding = 1
  Placement = pos=(0,0,1.5) rot=(0,0,1;0rad)
  PlacementsTo = -> Join007
  Referencing = 0
  Type = lattice2PopulateCopies.LatticePopulateCopies
  isLattice = 0
FEATURE [Part::Compound] Compound017  label="electric_shield_jamb_cut1"
  Links = -> [Extrude003,Populate018,Populate019]
FEATURE [Part::FeaturePython] FuseCompound001  label="electric_shield_jamb_cut1_fuse"  # WARN: FeaturePython — macro-defined, semantics opaque (R4)
  Base = -> Compound017
  Refine = true
  recomputeQuota = -1
FEATURE [App::DocumentObjectGroup] Group004  label="placements"
  Group = -> [Placment009]
FEATURE [PartDesign::Pad] Pad013
  BaseFeature = -> BaseBend001
  Direction = (0.681109,-0.72773,-0.0806251)
  Length = 180.41
  Length2 = 10
  Profile = -> Sketch052
  ReferenceAxis = -> Sketch052 [N_Axis]
  Type = 0
  expr: Length = <<sink_pad_sketch>>.Constraints.right
FEATURE [PartDesign::Pad] Pad014
  BaseFeature = -> Pad013
  Direction = (0.68133,0.727966,0.0765123)
  Length = 180.351
  Length2 = 10
  Profile = -> Sketch050
  ReferenceAxis = -> Sketch050 [N_Axis]
  Reversed = true
  Type = 0
  expr: Length = <<sink_pad_sketch>>.Constraints.left
FEATURE [PartDesign::Pad] Pad015
  BaseFeature = -> Pad014
  Direction = (0.999995,1e-16,-0.00303739)
  Length = 327.061
  Length2 = 10
  Profile = -> Sketch051
  ReferenceAxis = -> Sketch051 [N_Axis]
  Reversed = true
  Type = 0
  expr: Length = <<sink_pad_sketch>>.Constraints.back
FEATURE [Sketcher::SketchObject] Sketch081
  ExternalGeometry = -> [Sketch053]
  FullyConstrained = false
  MapMode = 5
  Placement = pos=(96.6946,44.686,5.03002) rot=(-0.014044,0.998455,0.053755;3.1431rad)
  Support = -> [DatumPlane]
  sketch-geometry (2):
    g0: Circle CenterX=-104.279 CenterY=-83.2053 CenterZ=0 NormalX=0 NormalY=0 NormalZ=1 AngleXU=0 Radius=25.1105
    g1: Circle CenterX=216.965 CenterY=-71.8137 CenterZ=0 NormalX=0 NormalY=0 NormalZ=1 AngleXU=0 Radius=31.7244
FEATURE [Sketcher::SketchObject] Sketch008
  AttachmentOffset = pos=(0,0,0) rot=(0,1,0;1.5708rad)
  ExternalGeometry = -> [Sketch007,Sketch053,Sketch054]
  FullyConstrained = false
  MapMode = 7
  Placement = pos=(164.614,1.42e-14,0) rot=(0.852419,0.369717,0.369717;1.7298rad)
  Support = -> [Binder]
  sketch-geometry (17):
    g0: LineSegment StartX=175.907 StartY=87 StartZ=0 EndX=296.262 EndY=87 EndZ=0
    g1: LineSegment StartX=296.262 StartY=87 StartZ=0 EndX=296.262 EndY=16.5868 EndZ=0
    g2: LineSegment StartX=296.262 StartY=16.5868 StartZ=0 EndX=180.907 EndY=16.5868 EndZ=0
    g3: LineSegment StartX=-74 StartY=-1.883e-13 StartZ=0 EndX=-74 EndY=87 EndZ=0
    g4: LineSegment StartX=-74 StartY=87 StartZ=0 EndX=6 EndY=87 EndZ=0
    g5: LineSegment StartX=180.907 StartY=16.5868 StartZ=0 EndX=180.907 EndY=82 EndZ=0
    g6: ArcOfCircle CenterX=175.907 CenterY=82 CenterZ=0 NormalX=0 NormalY=0 NormalZ=1 AngleXU=0 Radius=5 StartAngle=-9e-16 EndAngle=1.5708
    g7: ArcOfCircle CenterX=6 CenterY=82 CenterZ=0 NormalX=0 NormalY=0 NormalZ=1 AngleXU=0 Radius=5 StartAngle=1.5708 EndAngle=3.14159
    g8: LineSegment StartX=0 StartY=0 StartZ=0 EndX=181.113 EndY=13.8981 EndZ=0
    g9: LineSegment StartX=181.113 StartY=13.8981 StartZ=0 EndX=180.907 EndY=16.5868 EndZ=0
    g10: LineSegment StartX=1 StartY=82 StartZ=0 EndX=1 EndY=21.4205 EndZ=0
    g11: LineSegment StartX=1 StartY=21.4205 StartZ=0 EndX=1 EndY=-1.883e-13 EndZ=0
    g12: ArcOfCircle CenterX=6 CenterY=21.4205 CenterZ=0 NormalX=0 NormalY=0 NormalZ=1 AngleXU=0 Radius=5 StartAngle=3.14159 EndAngle=4.18879
    g13: ArcOfCircle CenterX=1 CenterY=12.7602 CenterZ=0 NormalX=0 NormalY=0 NormalZ=1 AngleXU=0 Radius=5 StartAngle=1e-16 EndAngle=1.0472
    g14: LineSegment StartX=6 StartY=0 StartZ=0 EndX=6 EndY=12.7602 EndZ=0
    g15: LineSegment StartX=6 StartY=0 StartZ=0 EndX=1 EndY=-1.883e-13 EndZ=0
    g16: LineSegment StartX=1 StartY=-1.883e-13 StartZ=0 EndX=-74 EndY=-1.883e-13 EndZ=0
  constraints (46):
    c: Tangent(g7,g4) = 1.5708
    c: Coincident(g3,g4)
    c: Tangent(g6,g0) = 1.5708
    c: Coincident(g2,g5)
    c: Tangent(g5,g6) = -1.5708
    c: Coincident(g2,g1)
    c: Coincident(g1,g0)
    c: Coincident(g3,g16)
    c: Equal(g7,g6)
    c: Radius(g7) = 5
    c: PointOnObject(g4,g-3)
    c: PointOnObject(g3,g-3)
    c: PointOnObject(g0,g-3)
    c: PointOnObject(g0,g-3)
    c: Vertical(g5)
    c: DistanceX(g4,g4) = 80
    c: Vertical(g3)
    c: Horizontal(g2)
    c: Vertical(g1)
    c: Coincident(g-1,g8)
    c: Coincident(g8,g9)
    c: PointOnObject(g-4,g9)
    c: Perpendicular(g8,g9)
    c: Perpendicular(g-5,g8)
    c: Equal(g9,g-5)
    c: Coincident(g2,g9)
    c: PointOnObject(g15,g-1)
    c: Coincident(g10,g11)
    c: Vertical(g10)
    c: Vertical(g11)
    c: DistanceX(g11) = 1
    c: Coincident(g12,g10)
    c: PointOnObject(g13,g11)
    c: Coincident(g14,g15)
    c: Vertical(g14)
    c: Tangent(g14,g13) = -1.5708
    c: Tangent(g13,g12) = 1.5708
    c: Tangent(g12,g11)
    c: Radius(g13) = 5
    c: Equal(g13,g12)
    c: DistanceY(g10) = 21.4205
    c: Tangent(g7,g10) = -1.5708
    c: Coincident(g15,g16)
    c: Horizontal(g16)
    c: Coincident(g15,g11)
    c: PointOnObject(g11,g-1)
FEATURE [Sketcher::SketchObject] Sketch084
  ExternalGeometry = -> [Sketch053,Sketch050]
  FullyConstrained = true
  MapMode = 2
  Placement = pos=(164.614,1.42e-14,0) rot=(0.852419,0.369717,0.369717;1.7298rad)
  Support = -> [Sketch008]
  sketch-geometry (5):
    g0: LineSegment StartX=191.259 StartY=12.3808 StartZ=0 EndX=180.907 EndY=147.285 EndZ=0
    g1: LineSegment StartX=180.907 StartY=147.285 StartZ=0 EndX=180.907 EndY=16.5868 EndZ=0
    g2: LineSegment StartX=180.907 StartY=16.5868 StartZ=0 EndX=181.098 EndY=14.1012 EndZ=0
    g3: LineSegment StartX=181.288 StartY=11.6157 StartZ=0 EndX=191.259 EndY=12.3808 EndZ=0
    g4: LineSegment StartX=181.288 StartY=11.6157 StartZ=0 EndX=181.098 EndY=14.1012 EndZ=0
  constraints (13):
    c: Coincident(g1,g2)
    c: Vertical(g1)
    c: Coincident(g3,g0)
    c: Perpendicular(g2,g3)
    c: Distance(g0,g2) = 10
    c: Perpendicular(g3,g0)
    c: Coincident(g0,g1)
    c: Coincident(g4,g3)
    c: Coincident(g4,g2)
    c: Parallel(g4,g2)
    c: Coincident(g2,g-3)
    c: Equal(g4,g2)
    c: Coincident(g1,g-4)
FEATURE [Sketcher::SketchObject] Sketch085
  AttachmentOffset = pos=(0,0,0) rot=(0,1,0;1.5708rad)
  ExternalGeometry = -> [Sketch056,Sketch053,Sketch007]
  FullyConstrained = false
  MapMode = 7
  Placement = pos=(-164.614,-1.42e-14,0) rot=(-0.852419,0.369717,0.369717;4.55339rad)
  Support = -> [Binder]
  sketch-geometry (23):
    g0: LineSegment StartX=-181.123 StartY=15.6508 StartZ=0 EndX=-180.907 EndY=18.3267 EndZ=0
    g1: LineSegment StartX=-181.123 StartY=15.6508 StartZ=0 EndX=-2.84e-14 EndY=1 EndZ=0
    g2: LineSegment StartX=-180.907 StartY=18.3267 StartZ=0 EndX=-215.041 EndY=18.3267 EndZ=0
    g3: LineSegment StartX=-215.041 StartY=18.3267 StartZ=0 EndX=-215.041 EndY=87 EndZ=0
    g4: LineSegment StartX=-215.041 StartY=87 StartZ=0 EndX=-175.907 EndY=87 EndZ=0
    g5: LineSegment StartX=15.5786 StartY=0 StartZ=0 EndX=15.5786 EndY=87 EndZ=0
    g6: LineSegment StartX=15.5786 StartY=87 StartZ=0 EndX=-6 EndY=87 EndZ=0
    g7: LineSegment StartX=-180.907 StartY=82 StartZ=0 EndX=-180.907 EndY=18.3267 EndZ=0
    g8: ArcOfCircle CenterX=-175.907 CenterY=82 CenterZ=0 NormalX=0 NormalY=0 NormalZ=1 AngleXU=0 Radius=5 StartAngle=1.5708 EndAngle=3.14159
    g9: ArcOfCircle CenterX=-6 CenterY=82 CenterZ=0 NormalX=0 NormalY=0 NormalZ=1 AngleXU=0 Radius=5 StartAngle=4.00187e-11 EndAngle=1.5708
    g10: LineSegment StartX=-215.041 StartY=87 StartZ=0 EndX=-215.041 EndY=111.104 EndZ=0
    g11: LineSegment StartX=-215.041 StartY=111.104 StartZ=0 EndX=-174.64 EndY=111.104 EndZ=0
    g12: LineSegment StartX=-174.64 StartY=111.104 StartZ=0 EndX=-175.907 EndY=87 EndZ=0
    g13: LineSegment StartX=15.5786 StartY=87 StartZ=0 EndX=15.5786 EndY=112.942 EndZ=0
    g14: LineSegment StartX=15.5786 StartY=112.942 StartZ=0 EndX=-6 EndY=112.942 EndZ=0
    g15: LineSegment StartX=-6 StartY=112.942 StartZ=0 EndX=-6 EndY=87 EndZ=0
    g16: LineSegment StartX=-1 StartY=82 StartZ=0 EndX=-1 EndY=22.4417 EndZ=0
    g17: LineSegment StartX=-1 StartY=22.4417 StartZ=0 EndX=-1 EndY=0 EndZ=0
    g18: ArcOfCircle CenterX=-6 CenterY=22.4417 CenterZ=0 NormalX=0 NormalY=0 NormalZ=1 AngleXU=0 Radius=5 StartAngle=5.23599 EndAngle=6.28319
    g19: ArcOfCircle CenterX=-1 CenterY=13.7814 CenterZ=0 NormalX=0 NormalY=0 NormalZ=1 AngleXU=0 Radius=5 StartAngle=2.0944 EndAngle=3.14159
    g20: LineSegment StartX=-6 StartY=0 StartZ=0 EndX=-6 EndY=13.7814 EndZ=0
    g21: LineSegment StartX=-6 StartY=0 StartZ=0 EndX=-1 EndY=0 EndZ=0
    g22: LineSegment StartX=-1 StartY=0 StartZ=0 EndX=15.5786 EndY=0 EndZ=0
  constraints (58):
    c: PointOnObject(g-4,g0)
    c: Coincident(g1,g0)
    c: Coincident(g1,g-3)
    c: Parallel(g1,g-4)
    c: Parallel(g-3,g0)
    c: Equal(g-3,g0)
    c: Coincident(g2,g3)
    c: Coincident(g3,g4)
    c: Coincident(g7,g2)
    c: Horizontal(g2)
    c: Horizontal(g4)
    c: Vertical(g3)
    c: Coincident(g2,g0)
    c: Coincident(g22,g5)
    c: Coincident(g5,g6)
    c: Horizontal(g6)
    c: Vertical(g5)
    c: PointOnObject(g5,g-5)
    c: PointOnObject(g4,g-5)
    c: Vertical(g7)
    c: Tangent(g6,g9) = -1.5708
    c: Tangent(g8,g4) = 1.5708
    c: Tangent(g8,g7) = -1.5708
    c: Coincident(g9,g16) = 1.5708
    c: Equal(g9,g8)
    c: Radius(g9) = 5
    c: Coincident(g3,g10)
    c: Vertical(g10)
    c: Coincident(g10,g11)
    c: Horizontal(g11)
    c: Coincident(g11,g12)
    c: Coincident(g12,g8)
    c: Coincident(g5,g13)
    c: Vertical(g13)
    c: Coincident(g13,g14)
    c: Horizontal(g14)
    c: Coincident(g14,g15)
    c: Coincident(g15,g9)
    c: Vertical(g15)
    c: Coincident(g16,g17)
    c: Vertical(g16)
    c: Vertical(g17)
    c: DistanceX(g9) = -1
    c: PointOnObject(g21,g-1)
    c: Coincident(g18,g16)
    c: PointOnObject(g19,g17)
    c: Coincident(g20,g21)
    c: Vertical(g20)
    c: Equal(g19,g18)
    c: Radius(g19) = 5
    c: DistanceY(g16) = 22.4417
    c: Tangent(g18,g17)
    c: Tangent(g20,g19) = 1.5708
    c: Tangent(g19,g18) = 1.5708
    c: Coincident(g21,g22)
    c: Horizontal(g21)
    c: Horizontal(g22)
    c: Coincident(g21,g17)
FEATURE [Sketcher::SketchObject] Sketch086
  ExternalGeometry = -> [Sketch056,Sketch053]
  FullyConstrained = false
  MapMode = 2
  Placement = pos=(-164.614,-1.42e-14,0) rot=(0.852419,-0.369717,-0.369717;1.7298rad)
  Support = -> [Sketch085]
  sketch-geometry (5):
    g0: LineSegment StartX=-181.123 StartY=15.6508 StartZ=0 EndX=-197.283 EndY=16.9579 EndZ=0
    g1: LineSegment StartX=-197.283 StartY=16.9579 StartZ=0 EndX=-197.067 EndY=19.6338 EndZ=0
    g2: LineSegment StartX=-197.067 StartY=19.6338 StartZ=0 EndX=-180.907 EndY=18.3267 EndZ=0
    g3: LineSegment StartX=-180.907 StartY=18.3267 StartZ=0 EndX=-181.123 EndY=15.6508 EndZ=0
    g4: LineSegment StartX=-181.123 StartY=15.6508 StartZ=0 EndX=-2.84e-14 EndY=1 EndZ=0
  constraints (13):
    c: Coincident(g0,g1)
    c: Coincident(g1,g2)
    c: Coincident(g2,g3)
    c: Parallel(g0,g2)
    c: Parallel(g1,g3)
    c: Perpendicular(g1,g0)
    c: Equal(g3,g-3)
    c: Parallel(g-3,g3)
    c: Coincident(g0,g3)
    c: PointOnObject(g-4,g3)
    c: Coincident(g4,g0)
    c: Coincident(g4,g-3)
    c: Parallel(g4,g-4)
FEATURE [PartDesign::Line] DatumLine001
  AttacherType = Attacher::AttachEngineLine
  AttachmentOffset = pos=(-290.084,134.058,0) rot=(0,0,1;0rad)
  Length = 20
  MapMode = 29
  Placement = pos=(-290.084,134.058,0) rot=(0,0,1;0rad)
  ResizeMode = 0
  Support = -> [Z_Axis001]
  expr: .AttachmentOffset.Base.x = -Line.End.x
  expr: .AttachmentOffset.Base.y = Line.End.y
FEATURE [PartDesign::Point] DatumPoint001
  AttacherType = Attacher::AttachEnginePoint
  MapMode = 40
  Placement = pos=(-290.084,134.058,15.8523) rot=(0,0,1;0rad)
  Support = -> [DatumPlane,DatumLine001]
FEATURE [Sketcher::SketchObject] Sketch087  label="sink_Z_pojection"
  ExternalGeometry = -> [Binder]
  FullyConstrained = true
  MapMode = 5
  Support = -> [XY_Plane001]
  sketch-geometry (5):
    g0: LineSegment StartX=-164.614 StartY=0 StartZ=0 EndX=164.614 EndY=0 EndZ=0
    g1: LineSegment StartX=164.614 StartY=0 StartZ=0 EndX=290.084 EndY=134.058 EndZ=0
    g2: LineSegment StartX=290.084 StartY=134.058 StartZ=0 EndX=-290.084 EndY=134.058 EndZ=0
    g3: LineSegment StartX=-290.084 StartY=134.058 StartZ=0 EndX=-164.614 EndY=0 EndZ=0
    g4: LineSegment StartX=0 StartY=0 StartZ=0 EndX=0 EndY=134.058 EndZ=0
  constraints (12):
    c: Coincident(g0,g-3)
    c: Coincident(g0,g1)
    c: Coincident(g1,g-3)
    c: Coincident(g1,g2)
    c: Coincident(g2,g3)
    c: Coincident(g3,g0)
    c: Symmetric(g2,g1,g-2)
    c: Symmetric(g0,g0,g-2)
    c: Coincident(g4,g-1)
    c: PointOnObject(g4,g2)
    c: Vertical(g4)
    c: DistanceY(g4) = 134.058  'length'
FEATURE [Part::Part2DObjectPython] Line004  # Draft 2D object (typed FeaturePython)
  Area = 0
  ChamferSize = 0
  Closed = false
  End = (0,134.058,14.9712)
  FilletRadius = 0
  Length = 134.837
  MakeFace = true
  Placement = pos=(0,0,-110) rot=(0.923843,0.096466,0.370416;1.88107rad)
  Points = (2) [(39.2085,102.364,-13.9471),(107.224,76.4681,-127.456)]
  Start = (1e-16,1e-16,0.5)
  Subdivisions = 0
  expr: .End.x = (Line.End.x + Line003.End.x) / 2
  expr: .End.y = (Line.End.y + Line003.End.y) / 2
  expr: .End.z = (Line.End.z + Line003.End.z) / 2
  expr: Start = DatumPoint.Placement.Base
FEATURE [PartDesign::CoordinateSystem] Local_CS004
  AttacherType = Attacher::AttachEngine3D
  MapMode = 45
  Placement = pos=(-3.44e-14,19.4756,2.60233) rot=(0.055185,-0.052151,0.997113;1.57343rad)
  Support = -> [Line002,Line004]
FEATURE [PartDesign::CoordinateSystem] Local_CS
  AttacherType = Attacher::AttachEngine3D
  AttachmentOffset = pos=(0,0,0) rot=(0,0,1;1.5708rad)
  MapMode = 6
  Placement = pos=(2e-16,-4.1e-15,0.5) rot=(0.999598,0.028253,-0.002347;0.107573rad)
  Support = -> [Local_CS004,DatumPoint]
FEATURE [Sketcher::SketchObject] Sketch017
  FullyConstrained = false
  MapMode = 5
  Placement = pos=(2e-16,-4.1e-15,0.5) rot=(0.999598,0.028253,-0.002347;0.107573rad)
  Support = -> [Local_CS]
  sketch-geometry (6):
    g0: Circle CenterX=86.6331 CenterY=127.796 CenterZ=0 NormalX=0 NormalY=0 NormalZ=1 AngleXU=0 Radius=1.7
    g1: Circle CenterX=259.899 CenterY=127.796 CenterZ=0 NormalX=0 NormalY=0 NormalZ=1 AngleXU=0 Radius=1.7
    g2: LineSegment StartX=259.899 StartY=127.796 StartZ=0 EndX=279.899 EndY=127.796 EndZ=0
    g3: LineSegment StartX=0 StartY=127.796 StartZ=0 EndX=86.6331 EndY=127.796 EndZ=0
    g4: LineSegment StartX=86.6331 StartY=127.796 StartZ=0 EndX=173.266 EndY=127.796 EndZ=0
    g5: LineSegment StartX=173.266 StartY=127.796 StartZ=0 EndX=259.899 EndY=127.796 EndZ=0
  constraints (15):
    c: Horizontal(g0,g1)
    c: Coincident(g2,g1)
    c: Horizontal(g2)
    c: DistanceX(g2,g2) = 20
    c: PointOnObject(g3,g-2)
    c: Coincident(g3,g0)
    c: Horizontal(g3)
    c: Coincident(g4,g0)
    c: Coincident(g5,g4)
    c: Coincident(g5,g1)
    c: Horizontal(g4)
    c: Equal(g5,g4)
    c: Equal(g4,g3)
    c: Equal(g0,g1)
    c: Diameter(g0) = 3.4
FEATURE [Sketcher::SketchObject] Sketch082
  FullyConstrained = false
  MapMode = 5
  Placement = pos=(2e-16,-4.1e-15,0.5) rot=(0.999598,0.028253,-0.002347;0.107573rad)
  Support = -> [Local_CS]
  sketch-geometry (5):
    g0: ArcOfCircle CenterX=5.18e-14 CenterY=5.77e-14 CenterZ=0 NormalX=0 NormalY=0 NormalZ=1 AngleXU=0 Radius=10 StartAngle=3.79682 EndAngle=6.15786
    g1: ArcOfCircle CenterX=5.18e-14 CenterY=5.77e-14 CenterZ=0 NormalX=0 NormalY=0 NormalZ=1 AngleXU=0 Radius=10 StartAngle=6.15786 EndAngle=9.55011
    g2: ArcOfCircle CenterX=-7.93725 CenterY=-1 CenterZ=0 NormalX=0 NormalY=0 NormalZ=1 AngleXU=0 Radius=2 StartAngle=3.26692 EndAngle=4.71239
    g3: ArcOfCircle CenterX=7.93725 CenterY=-1 CenterZ=0 NormalX=0 NormalY=0 NormalZ=1 AngleXU=0 Radius=2 StartAngle=4.71239 EndAngle=6.15786
    g4: LineSegment StartX=7.93725 StartY=-3 StartZ=0 EndX=-7.93725 EndY=-3 EndZ=0
  constraints (12):
    c: Coincident(g0,g-1)
    c: Coincident(g0,g1)
    c: Coincident(g0,g1)
    c: Diameter(g0) = 20
    c: Horizontal(g4)
    c: Tangent(g4,g2) = 1.5708
    c: Tangent(g1,g2) = -1.5708
    c: Tangent(g1,g3) = -1.5708
    c: Tangent(g4,g3) = 1.5708
    c: Equal(g2,g3)
    c: Radius(g2) = 2
    c: DistanceY(g2) = -3
FEATURE [Sketcher::SketchObject] Sketch088
  ExternalGeometry = -> [Sketch007,Sketch053,Sketch055]
  FullyConstrained = true
  MapMode = 5
  Placement = pos=(0,0,0) rot=(1,0,0;1.5708rad)
  Support = -> [XZ_Plane001]
  sketch-geometry (24):
    g0: ArcOfCircle CenterX=158.53 CenterY=21.448 CenterZ=0 NormalX=0 NormalY=0 NormalZ=1 AngleXU=0 Radius=5 StartAngle=5.23599 EndAngle=6.28319
    g1: ArcOfCircle CenterX=163.53 CenterY=12.7877 CenterZ=0 NormalX=0 NormalY=0 NormalZ=1 AngleXU=0 Radius=5 StartAngle=2.0944 EndAngle=3.14159
    g2: LineSegment StartX=163.53 StartY=2.7877 StartZ=0 EndX=158.53 EndY=2.80288 EndZ=0
    g3: LineSegment StartX=158.53 StartY=2.80288 StartZ=0 EndX=158.53 EndY=12.7877 EndZ=0
    g4: LineSegment StartX=-163.53 StartY=3.78111 StartZ=0 EndX=163.53 EndY=2.7877 EndZ=0
    g5: LineSegment StartX=163.521 StartY=0.0033192 StartZ=0 EndX=-163.538 EndY=0.996732 EndZ=0
    g6: LineSegment StartX=-163.538 StartY=0.996732 StartZ=0 EndX=-163.53 EndY=3.78111 EndZ=0
    g7: LineSegment StartX=163.521 StartY=0.0033192 StartZ=0 EndX=163.53 EndY=2.7877 EndZ=0
    g8: ArcOfCircle CenterX=158.53 CenterY=82 CenterZ=0 NormalX=0 NormalY=0 NormalZ=1 AngleXU=0 Radius=5 StartAngle=6e-16 EndAngle=1.5708
    g9: LineSegment StartX=158.53 StartY=87 StartZ=0 EndX=163.786 EndY=87 EndZ=0
    g10: LineSegment StartX=163.53 StartY=87 StartZ=0 EndX=163.53 EndY=82 EndZ=0
    g11: LineSegment StartX=163.53 StartY=82 StartZ=0 EndX=163.53 EndY=21.448 EndZ=0
    g12: LineSegment StartX=163.53 StartY=21.448 StartZ=0 EndX=163.53 EndY=2.7877 EndZ=0
    g13: LineSegment StartX=163.53 StartY=2.7877 StartZ=0 EndX=163.786 EndY=87 EndZ=0
    g14: ArcOfCircle CenterX=-158.53 CenterY=82 CenterZ=0 NormalX=0 NormalY=0 NormalZ=1 AngleXU=0 Radius=5 StartAngle=1.5708 EndAngle=3.14159
    g15: LineSegment StartX=-163.53 StartY=82 StartZ=0 EndX=-163.53 EndY=87 EndZ=0
    g16: LineSegment StartX=-158.53 StartY=87 StartZ=0 EndX=-163.53 EndY=87 EndZ=0
    g17: LineSegment StartX=-163.53 StartY=3.78111 StartZ=0 EndX=-163.53 EndY=22.4414 EndZ=0
    g18: LineSegment StartX=-163.53 StartY=22.4414 StartZ=0 EndX=-163.53 EndY=82 EndZ=0
    g19: ArcOfCircle CenterX=-158.53 CenterY=22.4414 CenterZ=0 NormalX=0 NormalY=0 NormalZ=1 AngleXU=0 Radius=5 StartAngle=3.14159 EndAngle=4.18879
    g20: ArcOfCircle CenterX=-163.53 CenterY=13.7811 CenterZ=0 NormalX=0 NormalY=0 NormalZ=1 AngleXU=0 Radius=5 StartAngle=0 EndAngle=1.0472
    g21: LineSegment StartX=-158.53 StartY=13.7811 StartZ=0 EndX=-158.53 EndY=3.76592 EndZ=0
    g22: LineSegment StartX=-163.53 StartY=3.78111 StartZ=0 EndX=-158.53 EndY=3.76592 EndZ=0
    g23: LineSegment StartX=163.53 StartY=12.7877 StartZ=0 EndX=-163.53 EndY=13.7811 EndZ=0
  constraints (67):
    c: Coincident(g2,g3)
    c: Vertical(g3)
    c: Coincident(g5,g6)
    c: Coincident(g6,g4)
    c: Parallel(g4,g5)
    c: Perpendicular(g6,g5)
    c: Perpendicular(g-5,g5)
    c: PointOnObject(g-4,g6)
    c: Coincident(g17,g4)
    c: PointOnObject(g15,g-3)
    c: Coincident(g7,g5)
    c: Coincident(g7,g4)
    c: Perpendicular(g5,g7)
    c: PointOnObject(g-4,g7)
    c: PointOnObject(g-5,g5)
    c: PointOnObject(g-5,g4)
    c: PointOnObject(g8,g-3)
    c: Coincident(g9,g8)
    c: Tangent(g9,g8)
    c: Coincident(g12,g4)
    c: Coincident(g10,g11)
    c: Coincident(g11,g12)
    c: Coincident(g0,g11)
    c: Tangent(g0,g12)
    c: Tangent(g8,g11) = 1.5708
    c: Vertical(g11)
    c: Vertical(g10)
    c: Vertical(g12)
    c: Tangent(g3,g1) = 1.5708
    c: Tangent(g1,g0) = 1.5708
    c: Equal(g1,g0)
    c: PointOnObject(g2,g4)
    c: Coincident(g2,g4)
    c: Coincident(g13,g2)
    c: Parallel(g-5,g13)
    c: PointOnObject(g13,g-3)
    c: Coincident(g9,g13)
    c: PointOnObject(g10,g9)
    c: Radius(g8) = 5
    c: Radius(g1) = 5
    c: PointOnObject(g0,g3)
    c: Distance(g2,g1) = 10
    c: PointOnObject(g14,g-3)
    c: Coincident(g18,g15)
    c: Vertical(g15)
    c: Coincident(g18,g14) = 1.5708
    c: Coincident(g16,g14)
    c: Coincident(g16,g15)
    c: Tangent(g16,g14)
    c: Equal(g14,g8)
    c: Coincident(g17,g18)
    c: Vertical(g17)
    c: Vertical(g18)
    c: PointOnObject(g20,g17)
    c: PointOnObject(g21,g4)
    c: Coincident(g22,g17)
    c: Coincident(g22,g21)
    c: Tangent(g19,g17) = 1.5708
    c: Tangent(g20,g19) = 1.5708
    c: Equal(g20,g19)
    c: Tangent(g21,g20) = 1.5708
    c: Coincident(g23,g1)
    c: Coincident(g23,g20)
    c: Parallel(g23,g4)
    c: Equal(g20,g1)
    c: Vertical(g21)
    c: Equal(g15,g16)
FEATURE [Sketcher::SketchObject] Sketch089
  ExternalGeometry = -> [Sketch053,Sketch055,Sketch007]
  FullyConstrained = true
  MapMode = 5
  Placement = pos=(0,0,0) rot=(1,0,0;1.5708rad)
  Support = -> [XZ_Plane001]
  sketch-geometry (6):
    g0: LineSegment StartX=164.623 StartY=2.78438 StartZ=0 EndX=-163.53 EndY=3.78111 EndZ=0
    g1: LineSegment StartX=-163.53 StartY=3.78111 StartZ=0 EndX=-163.538 EndY=0.996732 EndZ=0
    g2: LineSegment StartX=-163.538 StartY=0.996732 StartZ=0 EndX=164.614 EndY=3.61e-13 EndZ=0
    g3: LineSegment StartX=-163.53 StartY=3.78111 StartZ=0 EndX=-163.53 EndY=87 EndZ=0
    g4: LineSegment StartX=-163.53 StartY=3.78111 StartZ=0 EndX=-163.277 EndY=87 EndZ=0
    g5: LineSegment StartX=-163.277 StartY=87 StartZ=0 EndX=-163.53 EndY=87 EndZ=0
  constraints (16):
    c: Coincident(g-4,g0)
    c: Coincident(g0,g1)
    c: Coincident(g1,g2)
    c: Coincident(g2,g-4)
    c: Perpendicular(g2,g-4)
    c: Perpendicular(g0,g-4)
    c: Perpendicular(g1,g2)
    c: PointOnObject(g-3,g1)
    c: Coincident(g3,g0)
    c: Vertical(g3)
    c: PointOnObject(g3,g-5)
    c: Coincident(g4,g3)
    c: PointOnObject(g4,g-5)
    c: Coincident(g5,g4)
    c: Coincident(g5,g3)
    c: Parallel(g4,g1)
FEATURE [PartDesign::Pad] Pad018
  BaseFeature = -> Pad015
  Direction = (0,-1,2e-16)
  Length = 0.5
  Length2 = 10
  Profile = -> Sketch089
  ReferenceAxis = -> Sketch089 [N_Axis]
  Reversed = true
  Type = 0
  expr: Length = <<sink_BaseBend>>.thickness
FEATURE [PartDesign::Pocket] Pocket054
  BaseFeature = -> Pad018
  Direction = (0,1,-2e-16)
  Length = 5
  Length2 = 5
  Midplane = true
  Profile = -> Sketch007
  ReferenceAxis = -> Sketch007 [N_Axis]
  Refine = true
  Type = 1
FEATURE [PartDesign::FeaturePython] CornerRelief  # WARN: FeaturePython — macro-defined, semantics opaque (R4)
  BaseFeature = -> Pocket054
  ReliefSketch = 0
  Size = 10
  SizeRatio = 1
  XOffset = 0
  YOffset = 0
  baseObject = -> Pocket054 [Edge8,Edge21]
  kfactor = 0.5
FEATURE [PartDesign::FeaturePython] CornerRelief001  # WARN: FeaturePython — macro-defined, semantics opaque (R4)
  BaseFeature = -> CornerRelief
  ReliefSketch = 0
  Size = 10
  SizeRatio = 1
  XOffset = 0
  YOffset = 0
  baseObject = -> CornerRelief [Edge31,Edge32]
  kfactor = 0.5
  expr: Size = CornerRelief.Size
  expr: SizeRatio = CornerRelief.SizeRatio
FEATURE [PartDesign::FeaturePython] SketchOnSheet  # WARN: FeaturePython — macro-defined, semantics opaque (R4)
  BaseFeature = -> CornerRelief001
  Sketch = -> Sketch082
  baseObject = -> CornerRelief001 [Face13]
  kfactor = 0.5
FEATURE [PartDesign::Pad] Pad016
  BaseFeature = -> SketchOnSheet
  Direction = (0.68133,0.727966,0.0765123)
  Length = 10
  Length2 = 10
  Profile = -> Sketch050
  ReferenceAxis = -> Sketch050 [N_Axis]
  Type = 4
FEATURE [PartDesign::Pad] Pad017
  BaseFeature = -> Pad016
  Direction = (0.681109,-0.72773,-0.0806251)
  Length = 10
  Length2 = 10
  Profile = -> Sketch052
  ReferenceAxis = -> Sketch052 [N_Axis]
  Reversed = true
  Type = 0
FEATURE [PartDesign::Pocket] Pocket055
  BaseFeature = -> Pad017
  Direction = (-0.730107,0.683333,-2e-16)
  Length = 5
  Length2 = 5
  Profile = -> Sketch084
  ReferenceAxis = -> Sketch084 [N_Axis]
  Type = 0
FEATURE [PartDesign::SubShapeBinder] Binder044  label="datum"
  BindCopyOnChange = 0
  BindMode = 0
  ClaimChildren = true
  Context = -> Part [Body001.Binder044.]
  Fuse = false
  MakeFace = true
  OffsetFill = false
  OffsetIntersection = false
  OffsetJoinType = 0
  OffsetOpenResult = false
  PartialLoad = false
  Relative = false
  Support = -> [Line,Local_CS,Line002,Line003,DatumPoint,DatumLine,DatumPlane,DatumLine001,DatumPoint001,Line004]
  _Version = 2
FEATURE [Sketcher::SketchObject] Unfold_Sketch_bends001
  FullyConstrained = false
  sketch-geometry (4):
    g0: LineSegment StartX=-6.36943 StartY=171.059 StartZ=0 EndX=-132.044 EndY=287.253 EndZ=0
    g1: LineSegment StartX=1.94899 StartY=-154.34 StartZ=0 EndX=1.51044 EndY=-9.95673 EndZ=0
    g2: LineSegment StartX=-5.33257 StartY=-171.115 StartZ=0 EndX=-130.299 EndY=-288.152 EndZ=0
    g3: LineSegment StartX=1.44993 StartY=9.96269 StartZ=0 EndX=1.01143 EndY=154.331 EndZ=0
FEATURE [PartDesign::SubShapeBinder] Binder045
  BindCopyOnChange = 0
  BindMode = 0
  ClaimChildren = false
  Context = -> Body026 [Binder045.]
  Fuse = false
  MakeFace = true
  OffsetFill = false
  OffsetIntersection = false
  OffsetJoinType = 0
  OffsetOpenResult = false
  PartialLoad = false
  Relative = true
  Support = -> [Unfold_Sketch_bends001]
  _Version = 2
FEATURE [Sketcher::SketchObject] Sketch090
  ExternalGeometry = -> [Binder045]
  FullyConstrained = true
  MapMode = 5
  Support = -> [XY_Plane029]
  sketch-geometry (6):
    g0: Circle CenterX=-130.299 CenterY=-288.152 CenterZ=0 NormalX=0 NormalY=0 NormalZ=1 AngleXU=0 Radius=0.75
    g1: Circle CenterX=-5.33257 CenterY=-171.115 CenterZ=0 NormalX=0 NormalY=0 NormalZ=1 AngleXU=0 Radius=0.75
    g2: Circle CenterX=1.94899 CenterY=-154.34 CenterZ=0 NormalX=0 NormalY=0 NormalZ=1 AngleXU=0 Radius=0.75
    g3: Circle CenterX=1.01143 CenterY=154.331 CenterZ=0 NormalX=0 NormalY=0 NormalZ=1 AngleXU=0 Radius=0.75
    g4: Circle CenterX=-6.36943 CenterY=171.059 CenterZ=0 NormalX=0 NormalY=0 NormalZ=1 AngleXU=0 Radius=0.75
    g5: Circle CenterX=-132.044 CenterY=287.253 CenterZ=0 NormalX=0 NormalY=0 NormalZ=1 AngleXU=0 Radius=0.75
  constraints (12):
    c: Coincident(g0,g-5)
    c: Coincident(g1,g-5)
    c: Coincident(g2,g-6)
    c: Coincident(g3,g-3)
    c: Coincident(g4,g-4)
    c: Coincident(g5,g-4)
    c: Equal(g5,g4)
    c: Equal(g5,g3)
    c: Equal(g5,g2)
    c: Equal(g5,g1)
    c: Equal(g5,g0)
    c: Diameter(g5) = 1.5
FEATURE [PartDesign::Pocket] Pocket056
  BaseFeature = -> Pocket055
  Direction = (-0.730107,0.683333,-1e-16)
  Length = 5
  Length2 = 5
  Profile = -> Sketch008
  ReferenceAxis = -> Sketch008 [N_Axis]
  Type = 2
FEATURE [PartDesign::Pocket] Pocket058
  BaseFeature = -> Pocket056
  Direction = (0.730107,0.683333,1e-16)
  Length = 5
  Length2 = 5
  Profile = -> Sketch085
  ReferenceAxis = -> Sketch085 [N_Axis]
  Type = 2
FEATURE [PartDesign::Pocket] Pocket057
  BaseFeature = -> Pocket058
  Direction = (0.730107,0.683333,2e-16)
  Length = 5
  Length2 = 5
  Profile = -> Sketch086
  ReferenceAxis = -> Sketch086 [N_Axis]
  Type = 1
FEATURE [PartDesign::Pocket] Pocket059
  BaseFeature = -> Pocket057
  Direction = (0,1,-2e-16)
  Length = 5
  Length2 = 5
  Profile = -> Sketch088
  ReferenceAxis = -> Sketch088 [N_Axis]
  Type = 2
FEATURE [PartDesign::Pocket] Pocket053
  BaseFeature = -> Pocket059
  Direction = (-0.00301985,0.107323,-0.99422)
  Length = 5
  Length2 = 5
  Midplane = true
  Profile = -> Sketch017
  ReferenceAxis = -> Sketch017 [N_Axis]
  Type = 1
FEATURE [PartDesign::Pocket] Pocket060
  BaseFeature = -> Pocket053
  Direction = (0,1,-2e-16)
  Length = 5
  Length2 = 5
  Midplane = true
  Profile = -> Sketch007
  ReferenceAxis = -> Sketch007 [N_Axis]
  Type = 1
FEATURE [PartDesign::Mirrored] Mirrored
  BaseFeature = -> Pocket060
  MirrorPlane = -> Sketch017 [V_Axis]
  Originals = -> [Pocket053]
  Refine = true
FEATURE [PartDesign::Boolean] Boolean001
  BaseFeature = -> Mirrored
  Group = -> [Compound002]
  Refine = true
  Type = 1
  expr: Group = <<sink_cut1>>._self
FEATURE [PartDesign::Body] Body001  label="sink_material_0.30ansi"
  Group = -> [Sketch001,BaseBend001,Sketch054,Sketch055,Sketch056,Pad013,Pad014,Pad015,Sketch004,Line,Binder,Sketch006,Line002,Line003,Sketch007,Sketch008,DatumPoint,Sketch050,DatumLine,DatumPlane,Sketch051,Sketch052,Sketch053,Sketch081,DatumLine001,DatumPoint001,Sketch089,Pad018,Pocket054,CornerRelief,CornerRelief001,Sketch082,SketchOnSheet,Pad016,Pad017,Sketch084,Pocket055,Pocket056,Sketch085,Sketch086,+14 more]
  Origin = -> Origin001
  Tip = -> Mirrored
FEATURE [App::Part] Part  label="sink"
  Group = -> [Body001,Body006]
  Origin = -> Origin007
  Placement = pos=(0,0,110) rot=(0,0,1;0rad)
FEATURE [TechDraw::DrawViewPart] View
  CoarseView = false
  Direction = (0,1,0)
  Focus = 100
  HardHidden = false
  IsoCount = 0
  IsoHidden = false
  IsoVisible = false
  LockPosition = false
  Perspective = false
  Rotation = 0
  Scale = 0.5
  ScaleType = 2
  ScrubCount = 0
  SeamHidden = false
  SeamVisible = true
  SmoothHidden = false
  SmoothVisible = true
  Source = -> [Body001]
  X = 148.5
  XDirection = (-1,0,0)
  Y = 183
FEATURE [TechDraw::DrawViewPart] View001
  CoarseView = false
  Direction = (-0.68133,0.727966,0.076512)
  Focus = 100
  HardHidden = false
  IsoCount = 0
  IsoHidden = false
  IsoVisible = false
  LockPosition = false
  Perspective = false
  Rotation = 0
  Scale = 0.5
  ScaleType = 2
  ScrubCount = 0
  SeamHidden = false
  SeamVisible = true
  SmoothHidden = false
  SmoothVisible = true
  Source = -> [Body001]
  X = 108.5
  XDirection = (-0.730106,-0.683333,-2.10082e-07)
  Y = 105
FEATURE [TechDraw::DrawViewPart] View002
  CoarseView = false
  Direction = (-1,0,0)
  Focus = 100
  HardHidden = false
  IsoCount = 0
  IsoHidden = false
  IsoVisible = false
  LockPosition = false
  Perspective = false
  Rotation = 0
  Scale = 0.5
  ScaleType = 2
  ScrubCount = 0
  SeamHidden = false
  SeamVisible = true
  SmoothHidden = false
  SmoothVisible = true
  Source = -> [Body001]
  X = 258.5
  XDirection = (0,-1,-6e-06)
  Y = 105
FEATURE [TechDraw::DrawPage] Page
  KeepUpdated = true
  NextBalloonIndex = 1
  ProjectionType = 0
  Template = -> Template
  Views = -> [View,View001,View002]
FEATURE [TechDraw::DrawViewPart] View003
  CoarseView = false
  Direction = (0,1,0)
  Focus = 100
  HardHidden = false
  IsoCount = 0
  IsoHidden = false
  IsoVisible = false
  LockPosition = false
  Perspective = false
  Rotation = 0
  Scale = 0.5
  ScaleType = 2
  ScrubCount = 0
  SeamHidden = false
  SeamVisible = true
  SmoothHidden = false
  SmoothVisible = true
  Source = -> [Boolean001]
  X = 148.5
  XDirection = (-1,0,0)
  Y = 45
FEATURE [TechDraw::DrawViewPart] View004
  CoarseView = false
  Direction = (0.68133,0.727966,0.0765123)
  Focus = 100
  HardHidden = false
  IsoCount = 0
  IsoHidden = false
  IsoVisible = false
  LockPosition = false
  Perspective = false
  Rotation = 0
  Scale = 0.5
  ScaleType = 1
  ScrubCount = 0
  SeamHidden = false
  SeamVisible = true
  SmoothHidden = false
  SmoothVisible = true
  Source = -> [Boolean001]
  X = 108.5
  XDirection = (-0.730106,0.683333,2.10082e-07)
  Y = 105
FEATURE [TechDraw::DrawViewPart] View005
  CoarseView = false
  Direction = (-0.681109,0.72773,0.0806251)
  Focus = 100
  HardHidden = false
  IsoCount = 0
  IsoHidden = false
  IsoVisible = false
  LockPosition = false
  Perspective = false
  Rotation = 0
  Scale = 0.5
  ScaleType = 1
  ScrubCount = 0
  SeamHidden = false
  SeamVisible = true
  SmoothHidden = false
  SmoothVisible = true
  Source = -> [Boolean001]
  X = 108.5
  XDirection = (-0.730107,-0.683334,7.5335e-08)
  Y = 175
FEATURE [TechDraw::DrawViewDimension] Dimension
  AngleOverride = false
  Arbitrary = false
  ArbitraryTolerances = false
  EqualTolerance = true
  ExtensionAngle = 0
  FormatSpec = %.2w
  FormatSpecOverTolerance = %+.2w
  FormatSpecUnderTolerance = %+.2w
  Inverted = false
  LineAngle = 0
  LockPosition = false
  MeasureType = 1
  OverTolerance = 0
  References2D = -> [View004]
  Rotation = 0
  ScaleType = 0
  TheoreticalExact = false
  Type = 6
  UnderTolerance = 0
  X = -90.0916
  Y = -2.51832
FEATURE [TechDraw::DrawViewDimension] Dimension001
  AngleOverride = false
  Arbitrary = false
  ArbitraryTolerances = false
  EqualTolerance = true
  ExtensionAngle = 0
  FormatSpec = %.2w
  FormatSpecOverTolerance = %+.2w
  FormatSpecUnderTolerance = %+.2w
  Inverted = false
  LineAngle = 0
  LockPosition = false
  MeasureType = 1
  OverTolerance = 0
  References2D = -> [View005]
  Rotation = 0
  ScaleType = 0
  TheoreticalExact = false
  Type = 6
  UnderTolerance = 0
  X = 90.6146
  Y = -1.60021
FEATURE [Part::Feature] Unfold002
  Placement = pos=(0,0,0) rot=(0.57735,0.57735,0.57735;2.0944rad)
  shape: bbox 220.2 x 682.9 x 0.55 mm, 56 faces (baked)
FEATURE [PartDesign::FeatureAdditivePython] PDW_Add  # link proxy (typed FeaturePython)
  Body = Body026
  ClaimChildren = true
  EditPlacementAdjustments = false
  Enabled = 1
  LinkedObject = -> Unfold002
  MeshTolerance = 0.1
  PatternBaseOffset = 0
  PatternBaseScale = 1
  PatternBaseScaleXYZ = (1,1,1)
  PatternOffsetCut = false
  PatternOffsetIntersection = false
  PatternOffsetJoin = 0
  PatternOffsetMode = 0
  PatternOffsetSelfIntersection = false
  PatternOperation = 0
  PatternOperationDefault = None
  PatternScaleCut = false
  PatternShapeOffset = 0
  PatternShapeScale = 1
  PatternShapeScaleXYZ = (1,1,1)
  PatternToolOffset = 0
  PatternToolScale = 1
  PatternToolScaleXYZ = (1,1,1)
  RefineMesh = true
  ShapeManagement = 0
  ShowMeshProps = false
  ShowOffsetProps = false
  ShowScaleProps = false
  ShowWarnings = true
  TipBaseOffset = 0
  TipBaseScale = 1
  TipBaseScaleXYZ = (1,1,1)
  TipOffsetCut = false
  TipOffsetIntersection = false
  TipOffsetJoin = 0
  TipOffsetMode = 0
  TipOffsetSelfIntersection = false
  TipOperation = 0
  TipOperationDefault = Fuse
  TipScaleCut = false
  TipShapeOffset = 0
  TipShapeScale = 1
  TipShapeScaleXYZ = (1,1,1)
  TipTool = -> Unfold002
  TipToolOffset = 0
  TipToolScale = 1
  TipToolScaleXYZ = (1,1,1)
  Type = Additive
  UsePatternBaseAddSubShape = false
  UsePatternToolAddSubShape = false
  UseTipBaseAddSubShape = false
  UseTipToolAddSubShape = false
  Version = 0.2023.08.13
FEATURE [PartDesign::Pocket] Pocket061
  BaseFeature = -> PDW_Add
  Direction = (0,0,-1)
  Length = 5
  Length2 = 5
  Midplane = true
  Profile = -> Sketch090
  ReferenceAxis = -> Sketch090 [N_Axis]
  Type = 1
FEATURE [PartDesign::Body] Body026
  Group = -> [PDW_Add,Binder045,Sketch090,Pocket061,Unfold002]
  Origin = -> Origin029
  Tip = -> PDW_Add
FEATURE [Sketcher::SketchObject] Unfold_Sketch002
  FullyConstrained = false
  sketch-geometry (56):
    g0: LineSegment StartX=6.66044 StartY=172.397 StartZ=0 EndX=50.8153 EndY=228.172 EndZ=0
    g1: ArcOfCircle CenterX=46.8951 CenterY=231.276 CenterZ=0 NormalX=0 NormalY=0 NormalZ=1 AngleXU=2.47196 Radius=5 StartAngle=3.14159 EndAngle=4.71239
    g2: LineSegment StartX=-130.842 StartY=288.553 StartZ=0 EndX=-90.2406 EndY=339.84 EndZ=0
    g3: ArcOfCircle CenterX=-86.3204 CenterY=336.736 CenterZ=0 NormalX=0 NormalY=0 NormalZ=1 AngleXU=2.47196 Radius=5 StartAngle=4.71239 EndAngle=6.28319
    g4: LineSegment StartX=-83.2169 StartY=340.657 StartZ=0 EndX=49.9986 EndY=235.196 EndZ=0
    g5: BSplineCurve PolesCount=15 KnotsCount=13 Degree=3 IsPeriodic=0
    g6: BSplineCurve PolesCount=15 KnotsCount=13 Degree=3 IsPeriodic=0
    g7: BSplineCurve PolesCount=15 KnotsCount=13 Degree=3 IsPeriodic=0
    g8: BSplineCurve PolesCount=15 KnotsCount=13 Degree=3 IsPeriodic=0
    g9: LineSegment StartX=-89.4559 StartY=-339.272 StartZ=0 EndX=-129.092 EndY=-289.44 EndZ=0
    g10: ArcOfCircle CenterX=-85.5428 CenterY=-336.16 CenterZ=0 NormalX=0 NormalY=0 NormalZ=1 AngleXU=0.671931 Radius=5 StartAngle=3.14159 EndAngle=4.71239
    g11: LineSegment StartX=50.5424 StartY=-234.306 StartZ=0 EndX=-82.4303 EndY=-340.073 EndZ=0
    g12: ArcOfCircle CenterX=47.4299 CenterY=-230.393 CenterZ=0 NormalX=0 NormalY=0 NormalZ=1 AngleXU=0.671931 Radius=5 StartAngle=4.71239 EndAngle=6.28319
    g13: ArcOfCircle CenterX=1.91015 CenterY=-164.22 CenterZ=0 NormalX=0 NormalY=0 NormalZ=1 AngleXU=1.57416 Radius=10 StartAngle=2.50587 EndAngle=3.7533
    g14: LineSegment StartX=51.343 StartY=-227.281 StartZ=0 EndX=7.68031 EndY=-172.387 EndZ=0
    g15: LineSegment StartX=-129.092 StartY=-289.44 StartZ=0 EndX=-131.506 EndY=-286.864 EndZ=0
    g16: BSplineCurve PolesCount=15 KnotsCount=13 Degree=3 IsPeriodic=0
    g17: LineSegment StartX=-133.245 StartY=285.953 StartZ=0 EndX=-131.506 EndY=-286.864 EndZ=0
    g18: ArcOfCircle CenterX=2.0224 CenterY=-164.339 CenterZ=0 NormalX=0 NormalY=0 NormalZ=1 AngleXU=1.57416 Radius=10 StartAngle=0.185465 EndAngle=2.13429
    g19: ArcOfCircle CenterX=1.85456 CenterY=-164.34 CenterZ=0 NormalX=0 NormalY=0 NormalZ=1 AngleXU=1.57416 Radius=10 StartAngle=4.79012 EndAngle=6.08874
    g20: BSplineCurve PolesCount=15 KnotsCount=13 Degree=3 IsPeriodic=0
    g21: ArcOfCircle CenterX=1.02906 CenterY=164.331 CenterZ=0 NormalX=0 NormalY=0 NormalZ=1 AngleXU=1.57416 Radius=10 StartAngle=1.00751 EndAngle=2.95497
    g22: BSplineCurve PolesCount=15 KnotsCount=13 Degree=3 IsPeriodic=0
    g23: ArcOfEllipse CenterX=0.864844 CenterY=164.399 CenterZ=0 NormalX=0 NormalY=0 NormalZ=1 MajorRadius=10.063 MinorRadius=10.062 AngleXU=-1.5627 StartAngle=0.186881 EndAngle=1.47621
    g24: LineSegment StartX=82 StartY=163.53 StartZ=0 EndX=10.8291 EndY=163.53 EndZ=0
    g25: ArcOfCircle CenterX=82 CenterY=158.53 CenterZ=0 NormalX=0 NormalY=0 NormalZ=1 AngleXU=1.5708 Radius=5 StartAngle=4.71239 EndAngle=6.28319
    g26: LineSegment StartX=87 StartY=158.53 StartZ=0 EndX=87 EndY=-158.53 EndZ=0
    g27: ArcOfCircle CenterX=82 CenterY=-158.53 CenterZ=0 NormalX=0 NormalY=0 NormalZ=1 AngleXU=1.5708 Radius=5 StartAngle=3.1416 EndAngle=4.71238
    g28: LineSegment StartX=11.8217 StartY=-163.53 StartZ=0 EndX=82 EndY=-163.53 EndZ=0
    g29: ArcOfCircle CenterX=2.46037 CenterY=0.00595443 CenterZ=0 NormalX=0 NormalY=0 NormalZ=1 AngleXU=1.57374 Radius=10 StartAngle=0.282258 EndAngle=2.85951
    g30: ArcOfEllipse CenterX=2.29408 CenterY=-0.0613744 CenterZ=0 NormalX=0 NormalY=0 NormalZ=1 MajorRadius=10.0624 MinorRadius=10.0615 AngleXU=1.58153 StartAngle=6.15102 EndAngle=6.17692
    g31: ArcOfEllipse CenterX=3.22714 CenterY=7.88921 CenterZ=0 NormalX=0 NormalY=0 NormalZ=1 MajorRadius=2.0427 MinorRadius=2.03846 AngleXU=1.56344 StartAngle=4.7502 EndAngle=6.15085
    g32: LineSegment StartX=5.26912 StartY=7.95151 StartZ=0 EndX=5.31592 EndY=-7.92293 EndZ=0
    g33: ArcOfEllipse CenterX=3.31931 CenterY=-7.91289 CenterZ=0 NormalX=0 NormalY=0 NormalZ=1 MajorRadius=2.00041 MinorRadius=1.99991 AngleXU=1.57846 StartAngle=3.25962 EndAngle=4.69974
    g34: ArcOfEllipse CenterX=2.2925 CenterY=0.00881049 CenterZ=0 NormalX=0 NormalY=0 NormalZ=1 MajorRadius=9.99999 MinorRadius=9.99978 AngleXU=1.58071 StartAngle=3.23403 EndAngle=3.25991
    g35: Circle CenterX=-125.591 CenterY=86.262 CenterZ=0 NormalX=0 NormalY=0 NormalZ=1 AngleXU=1.57374 Radius=1.7
    g36: Circle CenterX=-125.08 CenterY=-87.0036 CenterZ=0 NormalX=0 NormalY=0 NormalZ=1 AngleXU=-1.56785 Radius=1.7
    g37: Circle CenterX=81 CenterY=0 CenterZ=0 NormalX=0 NormalY=0 NormalZ=1 AngleXU=1.5708 Radius=1.7
    g38: Circle CenterX=31 CenterY=-7.1e-15 CenterZ=0 NormalX=0 NormalY=0 NormalZ=1 AngleXU=1.5708 Radius=1.7
    g39: Circle CenterX=81 CenterY=154.614 CenterZ=0 NormalX=0 NormalY=0 NormalZ=1 AngleXU=1.5708 Radius=1.7
    g40: Circle CenterX=46.8472 CenterY=-229.579 CenterZ=0 NormalX=0 NormalY=0 NormalZ=1 AngleXU=-2.46966 Radius=1.7
    g41: Circle CenterX=-86.1984 CenterY=-335.404 CenterZ=0 NormalX=0 NormalY=0 NormalZ=1 AngleXU=-2.46966 Radius=1.7
    g42: Circle CenterX=-117.323 CenterY=-296.273 CenterZ=0 NormalX=0 NormalY=0 NormalZ=1 AngleXU=-2.46966 Radius=1.7
    g43: Circle CenterX=81 CenterY=-154.614 CenterZ=0 NormalX=0 NormalY=0 NormalZ=1 AngleXU=-1.5708 Radius=1.7
    g44: Circle CenterX=-124.569 CenterY=-260.269 CenterZ=0 NormalX=0 NormalY=0 NormalZ=1 AngleXU=-1.56785 Radius=1.7
    g45: Circle CenterX=-126.102 CenterY=259.527 CenterZ=0 NormalX=0 NormalY=0 NormalZ=1 AngleXU=1.57374 Radius=1.7
    g46: Circle CenterX=-86.9743 CenterY=335.979 CenterZ=0 NormalX=0 NormalY=0 NormalZ=1 AngleXU=2.47196 Radius=1.7
    g47: Circle CenterX=46.3142 CenterY=230.46 CenterZ=0 NormalX=0 NormalY=0 NormalZ=1 AngleXU=2.47196 Radius=1.7
    g48: Circle CenterX=-118.009 CenterY=296.776 CenterZ=0 NormalX=0 NormalY=0 NormalZ=1 AngleXU=2.47196 Radius=1.7
    g49: Circle CenterX=31 CenterY=154.614 CenterZ=0 NormalX=0 NormalY=0 NormalZ=1 AngleXU=1.5708 Radius=1.7
    g50: Circle CenterX=31 CenterY=-154.614 CenterZ=0 NormalX=0 NormalY=0 NormalZ=1 AngleXU=-1.5708 Radius=1.7
    g51: Circle CenterX=15.7223 CenterY=-190.448 CenterZ=0 NormalX=0 NormalY=0 NormalZ=1 AngleXU=-2.46966 Radius=1.7
    g52: Circle CenterX=15.2793 CenterY=191.257 CenterZ=0 NormalX=0 NormalY=0 NormalZ=1 AngleXU=2.47196 Radius=1.7
    g53: LineSegment StartX=-133.245 StartY=285.953 StartZ=0 EndX=-130.842 EndY=288.553 EndZ=0
    g54: ArcOfCircle CenterX=0.917294 CenterY=164.21 CenterZ=0 NormalX=0 NormalY=0 NormalZ=1 AngleXU=1.57416 Radius=10 StartAngle=0 EndAngle=0.634917
    g55: ArcOfCircle CenterX=0.917294 CenterY=164.21 CenterZ=0 NormalX=0 NormalY=0 NormalZ=1 AngleXU=1.57416 Radius=10 StartAngle=5.66805 EndAngle=6.28319
FEATURE [Sketcher::SketchObject] Unfold_Sketch_Outline002
  FullyConstrained = true
FEATURE [App::DocumentObjectGroup] Group001  label="sink_unfold"
  Group = -> [Unfold,Unfold_Sketch,Unfold_Sketch_Outline,Unfold_Sketch_bends,Body010,Page,Unfold_Sketch_bends001,Body026,Unfold_Sketch002,Unfold_Sketch_Outline002]
FEATURE [PartDesign::SubShapeBinder] Binder046
  BindCopyOnChange = 0
  BindMode = 0
  ClaimChildren = false
  Context = -> Body024 [Binder046.]
  Fuse = false
  MakeFace = true
  OffsetFill = false
  OffsetIntersection = false
  OffsetJoinType = 0
  OffsetOpenResult = false
  PartialLoad = false
  Relative = true
  Support = -> [Sketch005]
  _Version = 2
FEATURE [Sketcher::SketchObject] Sketch091
  ExternalGeometry = -> [Binder046]
  FullyConstrained = true
  MapMode = 5
  Support = -> [XY_Plane027]
  sketch-geometry (5):
    g0: LineSegment StartX=257.917 StartY=124.058 StartZ=0 EndX=277.917 EndY=124.058 EndZ=0
    g1: LineSegment StartX=277.917 StartY=124.058 StartZ=0 EndX=277.917 EndY=121.058 EndZ=0
    g2: LineSegment StartX=277.917 StartY=121.058 StartZ=0 EndX=268.578 EndY=111.08 EndZ=0
    g3: LineSegment StartX=268.578 StartY=111.08 StartZ=0 EndX=257.917 EndY=121.058 EndZ=0
    g4: LineSegment StartX=257.917 StartY=121.058 StartZ=0 EndX=257.917 EndY=124.058 EndZ=0
  constraints (16):
    c: Horizontal(g0)
    c: Coincident(g0,g1)
    c: PointOnObject(g1,g-3)
    c: Vertical(g1)
    c: Coincident(g1,g2)
    c: PointOnObject(g2,g-3)
    c: Coincident(g2,g3)
    c: Coincident(g4,g0)
    c: DistanceX(g0,g0) = 20
    c: DistanceY(g1,g1) = 3
    c: DistanceY(g0,g-3) = 10
    c: Coincident(g3,g4)
    c: Vertical(g4)
    c: Perpendicular(g2,g3)
    c: Horizontal(g3,g1)
    c: DistanceY(g0) = 124.058  'face_offset'
FEATURE [PartDesign::Pad] Pad019
  Direction = (0,0,1)
  Length = 105
  Length2 = 10
  Profile = -> Sketch091
  ReferenceAxis = -> Sketch091 [N_Axis]
  Type = 0
FEATURE [Sketcher::SketchObject] Sketch092
  AttachmentOffset = pos=(0,0,-124.058) rot=(0,0,1;0rad)
  ExternalGeometry = -> [Sketch091]
  FullyConstrained = true
  MapMode = 5
  Placement = pos=(0,124.058,-2.75e-14) rot=(1,0,0;1.5708rad)
  Support = -> [XZ_Plane027]
  expr: .AttachmentOffset.Base.z = -Sketch091.Constraints.face_offset
  sketch-geometry (3):
    g0: Circle CenterX=267.917 CenterY=52.5 CenterZ=0 NormalX=0 NormalY=0 NormalZ=1 AngleXU=0 Radius=9.95
    g1: LineSegment StartX=257.917 StartY=-2.75e-14 StartZ=0 EndX=267.917 EndY=52.5 EndZ=0
    g2: LineSegment StartX=267.917 StartY=52.5 StartZ=0 EndX=277.917 EndY=-2.84e-14 EndZ=0
  constraints (7):
    c: Diameter(g0) = 19.9
    c: Coincident(g-3,g1)
    c: Coincident(g1,g0)
    c: Coincident(g1,g2)
    c: Coincident(g2,g-3)
    c: Equal(g2,g1)
    c: DistanceY(g0) = 52.5
FEATURE [PartDesign::Pocket] Pocket062
  BaseFeature = -> Pad019
  Direction = (0,1,-2e-16)
  Length = 3
  Length2 = 5
  Profile = -> Sketch092
  ReferenceAxis = -> Sketch092 [N_Axis]
  Reversed = true
  Type = 0
FEATURE [Sketcher::SketchObject] Sketch093
  ExternalGeometry = -> [Sketch092]
  FullyConstrained = true
  MapMode = 5
  Placement = pos=(0,0,0) rot=(1,0,0;1.5708rad)
  Support = -> [XZ_Plane027]
  sketch-geometry (7):
    g0: LineSegment StartX=271.381 StartY=52.5 StartZ=0 EndX=269.649 EndY=55.5 EndZ=0
    g1: LineSegment StartX=269.649 StartY=55.5 StartZ=0 EndX=266.185 EndY=55.5 EndZ=0
    g2: LineSegment StartX=266.185 StartY=55.5 StartZ=0 EndX=264.453 EndY=52.5 EndZ=0
    g3: LineSegment StartX=264.453 StartY=52.5 StartZ=0 EndX=266.185 EndY=49.5 EndZ=0
    g4: LineSegment StartX=266.185 StartY=49.5 StartZ=0 EndX=269.649 EndY=49.5 EndZ=0
    g5: LineSegment StartX=269.649 StartY=49.5 StartZ=0 EndX=271.381 EndY=52.5 EndZ=0
    g6: Circle CenterX=267.917 CenterY=52.5 CenterZ=0 NormalX=0 NormalY=0 NormalZ=1 AngleXU=0 Radius=3.4641
  constraints (16):
    c: Coincident(g0,g1)
    c: Coincident(g1,g2)
    c: Coincident(g2,g3)
    c: Coincident(g3,g4)
    c: Coincident(g4,g5)
    c: Coincident(g5,g0)
    c: Equal(g0, g1-g5) x5
    c: PointOnObject(g0,g6)
    c: PointOnObject(g1,g6)
    c: PointOnObject(g2,g6)
    c: PointOnObject(g3,g6)
    c: PointOnObject(g4,g6)
    c: PointOnObject(g5,g6)
    c: Coincident(g6,g-3)
    c: Horizontal(g1)
    c: DistanceY(g4,g0) = 6
FEATURE [PartDesign::Pocket] Pocket063
  BaseFeature = -> Pocket062
  Direction = (0,1,-2e-16)
  Length = 119.058
  Length2 = 5
  Profile = -> Sketch093
  ReferenceAxis = -> Sketch093 [N_Axis]
  Type = 0
  expr: Length = Sketch091.Constraints.face_offset - 5 mm
FEATURE [PartDesign::Hole] Hole
  BaseFeature = -> Pocket063
  CustomThreadClearance = 0
  Depth = 217.499
  DepthType = 1
  Diameter = 3.5
  DrillForDepth = false
  DrillPoint = 1
  DrillPointAngle = 118
  HoleCutCountersinkAngle = 90
  HoleCutCustomValues = false
  HoleCutDepth = 0
  HoleCutDiameter = 6.1
  HoleCutType = 0
  ModelThread = false
  Profile = -> Sketch092
  Reversed = true
  Tapered = false
  TaperedAngle = 90
  ThreadClass = 0
  ThreadDepth = 217.499
  ThreadDepthType = 0
  ThreadDirection = 0
  ThreadFit = 0
  ThreadSize = 0
  ThreadType = 0
  Threaded = false
  UseCustomThreadClearance = false
FEATURE [Sketcher::SketchObject] Sketch094
  AttachmentOffset = pos=(0,0,0) rot=(0,1,0;1.5708rad)
  ExternalGeometry = -> [Sketch091]
  FullyConstrained = true
  MapMode = 7
  Placement = pos=(277.917,121.058,0) rot=(-0.293211,0.676028,0.676028;3.71203rad)
  Support = -> [Sketch091]
  sketch-geometry (1):
    g0: Circle CenterX=8.66667 CenterY=10 CenterZ=0 NormalX=0 NormalY=0 NormalZ=1 AngleXU=0 Radius=1.7
  constraints (3):
    c: Diameter(g0) = 3.4
    c: DistanceX(g0,g-3) = 5
    c: DistanceY(g0) = 10
FEATURE [PartDesign::Hole] Hole003
  BaseFeature = -> Hole
  CustomThreadClearance = 0
  Depth = 217.499
  DepthType = 1
  Diameter = 3.4
  DrillForDepth = false
  DrillPoint = 1
  DrillPointAngle = 118
  HoleCutCountersinkAngle = 90
  HoleCutCustomValues = false
  HoleCutDepth = 0
  HoleCutDiameter = 6.1
  HoleCutType = 0
  ModelThread = false
  Profile = -> Sketch094
  Reversed = true
  Tapered = false
  TaperedAngle = 90
  ThreadClass = 0
  ThreadDepth = 217.499
  ThreadDepthType = 0
  ThreadDirection = 0
  ThreadFit = 0
  ThreadSize = 0
  ThreadType = 0
  Threaded = false
  UseCustomThreadClearance = false
FEATURE [PartDesign::SubShapeBinder] Binder047
  BindCopyOnChange = 0
  BindMode = 0
  ClaimChildren = false
  Context = -> Body024 [Binder047.]
  Fuse = false
  MakeFace = true
  OffsetFill = false
  OffsetIntersection = false
  OffsetJoinType = 0
  OffsetOpenResult = false
  PartialLoad = false
  Placement = pos=(276.456,122.425,0) rot=(-0.293211,0.676028,0.676028;3.71203rad)
  Relative = false
  Support = -> [Hole003[Sketch094.]]
  _Version = 2
  expr: Placement = Sketch094.Placement * placement(vector(0; 0; 2); rotation(0; 0; 0))
FEATURE [PartDesign::Hole] Hole004
  BaseFeature = -> Hole003
  CustomThreadClearance = 0
  Depth = 25
  DepthType = 0
  Diameter = 10
  DrillForDepth = false
  DrillPoint = 1
  DrillPointAngle = 118
  HoleCutCountersinkAngle = 90
  HoleCutCustomValues = false
  HoleCutDepth = 0
  HoleCutDiameter = 6.1
  HoleCutType = 0
  ModelThread = false
  Profile = -> Binder047
  Reversed = true
  Tapered = false
  TaperedAngle = 90
  ThreadClass = 0
  ThreadDepth = 25
  ThreadDepthType = 0
  ThreadDirection = 0
  ThreadFit = 0
  ThreadSize = 0
  ThreadType = 0
  Threaded = false
  UseCustomThreadClearance = false
FEATURE [PartDesign::Plane] DatumPlane002
  AttachmentOffset = pos=(0,0,52.5) rot=(0,0,1;0rad)
  Length = 640.923
  MapMode = 5
  Placement = pos=(0,0,52.5) rot=(0,0,1;0rad)
  ResizeMode = 0
  Support = -> [XY_Plane027]
  Width = 219.813
  expr: .AttachmentOffset.Base.z = Pad019.Length / 2
FEATURE [PartDesign::Mirrored] Mirrored013
  BaseFeature = -> Hole004
  MirrorPlane = -> DatumPlane002
  Originals = -> [Hole003,Hole004]
FEATURE [PartDesign::Body] Body024
  Group = -> [Binder046,Sketch091,Pad019,Sketch092,Pocket062,Sketch093,Pocket063,Hole,Sketch094,Hole003,Binder047,Hole004,DatumPlane002,Mirrored013]
  Origin = -> Origin027
  Tip = -> Mirrored013
FEATURE [App::DocumentObjectGroup] Group  label="parts"
  Group = -> [Body,Body004,Body005,Part,Body008,Part002,Body015,Body016,Body021,Body023,Body020,Body019,Body024]
FEATURE [TechDraw::DrawViewDimension] Dimension003
  AngleOverride = false
  Arbitrary = false
  ArbitraryTolerances = false
  EqualTolerance = true
  ExtensionAngle = 0
  FormatSpec = %.2w
  FormatSpecOverTolerance = %+.2w
  FormatSpecUnderTolerance = %+.2w
  Inverted = false
  LineAngle = 0
  LockPosition = false
  MeasureType = 1
  OverTolerance = 0
  References2D = -> [View003]
  Rotation = 0
  ScaleType = 0
  TheoreticalExact = false
  Type = 2
  UnderTolerance = 0
  X = 111.035
  Y = 6.62432
FEATURE [TechDraw::DrawViewDimension] Dimension004
  AngleOverride = false
  Arbitrary = false
  ArbitraryTolerances = false
  EqualTolerance = true
  ExtensionAngle = 0
  FormatSpec = %.2w
  FormatSpecOverTolerance = %+.2w
  FormatSpecUnderTolerance = %+.2w
  Inverted = false
  LineAngle = 0
  LockPosition = false
  MeasureType = 1
  OverTolerance = 0
  References2D = -> [View003]
  Rotation = 0
  ScaleType = 0
  TheoreticalExact = false
  Type = 2
  UnderTolerance = 0
  X = -139.879
  Y = 6.05047
FEATURE [TechDraw::DrawPage] Page001
  KeepUpdated = true
  NextBalloonIndex = 1
  ProjectionType = 0
  Template = -> Template
  Views = -> [View003,View004,View005,Dimension,Dimension001,Dimension003,Dimension004]
FEATURE [App::Link] Link005  label="sink_hand001"
  LinkedObject = -> Body006
note: 2 file-system paths scrubbed to <path> (originals preserved in the JSON sidecar)

RESOLVED EXTERNAL PARTS (link-assembly join: the EXTERNAL_REF files above that resolve inside this repo's crawl, each included once):
---- part ULI-3865416.FCStd = doc fcstd_dd011da00bf9 ----
FCSTD DOCUMENT  (FreeCAD 0.22R34651 (Git))
Label: ULI-3865416
License: All rights reserved
LicenseURL: http://en.wikipedia.org/wiki/All_rights_reserved
objects: Sketcher::SketchObject×2, Spreadsheet::Sheet×1, PartDesign::SubShapeBinder×1, PartDesign::Pad×1, PartDesign::Body×1
note: 6 computed .brp shape members not serialized (recipe doc carries the construction recipe); baked Part::Feature solids carry a one-line shape summary decoded from their .brp

FEATURE [Sketcher::SketchObject] Sketch
  FullyConstrained = true
  expr: Constraints[11] = <<Properties>>.width
  sketch-geometry (5):
    g0: LineSegment StartX=-280 StartY=-10.35 StartZ=0 EndX=-280 EndY=10.35 EndZ=0
    g1: LineSegment StartX=-280 StartY=10.35 StartZ=0 EndX=280 EndY=10.35 EndZ=0
    g2: LineSegment StartX=280 StartY=10.35 StartZ=0 EndX=280 EndY=-10.35 EndZ=0
    g3: LineSegment StartX=280 StartY=-10.35 StartZ=0 EndX=-280 EndY=-10.35 EndZ=0
    g4: GeomPoint X=0 Y=0 Z=0
  constraints (12):
    c: Coincident(g0,g1)
    c: Coincident(g1,g2)
    c: Coincident(g2,g3)
    c: Coincident(g3,g0)
    c: Horizontal(g1)
    c: Horizontal(g3)
    c: Vertical(g0)
    c: Vertical(g2)
    c: Symmetric(g1,g0,g4)
    c: Coincident(g4,g-1)
    c: DistanceX(g0,g1) = 560
    c: DistanceY(g0,g1) = 20.7
FEATURE [Sketcher::SketchObject] Sketch001
  FullyConstrained = true
  expr: Constraints[11] = <<Properties>>.width
  expr: Constraints[12] = <<Properties>>.height
  sketch-geometry (5):
    g0: LineSegment StartX=-10.35 StartY=33.4 StartZ=0 EndX=-10.35 EndY=0 EndZ=0
    g1: LineSegment StartX=-10.35 StartY=0 StartZ=0 EndX=10.35 EndY=0 EndZ=0
    g2: LineSegment StartX=10.35 StartY=0 StartZ=0 EndX=10.35 EndY=33.4 EndZ=0
    g3: LineSegment StartX=10.35 StartY=33.4 StartZ=0 EndX=-10.35 EndY=33.4 EndZ=0
    g4: GeomPoint X=0 Y=16.7 Z=0
  constraints (13):
    c: Coincident(g0,g1)
    c: Coincident(g1,g2)
    c: Coincident(g2,g3)
    c: Coincident(g3,g0)
    c: Horizontal(g1)
    c: Horizontal(g3)
    c: Vertical(g0)
    c: Vertical(g2)
    c: Symmetric(g1,g0,g4)
    c: PointOnObject(g4,g-2)
    c: PointOnObject(g1,g-1)
    c: DistanceX(g1,g1) = 20.7
    c: DistanceY(g2,g2) = 33.4
FEATURE [Spreadsheet::Sheet] Spreadsheet  label="Properties"
  cells = B2(length)==560 mm; C2(width)==20.7 mm; D2(height)==33.4 mm; E2(base_height)==22 mm; F2(light_height)==height - base_height
FEATURE [PartDesign::SubShapeBinder] Binder
  BindCopyOnChange = 0
  BindMode = 0
  ClaimChildren = false
  Context = -> Body [Binder.]
  Fuse = false
  MakeFace = true
  OffsetFill = false
  OffsetIntersection = false
  OffsetJoinType = 0
  OffsetOpenResult = false
  PartialLoad = false
  Placement = pos=(0,0,0) rot=(0.57735,0.57735,0.57735;2.0944rad)
  Relative = true
  Support = -> [Sketch001]
  _Version = 2
FEATURE [PartDesign::Pad] Pad
  Direction = (1,-2e-16,2e-16)
  Length = 560
  Length2 = 10
  Midplane = true
  Placement = pos=(0,0,0) rot=(0.57735,0.57735,0.57735;2.0944rad)
  Profile = -> Binder
  Type = 0
  expr: Length = <<Properties>>.length
FEATURE [PartDesign::Body] Body
  Group = -> [Binder,Pad]
  Origin = -> Origin
  Tip = -> Pad
---- part composit-properties.FCStd = doc fcstd_d99993d4ac97 ----
FCSTD DOCUMENT  (FreeCAD 1.1R38827 (Git))
Label: composit-properties
License: All rights reserved
LicenseURL: http://en.wikipedia.org/wiki/All_rights_reserved
objects: Spreadsheet::Sheet×1

FEATURE [Spreadsheet::Sheet] Spreadsheet  label="Properties"
  cells = B2(thickness)==3 mm; C2(al_thickness)==0.3 mm; D2(bend_r)==0.1 mm
---- part dropper.FCStd = doc fcstd_03601a3bb068 ----
FCSTD DOCUMENT  (FreeCAD 1.1R38827 (Git))
Label: dropper
License: All rights reserved
LicenseURL: http://en.wikipedia.org/wiki/All_rights_reserved
objects: Sketcher::SketchObject×9, Part::FeaturePython×4, PartDesign::Revolution×3, PartDesign::Body×2, PartDesign::CoordinateSystem×1, Spreadsheet::Sheet×1, PartDesign::SubShapeBinder×1, PartDesign::Pad×1, PartDesign::Pocket×1, PartDesign::Groove×1, App::Part×1
note: 44 computed .brp shape members not serialized (recipe doc carries the construction recipe); baked Part::Feature solids carry a one-line shape summary decoded from their .brp

FEATURE [Sketcher::SketchObject] Sketch005
  ArcFitTolerance = 0
  AttachmentSupport = -> [YZ_Plane001]
  FullyConstrained = true
  MakeInternals = false
  MapMode = 5
  Placement = pos=(0,0,0) rot=(0.57735,0.57735,0.57735;2.0944rad)
  sketch-geometry (14):
    g0: LineSegment StartX=11.3 StartY=0 StartZ=0 EndX=11.3 EndY=1 EndZ=0
    g1: LineSegment StartX=11.3 StartY=1 StartZ=0 EndX=10.7 EndY=1 EndZ=0
    g2: LineSegment StartX=10.7 StartY=1 StartZ=0 EndX=10.7 EndY=9.9 EndZ=0
    g3: LineSegment StartX=10.7 StartY=9.9 StartZ=0 EndX=6.6 EndY=9.9 EndZ=0
    g4: LineSegment StartX=6.6 StartY=9.9 StartZ=0 EndX=6.6 EndY=3 EndZ=0
    g5: LineSegment StartX=6.6 StartY=3 StartZ=0 EndX=2.5 EndY=3 EndZ=0
    g6: LineSegment StartX=2.5 StartY=3 StartZ=0 EndX=2.5 EndY=20 EndZ=0
    g7: LineSegment StartX=2.5 StartY=20 StartZ=0 EndX=1.45 EndY=20 EndZ=0
    g8: LineSegment StartX=1.45 StartY=20 StartZ=0 EndX=1.45 EndY=2.5 EndZ=0
    g9: LineSegment StartX=1.45 StartY=2.5 StartZ=0 EndX=7 EndY=-0.6 EndZ=0
    g10: LineSegment StartX=7 StartY=-0.6 StartZ=0 EndX=7 EndY=8.85 EndZ=0
    g11: LineSegment StartX=7 StartY=8.85 StartZ=0 EndX=9.5 EndY=8.85 EndZ=0
    g12: LineSegment StartX=9.5 StartY=8.85 StartZ=0 EndX=9.5 EndY=0 EndZ=0
    g13: LineSegment StartX=9.5 StartY=0 StartZ=0 EndX=11.3 EndY=0 EndZ=0
  constraints (43):
    c: PointOnObject(g0,g-1)
    c: Vertical(g0)
    c: Coincident(g0,g1)
    c: Horizontal(g1)
    c: Coincident(g1,g2)
    c: Vertical(g2)
    c: Coincident(g2,g3)
    c: Horizontal(g3)
    c: Coincident(g3,g4)
    c: Vertical(g4)
    c: Coincident(g4,g5)
    c: Coincident(g5,g6)
    c: Vertical(g6)
    c: Coincident(g6,g7)
    c: Horizontal(g7)
    c: Coincident(g7,g8)
    c: Vertical(g8)
    c: Coincident(g8,g9)
    c: Coincident(g9,g10)
    c: Vertical(g10)
    c: Coincident(g10,g11)
    c: Horizontal(g11)
    c: Coincident(g11,g12)
    c: Vertical(g12)
    c: Coincident(g12,g13)
    c: Coincident(g13,g0)
    c: Horizontal(g13)
    c: DistanceX(g0) = 11.3  'outer_r'
    c: DistanceY(g0) = 1
    c: DistanceY(g2) = 9.9
    c: DistanceX(g1,g0) = 0.6
    c: DistanceX(g3,g2) = 4.1
    c: DistanceY(g4,g3) = 6.9
    c: DistanceX(g6) = 2.5
    c: DistanceX(g7) = 1.45
    c: DistanceY(g9,g3) = 10.5
    c: DistanceX(g12,g0) = 1.8
    c: DistanceY(g11) = 8.85
    c: DistanceX(g9) = 7
    c: DistanceY(g9,g6) = 20.6
    c: Horizontal(g5)
    c: DistanceY(g8,g5) = 0.5
    c: DistanceY(g7) = 20
FEATURE [PartDesign::Revolution] Revolution002
  Angle = 360
  Angle2 = 60
  Axis = (0,0,1)
  Base = (0,0,0)
  Placement = pos=(0,0,0) rot=(1,1,1;2.0944rad)
  Profile = -> Sketch005
  ReferenceAxis = -> Sketch005 [V_Axis]
  Reversed = true
  Suppressed = false
  Type = 0
FEATURE [Sketcher::SketchObject] Sketch006
  ArcFitTolerance = 0
  AttachmentSupport = -> [YZ_Plane001]
  FullyConstrained = true
  MakeInternals = false
  MapMode = 5
  Placement = pos=(0,0,0) rot=(0.57735,0.57735,0.57735;2.0944rad)
  expr: Constraints[27] = Sketch005.Constraints.outer_r
  expr: Constraints[28] = Sketch005.Constraints[28]
  expr: Constraints[29] = Sketch005.Constraints[29]
  expr: Constraints[30] = Sketch005.Constraints[30]
  expr: Constraints[31] = Sketch005.Constraints[31]
  expr: Constraints[32] = Sketch005.Constraints[32]
  expr: Constraints[33] = Sketch005.Constraints[33]
  expr: Constraints[34] = Sketch005.Constraints[34]
  expr: Constraints[35] = Sketch005.Constraints[35]
  expr: Constraints[36] = Sketch005.Constraints[36]
  expr: Constraints[37] = Sketch005.Constraints[37]
  expr: Constraints[38] = Sketch005.Constraints[38]
  expr: Constraints[39] = Sketch005.Constraints[39]
  expr: Constraints[41] = Sketch005.Constraints[41]
  expr: Constraints[69] = Sketch005.Constraints.outer_r
  expr: Constraints[70] = Sketch005.Constraints[28]
  expr: Constraints[71] = Sketch005.Constraints[29]
  expr: Constraints[72] = Sketch005.Constraints[30]
  expr: Constraints[73] = Sketch005.Constraints[31]
  expr: Constraints[74] = Sketch005.Constraints[32]
  expr: Constraints[75] = Sketch005.Constraints[33]
  expr: Constraints[76] = Sketch005.Constraints[34]
  expr: Constraints[77] = Sketch005.Constraints[35]
  expr: Constraints[78] = Sketch005.Constraints[36]
  expr: Constraints[79] = Sketch005.Constraints[37]
  expr: Constraints[80] = Sketch005.Constraints[38]
  expr: Constraints[81] = Sketch005.Constraints[39]
  expr: Constraints[83] = Sketch005.Constraints[41]
  sketch-geometry (32):
    g0: LineSegment [constr] StartX=11.3 StartY=0 StartZ=0 EndX=11.3 EndY=1 EndZ=0
    g1: LineSegment [constr] StartX=11.3 StartY=1 StartZ=0 EndX=10.7 EndY=1 EndZ=0
    g2: LineSegment [constr] StartX=10.7 StartY=1 StartZ=0 EndX=10.7 EndY=9.9 EndZ=0
    g3: LineSegment [constr] StartX=10.7 StartY=9.9 StartZ=0 EndX=6.6 EndY=9.9 EndZ=0
    g4: LineSegment StartX=6.6 StartY=9.9 StartZ=0 EndX=6.6 EndY=3 EndZ=0
    g5: LineSegment StartX=6.6 StartY=3 StartZ=0 EndX=2.5 EndY=3 EndZ=0
    g6: LineSegment [constr] StartX=2.5 StartY=3 StartZ=0 EndX=2.5 EndY=20 EndZ=0
    g7: LineSegment [constr] StartX=2.5 StartY=20 StartZ=0 EndX=1.45 EndY=20 EndZ=0
    g8: LineSegment [constr] StartX=1.45 StartY=20 StartZ=0 EndX=1.45 EndY=2.5 EndZ=0
    g9: LineSegment [constr] StartX=1.45 StartY=2.5 StartZ=0 EndX=7 EndY=-0.6 EndZ=0
    g10: LineSegment [constr] StartX=7 StartY=-0.6 StartZ=0 EndX=7 EndY=8.85 EndZ=0
    g11: LineSegment [constr] StartX=7 StartY=8.85 StartZ=0 EndX=9.5 EndY=8.85 EndZ=0
    g12: LineSegment [constr] StartX=9.5 StartY=8.85 StartZ=0 EndX=9.5 EndY=0 EndZ=0
    g13: LineSegment [constr] StartX=9.5 StartY=0 StartZ=0 EndX=11.3 EndY=0 EndZ=0
    g14: LineSegment [constr] StartX=11.3 StartY=0 StartZ=0 EndX=11.3 EndY=1 EndZ=0
    g15: LineSegment [constr] StartX=11.3 StartY=1 StartZ=0 EndX=10.7 EndY=1 EndZ=0
    g16: LineSegment [constr] StartX=10.7 StartY=1 StartZ=0 EndX=10.7 EndY=9.9 EndZ=0
    g17: LineSegment [constr] StartX=10.7 StartY=9.9 StartZ=0 EndX=6.6 EndY=9.9 EndZ=0
    g18: LineSegment [constr] StartX=6.6 StartY=9.9 StartZ=0 EndX=6.6 EndY=3 EndZ=0
    g19: LineSegment [constr] StartX=6.6 StartY=3 StartZ=0 EndX=2.5 EndY=3 EndZ=0
    g20: LineSegment [constr] StartX=2.5 StartY=3 StartZ=0 EndX=2.5 EndY=20 EndZ=0
    g21: LineSegment [constr] StartX=2.5 StartY=20 StartZ=0 EndX=1.45 EndY=20 EndZ=0
    g22: LineSegment [constr] StartX=1.45 StartY=20 StartZ=0 EndX=1.45 EndY=2.5 EndZ=0
    g23: LineSegment [constr] StartX=1.45 StartY=2.5 StartZ=0 EndX=7 EndY=-0.6 EndZ=0
    g24: LineSegment [constr] StartX=7 StartY=-0.6 StartZ=0 EndX=7 EndY=8.85 EndZ=0
    g25: LineSegment [constr] StartX=7 StartY=8.85 StartZ=0 EndX=9.5 EndY=8.85 EndZ=0
    g26: LineSegment [constr] StartX=9.5 StartY=8.85 StartZ=0 EndX=9.5 EndY=0 EndZ=0
    g27: LineSegment [constr] StartX=9.5 StartY=0 StartZ=0 EndX=11.3 EndY=0 EndZ=0
    g28: LineSegment StartX=2.5 StartY=3 StartZ=0 EndX=2.04763 EndY=3 EndZ=0
    g29: LineSegment StartX=2.04763 StartY=3 StartZ=0 EndX=2.04763 EndY=12.6758 EndZ=0
    g30: LineSegment StartX=2.04763 StartY=12.6758 StartZ=0 EndX=6.6 EndY=9.9 EndZ=0
    g31: GeomPoint [constr] X=2.5 Y=12.4 Z=0
  constraints (94):
    c: PointOnObject(g0,g-1)
    c: Vertical(g0)
    c: Coincident(g0,g1)
    c: Horizontal(g1)
    c: Coincident(g1,g2)
    c: Vertical(g2)
    c: Coincident(g2,g3)
    c: Horizontal(g3)
    c: Coincident(g3,g4)
    c: Vertical(g4)
    c: Coincident(g4,g5)
    c: Coincident(g5,g6)
    c: Vertical(g6)
    c: Coincident(g6,g7)
    c: Horizontal(g7)
    c: Coincident(g7,g8)
    c: Vertical(g8)
    c: Coincident(g8,g9)
    c: Coincident(g9,g10)
    c: Vertical(g10)
    c: Coincident(g10,g11)
    c: Horizontal(g11)
    c: Coincident(g11,g12)
    c: Vertical(g12)
    c: Coincident(g12,g13)
    c: Coincident(g13,g0)
    c: Horizontal(g13)
    c: DistanceX(g0) = 11.3
    c: DistanceY(g0) = 1
    c: DistanceY(g2) = 9.9
    c: DistanceX(g1,g0) = 0.6
    c: DistanceX(g3,g2) = 4.1
    c: DistanceY(g4,g3) = 6.9
    c: DistanceX(g6) = 2.5
    c: DistanceX(g7) = 1.45
    c: DistanceY(g9,g3) = 10.5
    c: DistanceX(g12,g0) = 1.8
    c: DistanceY(g11) = 8.85
    c: DistanceX(g9) = 7
    c: DistanceY(g9,g6) = 20.6
    c: Horizontal(g5)
    c: DistanceY(g8,g5) = 0.5
    c: PointOnObject(g14,g-1)
    c: Vertical(g14)
    c: Coincident(g14,g15)
    c: Horizontal(g15)
    c: Coincident(g15,g16)
    c: Vertical(g16)
    c: Coincident(g16,g17)
    c: Horizontal(g17)
    c: Coincident(g17,g18)
    c: Vertical(g18)
    c: Coincident(g18,g19)
    c: Coincident(g19,g20)
    c: Vertical(g20)
    c: Coincident(g20,g21)
    c: Horizontal(g21)
    c: Coincident(g21,g22)
    c: Vertical(g22)
    c: Coincident(g22,g23)
    c: Coincident(g23,g24)
    c: Vertical(g24)
    c: Coincident(g24,g25)
    c: Horizontal(g25)
    c: Coincident(g25,g26)
    c: Vertical(g26)
    c: Coincident(g26,g27)
    c: Coincident(g27,g14)
    c: Horizontal(g27)
    c: DistanceX(g14) = 11.3
    c: DistanceY(g14) = 1
    c: DistanceY(g16) = 9.9
    c: DistanceX(g15,g14) = 0.6
    c: DistanceX(g17,g16) = 4.1
    c: DistanceY(g18,g17) = 6.9
    c: DistanceX(g20) = 2.5
    c: DistanceX(g21) = 1.45
    c: DistanceY(g23,g17) = 10.5
    c: DistanceX(g26,g14) = 1.8
    c: DistanceY(g25) = 8.85
    c: DistanceX(g23) = 7
    c: DistanceY(g23,g20) = 20.6
    c: Horizontal(g19)
    c: DistanceY(g22,g19) = 0.5
    c: Coincident(g28,g5)
    c: Horizontal(g28)
    c: Coincident(g29,g28)
    c: Vertical(g29)
    c: Coincident(g30,g29)
    c: Coincident(g30,g4)
    c: PointOnObject(g31,g30)
    c: PointOnObject(g31,g6)
    c: DistanceY(g4,g31) = 2.5
    c: DistanceX(g29,g31) = 0.452366
FEATURE [PartDesign::Body] Body001
  AllowCompound = false
  Group = -> [Sketch005,Revolution002,Sketch006]
  Origin = -> Origin001
  Placement = pos=(0,0,2.5) rot=(0,0,1;0rad)
  Tip = -> Revolution002
FEATURE [Sketcher::SketchObject] Sketch007  label="base"
  ArcFitTolerance = 0
  FullyConstrained = true
  MakeInternals = false
  expr: .Constraints.r = Sketch005.Constraints.outer_r + 0.5 mm
  sketch-geometry (1):
    g0: Circle CenterX=0 CenterY=0 CenterZ=0 NormalX=0 NormalY=0 NormalZ=1 AngleXU=0 Radius=11.8
  constraints (2):
    c: Coincident(g0,g-1)
    c: Radius(g0) = 11.8  'r'
FEATURE [Sketcher::SketchObject] Sketch002
  ArcFitTolerance = 0
  AttachmentSupport = -> [YZ_Plane]
  FullyConstrained = true
  MakeInternals = false
  MapMode = 5
  Placement = pos=(0,0,0) rot=(0.57735,0.57735,0.57735;2.0944rad)
  expr: Constraints[18] = Sketch001.Constraints[18]
  expr: Constraints[19] = Sketch001.Constraints[19]
  expr: Constraints[20] = Sketch001.Constraints[20]
  expr: Constraints[21] = Sketch001.Constraints[21]
  expr: Constraints[22] = Sketch001.Constraints[22]
  expr: Constraints[23] = Sketch001.Constraints[23]
  expr: Constraints[24] = Sketch001.Constraints[24]
  expr: Constraints[25] = Sketch001.Constraints[25]
  expr: Constraints[27] = Sketch001.Constraints[27]
  sketch-geometry (13):
    g0: LineSegment [constr] StartX=1.15 StartY=0 StartZ=0 EndX=1.15 EndY=-18.1612 EndZ=0
    g1: LineSegment StartX=1.15 StartY=-18.1612 StartZ=0 EndX=2.765 EndY=-8.77 EndZ=0
    g2: LineSegment [constr] StartX=2.765 StartY=-8.77 StartZ=0 EndX=2.2 EndY=-8.77 EndZ=0
    g3: LineSegment [constr] StartX=2.2 StartY=-8.77 StartZ=0 EndX=2.2 EndY=-5.32 EndZ=0
    g4: LineSegment [constr] StartX=2.2 StartY=-5.32 StartZ=0 EndX=3.35 EndY=-5.32 EndZ=0
    g5: LineSegment [constr] StartX=3.35 StartY=-5.32 StartZ=0 EndX=3.35 EndY=-3.66 EndZ=0
    g6: LineSegment [constr] StartX=3.35 StartY=-3.66 StartZ=0 EndX=2.65 EndY=-3.66 EndZ=0
    g7: LineSegment [constr] StartX=2.65 StartY=-3.66 StartZ=0 EndX=2.65 EndY=0 EndZ=0
    g8: LineSegment [constr] StartX=2.65 StartY=0 StartZ=0 EndX=1.15 EndY=0 EndZ=0
    g9: GeomPoint [constr] X=-2.765 Y=-8.77 Z=0
    g10: GeomPoint [constr] X=-2.765 Y=-8.77 Z=0
    g11: LineSegment StartX=1.15 StartY=-18.1612 StartZ=0 EndX=-3.0574 EndY=-18.1612 EndZ=0
    g12: LineSegment StartX=-3.0574 StartY=-18.1612 StartZ=0 EndX=2.765 EndY=-8.77 EndZ=0
  constraints (34):
    c: PointOnObject(g0,g-1)
    c: Vertical(g0)
    c: Coincident(g0,g1)
    c: Coincident(g1,g2)
    c: Horizontal(g2)
    c: Coincident(g2,g3)
    c: Vertical(g3)
    c: Coincident(g3,g4)
    c: Horizontal(g4)
    c: Coincident(g4,g5)
    c: Vertical(g5)
    c: Coincident(g5,g6)
    c: Horizontal(g6)
    c: Coincident(g6,g7)
    c: PointOnObject(g7,g-1)
    c: Vertical(g7)
    c: Coincident(g7,g8)
    c: Coincident(g8,g0)
    c: DistanceY(g2,g3) = 3.45
    c: DistanceY(g4,g5) = 1.66
    c: DistanceY(g6,g7) = 3.66
    c: DistanceX(g2) = 2.2
    c: DistanceX(g4) = 3.35
    c: DistanceX(g0) = 1.15
    c: DistanceX(g7) = 2.65
    c: DistanceX(g1) = 2.765
    c: Symmetric(g9,g1,g-2)
    c: Distance(g9,g1) = 5.45
    c: Symmetric(g10,g1,g-2)
    c: Coincident(g11,g1)
    c: Horizontal(g11)
    c: Coincident(g12,g11)
    c: Coincident(g12,g1)
    c: Distance(g9,g12) = 4.7
FEATURE [Sketcher::SketchObject] Sketch001
  ArcFitTolerance = 0
  AttachmentSupport = -> [XZ_Plane]
  FullyConstrained = true
  MakeInternals = false
  MapMode = 5
  Placement = pos=(0,0,0) rot=(1,0,0;1.5708rad)
  sketch-geometry (10):
    g0: LineSegment StartX=1.15 StartY=0 StartZ=0 EndX=1.15 EndY=-18.1612 EndZ=0
    g1: LineSegment StartX=1.15 StartY=-18.1612 StartZ=0 EndX=2.765 EndY=-8.77 EndZ=0
    g2: LineSegment StartX=2.765 StartY=-8.77 StartZ=0 EndX=2.2 EndY=-8.77 EndZ=0
    g3: LineSegment StartX=2.2 StartY=-8.77 StartZ=0 EndX=2.2 EndY=-5.32 EndZ=0
    g4: LineSegment StartX=2.2 StartY=-5.32 StartZ=0 EndX=3.35 EndY=-5.32 EndZ=0
    g5: LineSegment StartX=3.35 StartY=-5.32 StartZ=0 EndX=3.35 EndY=-3.66 EndZ=0
    g6: LineSegment StartX=3.35 StartY=-3.66 StartZ=0 EndX=2.65 EndY=-3.66 EndZ=0
    g7: LineSegment StartX=2.65 StartY=-3.66 StartZ=0 EndX=2.65 EndY=0 EndZ=0
    g8: LineSegment StartX=2.65 StartY=0 StartZ=0 EndX=1.15 EndY=0 EndZ=0
    g9: GeomPoint [constr] X=-2.765 Y=-8.77 Z=0
  constraints (28):
    c: PointOnObject(g0,g-1)
    c: Vertical(g0)
    c: Coincident(g0,g1)
    c: Coincident(g1,g2)
    c: Horizontal(g2)
    c: Coincident(g2,g3)
    c: Vertical(g3)
    c: Coincident(g3,g4)
    c: Horizontal(g4)
    c: Coincident(g4,g5)
    c: Vertical(g5)
    c: Coincident(g5,g6)
    c: Horizontal(g6)
    c: Coincident(g6,g7)
    c: PointOnObject(g7,g-1)
    c: Vertical(g7)
    c: Coincident(g7,g8)
    c: Coincident(g8,g0)
    c: DistanceY(g2,g3) = 3.45
    c: DistanceY(g4,g5) = 1.66
    c: DistanceY(g6,g7) = 3.66
    c: DistanceX(g2) = 2.2
    c: DistanceX(g4) = 3.35
    c: DistanceX(g0) = 1.15
    c: DistanceX(g7) = 2.65
    c: DistanceX(g1) = 2.765
    c: Symmetric(g9,g1,g-2)
    c: Distance(g9,g1) = 5.45
FEATURE [Sketcher::SketchObject] Sketch  label="fix_sketch"
  ArcFitTolerance = 0
  AttachmentSupport = -> [XY_Plane]
  FullyConstrained = true
  MakeInternals = false
  MapMode = 5
  sketch-geometry (5):
    g0: ArcOfCircle CenterX=0 CenterY=0 CenterZ=0 NormalX=0 NormalY=0 NormalZ=1 AngleXU=0 Radius=10.5 StartAngle=0.496317 EndAngle=1.5708
    g1: ArcOfCircle CenterX=16.5 CenterY=0 CenterZ=0 NormalX=0 NormalY=0 NormalZ=1 AngleXU=0 Radius=3.25 StartAngle=0 EndAngle=1.34547
    g2: LineSegment StartX=17.2261 StartY=3.16784 StartZ=0 EndX=9.23309 EndY=5 EndZ=0
    g3: GeomPoint [constr] X=-19.75 Y=0 Z=0
    g4: GeomPoint [constr] X=0 Y=-10.5 Z=0
  constraints (14):
    c: PointOnObject(g0,g-2)
    c: PointOnObject(g1,g-1)
    c: PointOnObject(g1,g-1)
    c: Coincident(g2,g0)
    c: Tangent(g2,g1) = -1.5708
    c: Diameter(g0) = 21
    c: DistanceX(g1) = 19.75
    c: DistanceY(g0) = 5
    c: Diameter(g1) = 6.5
    c: Coincident(g0,g-1)
    c: Symmetric(g3,g1,g-2)
    c: DistanceX(g3,g1) = 39.5  'length'
    c: Symmetric(g4,g0,g-1)
    c: DistanceY(g4,g0) = 21  'width'
FEATURE [Sketcher::SketchObject] Sketch004
  ArcFitTolerance = 0
  AttachmentSupport = -> [YZ_Plane]
  FullyConstrained = true
  MakeInternals = false
  MapMode = 5
  Placement = pos=(0,0,0) rot=(0.57735,0.57735,0.57735;2.0944rad)
  expr: Constraints[3] = Sketch003.Constraints[9]
  sketch-geometry (6):
    g0: LineSegment StartX=7.75 StartY=10.9 StartZ=0 EndX=0 EndY=10.9 EndZ=0
    g1: LineSegment StartX=0 StartY=10.9 StartZ=0 EndX=0 EndY=1.5 EndZ=0
    g2: LineSegment StartX=0 StartY=1.5 StartZ=0 EndX=7.25 EndY=1.5 EndZ=0
    g3: LineSegment StartX=7.25 StartY=1.5 StartZ=0 EndX=7.25 EndY=2.5 EndZ=0
    g4: LineSegment StartX=7.25 StartY=2.5 StartZ=0 EndX=7.75 EndY=4 EndZ=0
    g5: LineSegment StartX=7.75 StartY=4 StartZ=0 EndX=7.75 EndY=10.9 EndZ=0
  constraints (18):
    c: Coincident(g0,g1)
    c: Horizontal(g0)
    c: Vertical(g1)
    c: DistanceY(g0) = 10.9
    c: Horizontal(g2)
    c: Coincident(g2,g3)
    c: Vertical(g3)
    c: Coincident(g3,g4)
    c: Coincident(g4,g5)
    c: Vertical(g5)
    c: Coincident(g0,g5)
    c: Coincident(g1,g2)
    c: DistanceY(g1,g0) = 9.4
    c: DistanceX(g0) = 7.75
    c: DistanceY(g2,g3) = 1
    c: DistanceY(g3,g4) = 1.5
    c: DistanceX(g2,g4) = 0.5
    c: Vertical(g1,g-1)
FEATURE [Sketcher::SketchObject] Sketch003
  ArcFitTolerance = 0
  AttachmentSupport = -> [YZ_Plane]
  FullyConstrained = true
  MakeInternals = false
  MapMode = 5
  Placement = pos=(0,0,0) rot=(0.57735,0.57735,0.57735;2.0944rad)
  sketch-geometry (4):
    g0: LineSegment StartX=0 StartY=0 StartZ=0 EndX=8.825 EndY=0 EndZ=0
    g1: LineSegment StartX=8.825 StartY=0 StartZ=0 EndX=8.825 EndY=10.9 EndZ=0
    g2: LineSegment StartX=8.825 StartY=10.9 StartZ=0 EndX=0 EndY=10.9 EndZ=0
    g3: LineSegment StartX=0 StartY=10.9 StartZ=0 EndX=0 EndY=0 EndZ=0
  constraints (11):
    c: Coincident(g0,g1)
    c: Coincident(g1,g2)
    c: Coincident(g2,g3)
    c: Coincident(g3,g0)
    c: Horizontal(g0)
    c: Horizontal(g2)
    c: Vertical(g1)
    c: Vertical(g3)
    c: Coincident(g0,g-1)
    c: DistanceY(g2) = 10.9
    c: DistanceX(g0) = 8.825
FEATURE [PartDesign::CoordinateSystem] LCS_0
  AttacherType = Attacher::AttachEngine3D
  AttachmentOffset = pos=(0,0,2.45) rot=(0,0,1;0rad)
  AttachmentSupport = -> [X_Axis002]
  MapMode = 2
  Placement = pos=(0,0,2.45) rot=(0,0,1;0rad)
FEATURE [Spreadsheet::Sheet] Spreadsheet  label="Properties"
  cells = B2(top_d)==22.6 mm; C2(bot_d)==21 mm; D2(top_height)==20 mm; E2(bot_base_height)==2.4 mm; F2(total_height)==22.4 mm; G2(total_width)==38.9 mm
FEATURE [Part::FeaturePython] Mirror  label="Mirror of Sketch"  # WARN: FeaturePython — macro-defined, semantics opaque (R4)
  ExposePlacement = false
  FlipX = true
  FlipY = false
  FlipZ = false
  MarkerShape = 1
  MarkerSize = 0
  NumElements = 0
  Object = -> Sketch
  ObjectTraversal = 0
  Type = lattice2Mirror.LatticeMirror
  isLattice = 0
FEATURE [Part::FeaturePython] Mirror001  label="Mirror001 of Mirror of Sketch"  # WARN: FeaturePython — macro-defined, semantics opaque (R4)
  ExposePlacement = false
  FlipX = false
  FlipY = true
  FlipZ = false
  MarkerShape = 1
  MarkerSize = 0
  NumElements = 0
  Object = -> Mirror
  ObjectTraversal = 0
  Type = lattice2Mirror.LatticeMirror
  isLattice = 0
FEATURE [Part::FeaturePython] Mirror002  label="Mirror002 of Mirror001 of Mirror of Sketch"  # WARN: FeaturePython — macro-defined, semantics opaque (R4)
  ExposePlacement = false
  FlipX = true
  FlipY = false
  FlipZ = false
  MarkerShape = 1
  MarkerSize = 0
  NumElements = 0
  Object = -> Mirror001
  ObjectTraversal = 0
  Type = lattice2Mirror.LatticeMirror
  isLattice = 0
FEATURE [PartDesign::SubShapeBinder] Binder
  BindCopyOnChange = 0
  BindMode = 0
  ClaimChildren = true
  Context = -> Part [Body.Binder.]
  Fuse = false
  MakeFace = true
  OffsetFill = false
  OffsetIntersection = false
  OffsetJoinType = 0
  OffsetOpenResult = false
  PartialLoad = false
  Relative = true
  Support = -> [Connect]
  _Version = 2
FEATURE [PartDesign::Pad] Pad
  Direction = (0,0,1)
  Length = 2.45
  Length2 = 10
  Profile = -> Binder
  Suppressed = false
  Type = 0
FEATURE [PartDesign::Revolution] Revolution
  Angle = 360
  Angle2 = 60
  Axis = (0,2e-16,1)
  Base = (0,0,0)
  BaseFeature = -> Pad
  Profile = -> Sketch001
  ReferenceAxis = -> Sketch001 [V_Axis]
  Reversed = true
  Suppressed = false
  Type = 0
FEATURE [PartDesign::Pocket] Pocket
  BaseFeature = -> Revolution
  Direction = (-1,0,0)
  Length = 5
  Length2 = 5
  Midplane = true
  Profile = -> Sketch002
  ReferenceAxis = -> Sketch002 [N_Axis]
  Suppressed = false
  Type = 1
FEATURE [PartDesign::Revolution] Revolution001
  Angle = 360
  Angle2 = 60
  Axis = (0,0,1)
  Base = (0,0,0)
  BaseFeature = -> Pocket
  Profile = -> Sketch003
  ReferenceAxis = -> Sketch003 [V_Axis]
  Reversed = true
  Suppressed = false
  Type = 0
FEATURE [PartDesign::Groove] Groove
  Angle = 360
  Angle2 = 60
  Axis = (0,0,1)
  Base = (0,0,0)
  BaseFeature = -> Revolution001
  Profile = -> Sketch004
  ReferenceAxis = -> Sketch004 [V_Axis]
  Suppressed = false
  Type = 0
FEATURE [Sketcher::SketchObject] Sketch008  label="feed"
  ArcFitTolerance = 0
  AttachmentSupport = -> [XY_Plane]
  FullyConstrained = true
  MakeInternals = false
  MapMode = 5
  sketch-geometry (1):
    g0: Circle CenterX=0 CenterY=0 CenterZ=0 NormalX=0 NormalY=0 NormalZ=1 AngleXU=0 Radius=4
  constraints (2):
    c: Coincident(g0,g-1)
    c: Diameter(g0) = 8
FEATURE [PartDesign::Body] Body
  AllowCompound = false
  Group = -> [Sketch,Pad,Sketch001,Revolution,Sketch002,Pocket,Sketch003,Sketch004,Revolution001,Groove,Sketch008,Binder]
  Origin = -> Origin
  Tip = -> Groove
FEATURE [App::Part] Part  label="dropper"
  Group = -> [LCS_0,Body001,Body]
  Origin = -> Origin002
FEATURE [Part::FeaturePython] Connect  label="fix"  # WARN: FeaturePython — macro-defined, semantics opaque (R4)
  Objects = -> [Sketch,Mirror002,Mirror001,Mirror]
  Tolerance = 0
---- part module.FCStd = doc fcstd_3955753b3a20 ----
FCSTD DOCUMENT  (FreeCAD 1.1R38827 (Git))
Label: module
License: All rights reserved
LicenseURL: http://en.wikipedia.org/wiki/All_rights_reserved
objects: Sketcher::SketchObject×2, Part::Feature×1, PartDesign::FeatureBase×1, PartDesign::Body×1, Spreadsheet::Sheet×1
note: 8 computed .brp shape members not serialized (recipe doc carries the construction recipe); baked Part::Feature solids carry a one-line shape summary decoded from their .brp

FEATURE [Part::Feature] Part__Feature  label="module002"
  shape: bbox 170 x 148 x 41.12 mm, 715 faces (baked)
FEATURE [Sketcher::SketchObject] Sketch  label="module_holes"
  ArcFitTolerance = 0
  FullyConstrained = true
  MakeInternals = false
  sketch-geometry (10):
    g0: LineSegment StartX=59.5 StartY=-3.5 StartZ=0 EndX=59.5 EndY=3.5 EndZ=0
    g1: LineSegment StartX=59.5 StartY=3.5 StartZ=0 EndX=72.5 EndY=3.5 EndZ=0
    g2: LineSegment StartX=72.5 StartY=3.5 StartZ=0 EndX=72.5 EndY=-3.5 EndZ=0
    g3: LineSegment StartX=72.5 StartY=-3.5 StartZ=0 EndX=59.5 EndY=-3.5 EndZ=0
    g4: GeomPoint [constr] X=66 Y=0 Z=0
    g5: LineSegment StartX=-72.5 StartY=-3.5 StartZ=0 EndX=-72.5 EndY=3.5 EndZ=0
    g6: LineSegment StartX=-72.5 StartY=3.5 StartZ=0 EndX=-59.5 EndY=3.5 EndZ=0
    g7: LineSegment StartX=-59.5 StartY=3.5 StartZ=0 EndX=-59.5 EndY=-3.5 EndZ=0
    g8: LineSegment StartX=-59.5 StartY=-3.5 StartZ=0 EndX=-72.5 EndY=-3.5 EndZ=0
    g9: GeomPoint [constr] X=-66 Y=0 Z=0
  constraints (25):
    c: Coincident(g0,g1)
    c: Coincident(g1,g2)
    c: Coincident(g2,g3)
    c: Coincident(g3,g0)
    c: Horizontal(g1)
    c: Horizontal(g3)
    c: Vertical(g0)
    c: Vertical(g2)
    c: Symmetric(g1,g0,g4)
    c: PointOnObject(g4,g-1)
    c: Coincident(g5,g6)
    c: Coincident(g6,g7)
    c: Coincident(g7,g8)
    c: Coincident(g8,g5)
    c: Horizontal(g6)
    c: Horizontal(g8)
    c: Vertical(g5)
    c: Vertical(g7)
    c: Symmetric(g6,g5,g9)
    c: Symmetric(g9,g4,g-2)
    c: Equal(g1,g6)
    c: Equal(g7,g2)
    c: DistanceX(g1,g1) = 13
    c: DistanceY(g2,g2) = 7
    c: DistanceX(g9,g4) = 132
FEATURE [PartDesign::FeatureBase] BaseFeature
  BaseFeature = -> Part__Feature
  Placement = pos=(0,0,0) rot=(0,0,1;1.5708rad)
  Suppressed = false
FEATURE [PartDesign::Body] Body  label="module_Body"
  AllowCompound = false
  BaseFeature = -> Part__Feature
  Group = -> [BaseFeature]
  Origin = -> Origin
  Tip = -> BaseFeature
FEATURE [Spreadsheet::Sheet] Spreadsheet  label="Properties"
  cells = B2(module_width)==148 mm; C2(module_height)==160 mm; D2(module_fixture_distance_x)==132 mm; E2(module_fixture_distance_y)==80 mm; F2(module_hole_x)==13 mm; G2(module_hole_y)==7 mm
FEATURE [Sketcher::SketchObject] Sketch001  label="module_holes001"
  ArcFitTolerance = 0
  FullyConstrained = true
  MakeInternals = false
  sketch-geometry (10):
    g0: LineSegment StartX=59 StartY=-3.5 StartZ=0 EndX=59 EndY=3.5 EndZ=0
    g1: LineSegment StartX=59 StartY=3.5 StartZ=0 EndX=73 EndY=3.5 EndZ=0
    g2: LineSegment StartX=73 StartY=3.5 StartZ=0 EndX=73 EndY=-3.5 EndZ=0
    g3: LineSegment StartX=73 StartY=-3.5 StartZ=0 EndX=59 EndY=-3.5 EndZ=0
    g4: GeomPoint [constr] X=66 Y=0 Z=0
    g5: LineSegment StartX=-73 StartY=-3.5 StartZ=0 EndX=-73 EndY=3.5 EndZ=0
    g6: LineSegment StartX=-73 StartY=3.5 StartZ=0 EndX=-59 EndY=3.5 EndZ=0
    g7: LineSegment StartX=-59 StartY=3.5 StartZ=0 EndX=-59 EndY=-3.5 EndZ=0
    g8: LineSegment StartX=-59 StartY=-3.5 StartZ=0 EndX=-73 EndY=-3.5 EndZ=0
    g9: GeomPoint [constr] X=-66 Y=0 Z=0
  constraints (25):
    c: Coincident(g0,g1)
    c: Coincident(g1,g2)
    c: Coincident(g2,g3)
    c: Coincident(g3,g0)
    c: Horizontal(g1)
    c: Horizontal(g3)
    c: Vertical(g0)
    c: Vertical(g2)
    c: Symmetric(g1,g0,g4)
    c: PointOnObject(g4,g-1)
    c: Coincident(g5,g6)
    c: Coincident(g6,g7)
    c: Coincident(g7,g8)
    c: Coincident(g8,g5)
    c: Horizontal(g6)
    c: Horizontal(g8)
    c: Vertical(g5)
    c: Vertical(g7)
    c: Symmetric(g6,g5,g9)
    c: Symmetric(g9,g4,g-2)
    c: Equal(g1,g6)
    c: Equal(g7,g2)
    c: DistanceX(g1,g1) = 14
    c: DistanceY(g2,g2) = 7
    c: DistanceX(g9,g4) = 132
